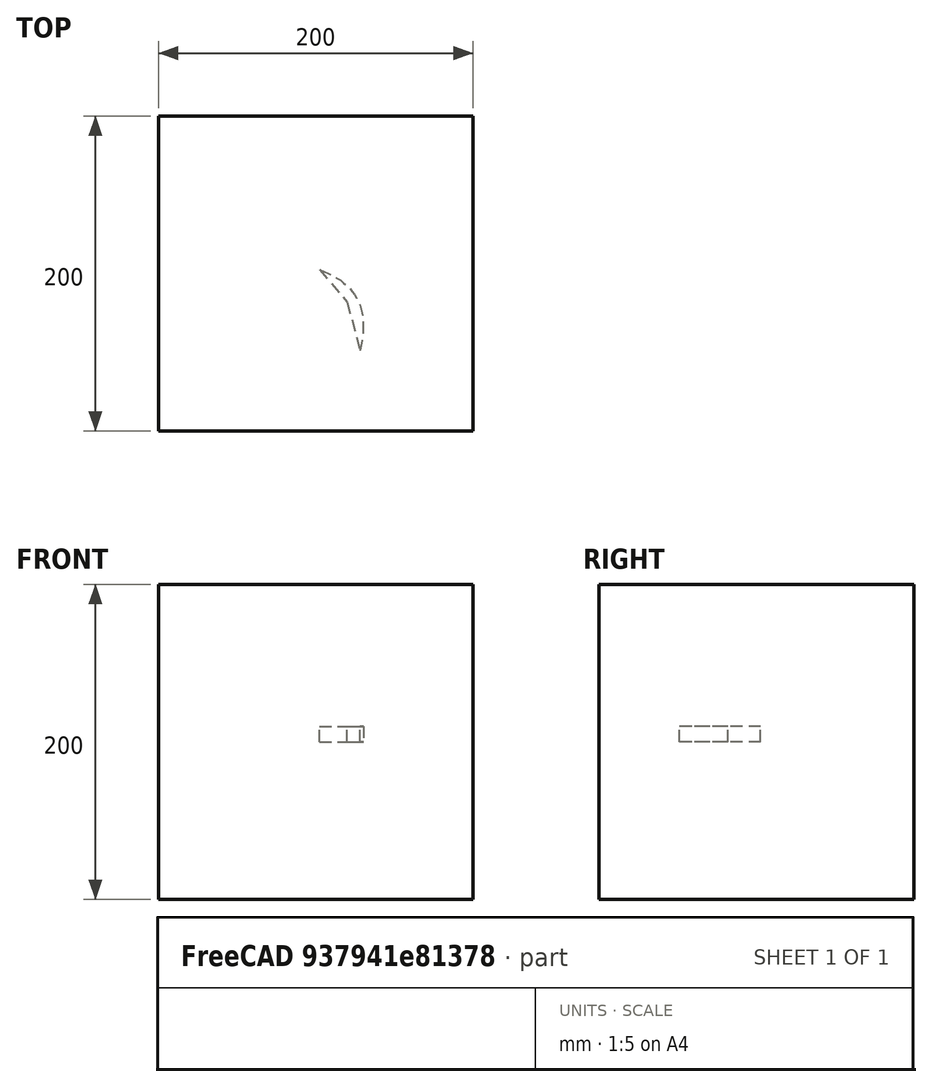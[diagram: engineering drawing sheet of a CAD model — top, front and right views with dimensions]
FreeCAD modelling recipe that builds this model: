
FCSTD DOCUMENT  (FreeCAD 0.21R33694 (Git))
Label: extrudedParabola-2
License: All rights reserved
LicenseURL: http://en.wikipedia.org/wiki/All_rights_reserved
objects: App::DocumentObjectGroupPython×1248, App::Part×2, Part::FeaturePython×1, Sketcher::SketchObject×1, Part::Extrusion×1
note: 3 computed .brp shape members not serialized (recipe doc carries the construction recipe); baked Part::Feature solids carry a one-line shape summary decoded from their .brp

FEATURE [App::DocumentObjectGroupPython] HALFPI  # scripted group (container) (typed FeaturePython)
  name = HALFPI
  value = pi/2.
FEATURE [App::DocumentObjectGroupPython] PI  # scripted group (container) (typed FeaturePython)
  name = PI
  value = 1.*pi
FEATURE [App::DocumentObjectGroupPython] TWOPI  # scripted group (container) (typed FeaturePython)
  name = TWOPI
  value = 2.*pi
FEATURE [App::DocumentObjectGroupPython] Constants  # scripted group (container) (typed FeaturePython)
  Group = -> [HALFPI,PI,TWOPI]
FEATURE [App::DocumentObjectGroupPython] Variables  # scripted group (container) (typed FeaturePython)
FEATURE [App::DocumentObjectGroupPython] Quantities  # scripted group (container) (typed FeaturePython)
FEATURE [App::DocumentObjectGroupPython] Isotopes  # scripted group (container) (typed FeaturePython)
FEATURE [App::DocumentObjectGroupPython] Elements  # scripted group (container) (typed FeaturePython)
FEATURE [App::DocumentObjectGroupPython] G4Isotopes  # scripted group (container) (typed FeaturePython)
FEATURE [App::DocumentObjectGroupPython] H_element  # scripted group (container) (typed FeaturePython)
  Z = 1
  atom_value = 1.008
  formula = H
  name = H_element
FEATURE [App::DocumentObjectGroupPython] He_element  # scripted group (container) (typed FeaturePython)
  Z = 2
  atom_value = 4.0026
  formula = He
  name = He_element
FEATURE [App::DocumentObjectGroupPython] Li_element  # scripted group (container) (typed FeaturePython)
  Z = 3
  atom_value = 6.94
  formula = Li
  name = Li_element
FEATURE [App::DocumentObjectGroupPython] Be_element  # scripted group (container) (typed FeaturePython)
  Z = 4
  atom_value = 9.01218
  formula = Be
  name = Be_element
FEATURE [App::DocumentObjectGroupPython] B_element  # scripted group (container) (typed FeaturePython)
  Z = 5
  atom_value = 10.81
  formula = B
  name = B_element
FEATURE [App::DocumentObjectGroupPython] C_element  # scripted group (container) (typed FeaturePython)
  Z = 6
  atom_value = 12.011
  formula = C
  name = C_element
FEATURE [App::DocumentObjectGroupPython] N_element  # scripted group (container) (typed FeaturePython)
  Z = 7
  atom_value = 14.007
  formula = N
  name = N_element
FEATURE [App::DocumentObjectGroupPython] O_element  # scripted group (container) (typed FeaturePython)
  Z = 8
  atom_value = 15.999
  formula = O
  name = O_element
FEATURE [App::DocumentObjectGroupPython] F_element  # scripted group (container) (typed FeaturePython)
  Z = 9
  atom_value = 18.9984
  formula = F
  name = F_element
FEATURE [App::DocumentObjectGroupPython] Ne_element  # scripted group (container) (typed FeaturePython)
  Z = 10
  atom_value = 20.1797
  formula = Ne
  name = Ne_element
FEATURE [App::DocumentObjectGroupPython] Na_element  # scripted group (container) (typed FeaturePython)
  Z = 11
  atom_value = 22.9898
  formula = Na
  name = Na_element
FEATURE [App::DocumentObjectGroupPython] Mg_element  # scripted group (container) (typed FeaturePython)
  Z = 12
  atom_value = 24.305
  formula = Mg
  name = Mg_element
FEATURE [App::DocumentObjectGroupPython] Al_element  # scripted group (container) (typed FeaturePython)
  Z = 13
  atom_value = 26.9815
  formula = Al
  name = Al_element
FEATURE [App::DocumentObjectGroupPython] Si_element  # scripted group (container) (typed FeaturePython)
  Z = 14
  atom_value = 28.085
  formula = Si
  name = Si_element
FEATURE [App::DocumentObjectGroupPython] P_element  # scripted group (container) (typed FeaturePython)
  Z = 15
  atom_value = 30.9738
  formula = P
  name = P_element
FEATURE [App::DocumentObjectGroupPython] S_element  # scripted group (container) (typed FeaturePython)
  Z = 16
  atom_value = 32.06
  formula = S
  name = S_element
FEATURE [App::DocumentObjectGroupPython] Cl_element  # scripted group (container) (typed FeaturePython)
  Z = 17
  atom_value = 35.45
  formula = Cl
  name = Cl_element
FEATURE [App::DocumentObjectGroupPython] Ar_element  # scripted group (container) (typed FeaturePython)
  Z = 18
  atom_value = 39.95
  formula = Ar
  name = Ar_element
FEATURE [App::DocumentObjectGroupPython] K_element  # scripted group (container) (typed FeaturePython)
  Z = 19
  atom_value = 39.0983
  formula = K
  name = K_element
FEATURE [App::DocumentObjectGroupPython] Ca_element  # scripted group (container) (typed FeaturePython)
  Z = 20
  atom_value = 40.078
  formula = Ca
  name = Ca_element
FEATURE [App::DocumentObjectGroupPython] Sc_element  # scripted group (container) (typed FeaturePython)
  Z = 21
  atom_value = 44.9559
  formula = Sc
  name = Sc_element
FEATURE [App::DocumentObjectGroupPython] Ti_element  # scripted group (container) (typed FeaturePython)
  Z = 22
  atom_value = 47.867
  formula = Ti
  name = Ti_element
FEATURE [App::DocumentObjectGroupPython] V_element  # scripted group (container) (typed FeaturePython)
  Z = 23
  atom_value = 50.9415
  formula = V
  name = V_element
FEATURE [App::DocumentObjectGroupPython] Cr_element  # scripted group (container) (typed FeaturePython)
  Z = 24
  atom_value = 51.9961
  formula = Cr
  name = Cr_element
FEATURE [App::DocumentObjectGroupPython] Mn_element  # scripted group (container) (typed FeaturePython)
  Z = 25
  atom_value = 54.938
  formula = Mn
  name = Mn_element
FEATURE [App::DocumentObjectGroupPython] Fe_element  # scripted group (container) (typed FeaturePython)
  Z = 26
  atom_value = 55.845
  formula = Fe
  name = Fe_element
FEATURE [App::DocumentObjectGroupPython] Co_element  # scripted group (container) (typed FeaturePython)
  Z = 27
  atom_value = 58.9332
  formula = Co
  name = Co_element
FEATURE [App::DocumentObjectGroupPython] Ni_element  # scripted group (container) (typed FeaturePython)
  Z = 28
  atom_value = 58.6934
  formula = Ni
  name = Ni_element
FEATURE [App::DocumentObjectGroupPython] Cu_element  # scripted group (container) (typed FeaturePython)
  Z = 29
  atom_value = 63.546
  formula = Cu
  name = Cu_element
FEATURE [App::DocumentObjectGroupPython] Zn_element  # scripted group (container) (typed FeaturePython)
  Z = 30
  atom_value = 65.38
  formula = Zn
  name = Zn_element
FEATURE [App::DocumentObjectGroupPython] Ga_element  # scripted group (container) (typed FeaturePython)
  Z = 31
  atom_value = 69.723
  formula = Ga
  name = Ga_element
FEATURE [App::DocumentObjectGroupPython] Ge_element  # scripted group (container) (typed FeaturePython)
  Z = 32
  atom_value = 72.63
  formula = Ge
  name = Ge_element
FEATURE [App::DocumentObjectGroupPython] As_element  # scripted group (container) (typed FeaturePython)
  Z = 33
  atom_value = 74.9216
  formula = As
  name = As_element
FEATURE [App::DocumentObjectGroupPython] Se_element  # scripted group (container) (typed FeaturePython)
  Z = 34
  atom_value = 78.971
  formula = Se
  name = Se_element
FEATURE [App::DocumentObjectGroupPython] Br_element  # scripted group (container) (typed FeaturePython)
  Z = 35
  atom_value = 79.904
  formula = Br
  name = Br_element
FEATURE [App::DocumentObjectGroupPython] Kr_element  # scripted group (container) (typed FeaturePython)
  Z = 36
  atom_value = 83.798
  formula = Kr
  name = Kr_element
FEATURE [App::DocumentObjectGroupPython] Rb_element  # scripted group (container) (typed FeaturePython)
  Z = 37
  atom_value = 85.4678
  formula = Rb
  name = Rb_element
FEATURE [App::DocumentObjectGroupPython] Sr_element  # scripted group (container) (typed FeaturePython)
  Z = 38
  atom_value = 87.62
  formula = Sr
  name = Sr_element
FEATURE [App::DocumentObjectGroupPython] Y_element  # scripted group (container) (typed FeaturePython)
  Z = 39
  atom_value = 88.9058
  formula = Y
  name = Y_element
FEATURE [App::DocumentObjectGroupPython] Zr_element  # scripted group (container) (typed FeaturePython)
  Z = 40
  atom_value = 91.224
  formula = Zr
  name = Zr_element
FEATURE [App::DocumentObjectGroupPython] Nb_element  # scripted group (container) (typed FeaturePython)
  Z = 41
  atom_value = 92.9064
  formula = Nb
  name = Nb_element
FEATURE [App::DocumentObjectGroupPython] Mo_element  # scripted group (container) (typed FeaturePython)
  Z = 42
  atom_value = 95.95
  formula = Mo
  name = Mo_element
FEATURE [App::DocumentObjectGroupPython] Tc_element  # scripted group (container) (typed FeaturePython)
  Z = 43
  atom_value = 97
  formula = Tc
  name = Tc_element
FEATURE [App::DocumentObjectGroupPython] Ru_element  # scripted group (container) (typed FeaturePython)
  Z = 44
  atom_value = 101.07
  formula = Ru
  name = Ru_element
FEATURE [App::DocumentObjectGroupPython] Rh_element  # scripted group (container) (typed FeaturePython)
  Z = 45
  atom_value = 102.905
  formula = Rh
  name = Rh_element
FEATURE [App::DocumentObjectGroupPython] Pd_element  # scripted group (container) (typed FeaturePython)
  Z = 46
  atom_value = 106.42
  formula = Pd
  name = Pd_element
FEATURE [App::DocumentObjectGroupPython] Ag_element  # scripted group (container) (typed FeaturePython)
  Z = 47
  atom_value = 107.868
  formula = Ag
  name = Ag_element
FEATURE [App::DocumentObjectGroupPython] Cd_element  # scripted group (container) (typed FeaturePython)
  Z = 48
  atom_value = 112.414
  formula = Cd
  name = Cd_element
FEATURE [App::DocumentObjectGroupPython] In_element  # scripted group (container) (typed FeaturePython)
  Z = 49
  atom_value = 114.818
  formula = In
  name = In_element
FEATURE [App::DocumentObjectGroupPython] Sn_element  # scripted group (container) (typed FeaturePython)
  Z = 50
  atom_value = 118.71
  formula = Sn
  name = Sn_element
FEATURE [App::DocumentObjectGroupPython] Sb_element  # scripted group (container) (typed FeaturePython)
  Z = 51
  atom_value = 121.76
  formula = Sb
  name = Sb_element
FEATURE [App::DocumentObjectGroupPython] Te_element  # scripted group (container) (typed FeaturePython)
  Z = 52
  atom_value = 127.6
  formula = Te
  name = Te_element
FEATURE [App::DocumentObjectGroupPython] I_element  # scripted group (container) (typed FeaturePython)
  Z = 53
  atom_value = 126.904
  formula = I
  name = I_element
FEATURE [App::DocumentObjectGroupPython] Xe_element  # scripted group (container) (typed FeaturePython)
  Z = 54
  atom_value = 131.293
  formula = Xe
  name = Xe_element
FEATURE [App::DocumentObjectGroupPython] Cs_element  # scripted group (container) (typed FeaturePython)
  Z = 55
  atom_value = 132.905
  formula = Cs
  name = Cs_element
FEATURE [App::DocumentObjectGroupPython] Ba_element  # scripted group (container) (typed FeaturePython)
  Z = 56
  atom_value = 137.327
  formula = Ba
  name = Ba_element
FEATURE [App::DocumentObjectGroupPython] La_element  # scripted group (container) (typed FeaturePython)
  Z = 57
  atom_value = 138.905
  formula = La
  name = La_element
FEATURE [App::DocumentObjectGroupPython] Ce_element  # scripted group (container) (typed FeaturePython)
  Z = 58
  atom_value = 140.116
  formula = Ce
  name = Ce_element
FEATURE [App::DocumentObjectGroupPython] Pr_element  # scripted group (container) (typed FeaturePython)
  Z = 59
  atom_value = 140.908
  formula = Pr
  name = Pr_element
FEATURE [App::DocumentObjectGroupPython] Nd_element  # scripted group (container) (typed FeaturePython)
  Z = 60
  atom_value = 144.242
  formula = Nd
  name = Nd_element
FEATURE [App::DocumentObjectGroupPython] Pm_element  # scripted group (container) (typed FeaturePython)
  Z = 61
  atom_value = 145
  formula = Pm
  name = Pm_element
FEATURE [App::DocumentObjectGroupPython] Sm_element  # scripted group (container) (typed FeaturePython)
  Z = 62
  atom_value = 150.36
  formula = Sm
  name = Sm_element
FEATURE [App::DocumentObjectGroupPython] Eu_element  # scripted group (container) (typed FeaturePython)
  Z = 63
  atom_value = 151.964
  formula = Eu
  name = Eu_element
FEATURE [App::DocumentObjectGroupPython] Gd_element  # scripted group (container) (typed FeaturePython)
  Z = 64
  atom_value = 157.25
  formula = Gd
  name = Gd_element
FEATURE [App::DocumentObjectGroupPython] Tb_element  # scripted group (container) (typed FeaturePython)
  Z = 65
  atom_value = 158.925
  formula = Tb
  name = Tb_element
FEATURE [App::DocumentObjectGroupPython] Dy_element  # scripted group (container) (typed FeaturePython)
  Z = 66
  atom_value = 162.5
  formula = Dy
  name = Dy_element
FEATURE [App::DocumentObjectGroupPython] Ho_element  # scripted group (container) (typed FeaturePython)
  Z = 67
  atom_value = 164.93
  formula = Ho
  name = Ho_element
FEATURE [App::DocumentObjectGroupPython] Er_element  # scripted group (container) (typed FeaturePython)
  Z = 68
  atom_value = 167.259
  formula = Er
  name = Er_element
FEATURE [App::DocumentObjectGroupPython] Tm_element  # scripted group (container) (typed FeaturePython)
  Z = 69
  atom_value = 168.934
  formula = Tm
  name = Tm_element
FEATURE [App::DocumentObjectGroupPython] Yb_element  # scripted group (container) (typed FeaturePython)
  Z = 70
  atom_value = 173.045
  formula = Yb
  name = Yb_element
FEATURE [App::DocumentObjectGroupPython] Lu_element  # scripted group (container) (typed FeaturePython)
  Z = 71
  atom_value = 174.967
  formula = Lu
  name = Lu_element
FEATURE [App::DocumentObjectGroupPython] Hf_element  # scripted group (container) (typed FeaturePython)
  Z = 72
  atom_value = 178.49
  formula = Hf
  name = Hf_element
FEATURE [App::DocumentObjectGroupPython] Ta_element  # scripted group (container) (typed FeaturePython)
  Z = 73
  atom_value = 180.948
  formula = Ta
  name = Ta_element
FEATURE [App::DocumentObjectGroupPython] W_element  # scripted group (container) (typed FeaturePython)
  Z = 74
  atom_value = 183.84
  formula = W
  name = W_element
FEATURE [App::DocumentObjectGroupPython] Re_element  # scripted group (container) (typed FeaturePython)
  Z = 75
  atom_value = 186.207
  formula = Re
  name = Re_element
FEATURE [App::DocumentObjectGroupPython] Os_element  # scripted group (container) (typed FeaturePython)
  Z = 76
  atom_value = 190.23
  formula = Os
  name = Os_element
FEATURE [App::DocumentObjectGroupPython] Ir_element  # scripted group (container) (typed FeaturePython)
  Z = 77
  atom_value = 192.217
  formula = Ir
  name = Ir_element
FEATURE [App::DocumentObjectGroupPython] Pt_element  # scripted group (container) (typed FeaturePython)
  Z = 78
  atom_value = 195.084
  formula = Pt
  name = Pt_element
FEATURE [App::DocumentObjectGroupPython] Au_element  # scripted group (container) (typed FeaturePython)
  Z = 79
  atom_value = 196.967
  formula = Au
  name = Au_element
FEATURE [App::DocumentObjectGroupPython] Hg_element  # scripted group (container) (typed FeaturePython)
  Z = 80
  atom_value = 200.592
  formula = Hg
  name = Hg_element
FEATURE [App::DocumentObjectGroupPython] Tl_element  # scripted group (container) (typed FeaturePython)
  Z = 81
  atom_value = 204.38
  formula = Tl
  name = Tl_element
FEATURE [App::DocumentObjectGroupPython] Pb_element  # scripted group (container) (typed FeaturePython)
  Z = 82
  atom_value = 207.2
  formula = Pb
  name = Pb_element
FEATURE [App::DocumentObjectGroupPython] Bi_element  # scripted group (container) (typed FeaturePython)
  Z = 83
  atom_value = 208.98
  formula = Bi
  name = Bi_element
FEATURE [App::DocumentObjectGroupPython] Po_element  # scripted group (container) (typed FeaturePython)
  Z = 84
  atom_value = 209
  formula = Po
  name = Po_element
FEATURE [App::DocumentObjectGroupPython] At_element  # scripted group (container) (typed FeaturePython)
  Z = 85
  atom_value = 210
  formula = At
  name = At_element
FEATURE [App::DocumentObjectGroupPython] Rn_element  # scripted group (container) (typed FeaturePython)
  Z = 86
  atom_value = 222
  formula = Rn
  name = Rn_element
FEATURE [App::DocumentObjectGroupPython] Fr_element  # scripted group (container) (typed FeaturePython)
  Z = 87
  atom_value = 223
  formula = Fr
  name = Fr_element
FEATURE [App::DocumentObjectGroupPython] Ra_element  # scripted group (container) (typed FeaturePython)
  Z = 88
  atom_value = 226
  formula = Ra
  name = Ra_element
FEATURE [App::DocumentObjectGroupPython] Ac_element  # scripted group (container) (typed FeaturePython)
  Z = 89
  atom_value = 227
  formula = Ac
  name = Ac_element
FEATURE [App::DocumentObjectGroupPython] Th_element  # scripted group (container) (typed FeaturePython)
  Z = 90
  atom_value = 232.038
  formula = Th
  name = Th_element
FEATURE [App::DocumentObjectGroupPython] Pa_element  # scripted group (container) (typed FeaturePython)
  Z = 91
  atom_value = 231.036
  formula = Pa
  name = Pa_element
FEATURE [App::DocumentObjectGroupPython] U_element  # scripted group (container) (typed FeaturePython)
  Z = 92
  atom_value = 238.029
  formula = U
  name = U_element
FEATURE [App::DocumentObjectGroupPython] Np_element  # scripted group (container) (typed FeaturePython)
  Z = 93
  atom_value = 237
  formula = Np
  name = Np_element
FEATURE [App::DocumentObjectGroupPython] Pu_element  # scripted group (container) (typed FeaturePython)
  Z = 94
  atom_value = 244
  formula = Pu
  name = Pu_element
FEATURE [App::DocumentObjectGroupPython] Am_element  # scripted group (container) (typed FeaturePython)
  Z = 95
  atom_value = 243
  formula = Am
  name = Am_element
FEATURE [App::DocumentObjectGroupPython] Cm_element  # scripted group (container) (typed FeaturePython)
  Z = 96
  atom_value = 247
  formula = Cm
  name = Cm_element
FEATURE [App::DocumentObjectGroupPython] Bk_element  # scripted group (container) (typed FeaturePython)
  Z = 97
  atom_value = 247
  formula = Bk
  name = Bk_element
FEATURE [App::DocumentObjectGroupPython] Cf_element  # scripted group (container) (typed FeaturePython)
  Z = 98
  atom_value = 251
  formula = Cf
  name = Cf_element
FEATURE [App::DocumentObjectGroupPython] G4Elements  # scripted group (container) (typed FeaturePython)
  Group = -> [H_element,He_element,Li_element,Be_element,B_element,C_element,N_element,O_element,F_element,Ne_element,Na_element,Mg_element,Al_element,Si_element,P_element,S_element,Cl_element,Ar_element,K_element,Ca_element,Sc_element,Ti_element,V_element,Cr_element,Mn_element,Fe_element,Co_element,Ni_element,Cu_element,Zn_element,Ga_element,Ge_element,As_element,Se_element,Br_element,Kr_element,Rb_element,+61 more]
FEATURE [App::DocumentObjectGroupPython] H_element001  label="H_element : 0.101"  # scripted group (container) (typed FeaturePython)
  n = 0.101327
FEATURE [App::DocumentObjectGroupPython] C_element001  label="C_element : 0.775"  # scripted group (container) (typed FeaturePython)
  n = 0.7755
FEATURE [App::DocumentObjectGroupPython] N_element001  label="N_element : 0.035"  # scripted group (container) (typed FeaturePython)
  n = 0.035057
FEATURE [App::DocumentObjectGroupPython] O_element001  label="O_element : 0.052"  # scripted group (container) (typed FeaturePython)
  n = 0.0523159
FEATURE [App::DocumentObjectGroupPython] F_element001  label="F_element : 0.017"  # scripted group (container) (typed FeaturePython)
  n = 0.017422
FEATURE [App::DocumentObjectGroupPython] Ca_element001  label="Ca_element : 0.018"  # scripted group (container) (typed FeaturePython)
  n = 0.018378
FEATURE [App::DocumentObjectGroupPython] G4_A_150_TISSUE  label="G4_A-150_TISSUE"  # scripted group (container) (typed FeaturePython)
  Dunit = g/cm3
  Dvalue = 1.127
  Group = -> [H_element001,C_element001,N_element001,O_element001,F_element001,Ca_element001]
  conduct = 2
  density = 1
  expand = 3
  formula = G4_A-150_TISSUE
  name = G4_A-150_TISSUE
  specific = 4
FEATURE [App::DocumentObjectGroupPython] C_element002  label="C_element : 3"  # scripted group (container) (typed FeaturePython)
  n = 3
  ref = C_element
FEATURE [App::DocumentObjectGroupPython] H_element002  label="H_element : 6"  # scripted group (container) (typed FeaturePython)
  n = 6
  ref = H_element
FEATURE [App::DocumentObjectGroupPython] O_element002  label="O_element : 1"  # scripted group (container) (typed FeaturePython)
  n = 1
  ref = O_element
FEATURE [App::DocumentObjectGroupPython] G4_ACETONE  # scripted group (container) (typed FeaturePython)
  Dunit = g/cm3
  Dvalue = 0.7899
  Group = -> [C_element002,H_element002,O_element002]
  conduct = 2
  density = 1
  expand = 3
  formula = G4_ACETONE
  name = G4_ACETONE
  specific = 4
FEATURE [App::DocumentObjectGroupPython] C_element003  label="C_element : 2"  # scripted group (container) (typed FeaturePython)
  n = 2
  ref = C_element
FEATURE [App::DocumentObjectGroupPython] H_element003  label="H_element : 2"  # scripted group (container) (typed FeaturePython)
  n = 2
  ref = H_element
FEATURE [App::DocumentObjectGroupPython] G4_ACETYLENE  # scripted group (container) (typed FeaturePython)
  Dunit = g/cm3
  Dvalue = 0.0010967
  Group = -> [C_element003,H_element003]
  conduct = 2
  density = 1
  expand = 3
  formula = G4_ACETYLENE
  name = G4_ACETYLENE
  specific = 4
FEATURE [App::DocumentObjectGroupPython] C_element004  label="C_element : 5"  # scripted group (container) (typed FeaturePython)
  n = 5
  ref = C_element
FEATURE [App::DocumentObjectGroupPython] H_element004  label="H_element : 5"  # scripted group (container) (typed FeaturePython)
  n = 5
  ref = H_element
FEATURE [App::DocumentObjectGroupPython] N_element002  label="N_element : 5"  # scripted group (container) (typed FeaturePython)
  n = 5
  ref = N_element
FEATURE [App::DocumentObjectGroupPython] G4_ADENINE  # scripted group (container) (typed FeaturePython)
  Dunit = g/cm3
  Dvalue = 1.6
  Group = -> [C_element004,H_element004,N_element002]
  conduct = 2
  density = 1
  expand = 3
  formula = G4_ADENINE
  name = G4_ADENINE
  specific = 4
FEATURE [App::DocumentObjectGroupPython] H_element005  label="H_element : 0.114"  # scripted group (container) (typed FeaturePython)
  n = 0.114
FEATURE [App::DocumentObjectGroupPython] C_element005  label="C_element : 0.598"  # scripted group (container) (typed FeaturePython)
  n = 0.598
FEATURE [App::DocumentObjectGroupPython] N_element003  label="N_element : 0.007"  # scripted group (container) (typed FeaturePython)
  n = 0.007
FEATURE [App::DocumentObjectGroupPython] O_element003  label="O_element : 0.278"  # scripted group (container) (typed FeaturePython)
  n = 0.278
FEATURE [App::DocumentObjectGroupPython] Na_element001  label="Na_element : 0.001"  # scripted group (container) (typed FeaturePython)
  n = 0.001
FEATURE [App::DocumentObjectGroupPython] S_element001  label="S_element : 0.001"  # scripted group (container) (typed FeaturePython)
  n = 0.001
FEATURE [App::DocumentObjectGroupPython] Cl_element001  label="Cl_element : 0.001"  # scripted group (container) (typed FeaturePython)
  n = 0.001
FEATURE [App::DocumentObjectGroupPython] G4_ADIPOSE_TISSUE_ICRP  # scripted group (container) (typed FeaturePython)
  Dunit = g/cm3
  Dvalue = 0.95
  Group = -> [H_element005,C_element005,N_element003,O_element003,Na_element001,S_element001,Cl_element001]
  conduct = 2
  density = 1
  expand = 3
  formula = G4_ADIPOSE_TISSUE_ICRP
  name = G4_ADIPOSE_TISSUE_ICRP
  specific = 4
FEATURE [App::DocumentObjectGroupPython] C_element006  label="C_element : 0.000"  # scripted group (container) (typed FeaturePython)
  n = 0.000124
FEATURE [App::DocumentObjectGroupPython] N_element004  label="N_element : 0.755"  # scripted group (container) (typed FeaturePython)
  n = 0.755268
FEATURE [App::DocumentObjectGroupPython] O_element004  label="O_element : 0.232"  # scripted group (container) (typed FeaturePython)
  n = 0.231781
FEATURE [App::DocumentObjectGroupPython] Ar_element001  label="Ar_element : 0.013"  # scripted group (container) (typed FeaturePython)
  n = 0.012827
FEATURE [App::DocumentObjectGroupPython] G4_AIR  # scripted group (container) (typed FeaturePython)
  Dunit = g/cm3
  Dvalue = 0.00120479
  Group = -> [C_element006,N_element004,O_element004,Ar_element001]
  conduct = 2
  density = 1
  expand = 3
  formula = G4_AIR
  name = G4_AIR
  specific = 4
FEATURE [App::DocumentObjectGroupPython] C_element007  label="C_element : 006"  # scripted group (container) (typed FeaturePython)
  n = 3
  ref = C_element
FEATURE [App::DocumentObjectGroupPython] H_element006  label="H_element : 7"  # scripted group (container) (typed FeaturePython)
  n = 7
  ref = H_element
FEATURE [App::DocumentObjectGroupPython] N_element005  label="N_element : 1"  # scripted group (container) (typed FeaturePython)
  n = 1
  ref = N_element
FEATURE [App::DocumentObjectGroupPython] O_element005  label="O_element : 2"  # scripted group (container) (typed FeaturePython)
  n = 2
  ref = O_element
FEATURE [App::DocumentObjectGroupPython] G4_ALANINE  # scripted group (container) (typed FeaturePython)
  Dunit = g/cm3
  Dvalue = 1.42
  Group = -> [C_element007,H_element006,N_element005,O_element005]
  conduct = 2
  density = 1
  expand = 3
  formula = G4_ALANINE
  name = G4_ALANINE
  specific = 4
FEATURE [App::DocumentObjectGroupPython] Al_element001  label="Al_element : 2"  # scripted group (container) (typed FeaturePython)
  n = 2
  ref = Al_element
FEATURE [App::DocumentObjectGroupPython] O_element006  label="O_element : 3"  # scripted group (container) (typed FeaturePython)
  n = 3
  ref = O_element
FEATURE [App::DocumentObjectGroupPython] G4_ALUMINUM_OXIDE  # scripted group (container) (typed FeaturePython)
  Dunit = g/cm3
  Dvalue = 3.97
  Group = -> [Al_element001,O_element006]
  conduct = 2
  density = 1
  expand = 3
  formula = G4_ALUMINUM_OXIDE
  name = G4_ALUMINUM_OXIDE
  specific = 4
FEATURE [App::DocumentObjectGroupPython] H_element007  label="H_element : 0.106"  # scripted group (container) (typed FeaturePython)
  n = 0.10593
FEATURE [App::DocumentObjectGroupPython] C_element008  label="C_element : 0.789"  # scripted group (container) (typed FeaturePython)
  n = 0.788974
FEATURE [App::DocumentObjectGroupPython] O_element007  label="O_element : 0.105"  # scripted group (container) (typed FeaturePython)
  n = 0.105096
FEATURE [App::DocumentObjectGroupPython] G4_AMBER  # scripted group (container) (typed FeaturePython)
  Dunit = g/cm3
  Dvalue = 1.1
  Group = -> [H_element007,C_element008,O_element007]
  conduct = 2
  density = 1
  expand = 3
  formula = G4_AMBER
  name = G4_AMBER
  specific = 4
FEATURE [App::DocumentObjectGroupPython] N_element006  label="N_element : 006"  # scripted group (container) (typed FeaturePython)
  n = 1
  ref = N_element
FEATURE [App::DocumentObjectGroupPython] H_element008  label="H_element : 3"  # scripted group (container) (typed FeaturePython)
  n = 3
  ref = H_element
FEATURE [App::DocumentObjectGroupPython] G4_AMMONIA  # scripted group (container) (typed FeaturePython)
  Dunit = g/cm3
  Dvalue = 0.000826019
  Group = -> [N_element006,H_element008]
  conduct = 2
  density = 1
  expand = 3
  formula = G4_AMMONIA
  name = G4_AMMONIA
  specific = 4
FEATURE [App::DocumentObjectGroupPython] C_element009  label="C_element : 6"  # scripted group (container) (typed FeaturePython)
  n = 6
  ref = C_element
FEATURE [App::DocumentObjectGroupPython] H_element009  label="H_element : 008"  # scripted group (container) (typed FeaturePython)
  n = 7
  ref = H_element
FEATURE [App::DocumentObjectGroupPython] N_element007  label="N_element : 007"  # scripted group (container) (typed FeaturePython)
  n = 1
  ref = N_element
FEATURE [App::DocumentObjectGroupPython] G4_ANILINE  # scripted group (container) (typed FeaturePython)
  Dunit = g/cm3
  Dvalue = 1.0235
  Group = -> [C_element009,H_element009,N_element007]
  conduct = 2
  density = 1
  expand = 3
  formula = G4_ANILINE
  name = G4_ANILINE
  specific = 4
FEATURE [App::DocumentObjectGroupPython] C_element010  label="C_element : 14"  # scripted group (container) (typed FeaturePython)
  n = 14
  ref = C_element
FEATURE [App::DocumentObjectGroupPython] H_element010  label="H_element : 10"  # scripted group (container) (typed FeaturePython)
  n = 10
  ref = H_element
FEATURE [App::DocumentObjectGroupPython] G4_ANTHRACENE  # scripted group (container) (typed FeaturePython)
  Dunit = g/cm3
  Dvalue = 1.283
  Group = -> [C_element010,H_element010]
  conduct = 2
  density = 1
  expand = 3
  formula = G4_ANTHRACENE
  name = G4_ANTHRACENE
  specific = 4
FEATURE [App::DocumentObjectGroupPython] H_element011  label="H_element : 0.065"  # scripted group (container) (typed FeaturePython)
  n = 0.0654709
FEATURE [App::DocumentObjectGroupPython] C_element011  label="C_element : 0.537"  # scripted group (container) (typed FeaturePython)
  n = 0.536944
FEATURE [App::DocumentObjectGroupPython] N_element008  label="N_element : 0.021"  # scripted group (container) (typed FeaturePython)
  n = 0.0215
FEATURE [App::DocumentObjectGroupPython] O_element008  label="O_element : 0.032"  # scripted group (container) (typed FeaturePython)
  n = 0.032085
FEATURE [App::DocumentObjectGroupPython] F_element002  label="F_element : 0.167"  # scripted group (container) (typed FeaturePython)
  n = 0.167411
FEATURE [App::DocumentObjectGroupPython] Ca_element002  label="Ca_element : 0.177"  # scripted group (container) (typed FeaturePython)
  n = 0.176589
FEATURE [App::DocumentObjectGroupPython] G4_B_100_BONE  label="G4_B-100_BONE"  # scripted group (container) (typed FeaturePython)
  Dunit = g/cm3
  Dvalue = 1.45
  Group = -> [H_element011,C_element011,N_element008,O_element008,F_element002,Ca_element002]
  conduct = 2
  density = 1
  expand = 3
  formula = G4_B-100_BONE
  name = G4_B-100_BONE
  specific = 4
FEATURE [App::DocumentObjectGroupPython] H_element012  label="H_element : 0.057"  # scripted group (container) (typed FeaturePython)
  n = 0.057441
FEATURE [App::DocumentObjectGroupPython] C_element012  label="C_element : 0.790"  # scripted group (container) (typed FeaturePython)
  n = 0.774591
FEATURE [App::DocumentObjectGroupPython] O_element009  label="O_element : 0.168"  # scripted group (container) (typed FeaturePython)
  n = 0.167968
FEATURE [App::DocumentObjectGroupPython] G4_BAKELITE  # scripted group (container) (typed FeaturePython)
  Dunit = g/cm3
  Dvalue = 1.25
  Group = -> [H_element012,C_element012,O_element009]
  conduct = 2
  density = 1
  expand = 3
  formula = G4_BAKELITE
  name = G4_BAKELITE
  specific = 4
FEATURE [App::DocumentObjectGroupPython] Ba_element001  label="Ba_element : 1"  # scripted group (container) (typed FeaturePython)
  n = 1
  ref = Ba_element
FEATURE [App::DocumentObjectGroupPython] F_element003  label="F_element : 2"  # scripted group (container) (typed FeaturePython)
  n = 2
  ref = F_element
FEATURE [App::DocumentObjectGroupPython] G4_BARIUM_FLUORIDE  # scripted group (container) (typed FeaturePython)
  Dunit = g/cm3
  Dvalue = 4.89
  Group = -> [Ba_element001,F_element003]
  conduct = 2
  density = 1
  expand = 3
  formula = G4_BARIUM_FLUORIDE
  name = G4_BARIUM_FLUORIDE
  specific = 4
FEATURE [App::DocumentObjectGroupPython] Ba_element002  label="Ba_element : 002"  # scripted group (container) (typed FeaturePython)
  n = 1
  ref = Ba_element
FEATURE [App::DocumentObjectGroupPython] S_element002  label="S_element : 1"  # scripted group (container) (typed FeaturePython)
  n = 1
  ref = S_element
FEATURE [App::DocumentObjectGroupPython] O_element010  label="O_element : 4"  # scripted group (container) (typed FeaturePython)
  n = 4
  ref = O_element
FEATURE [App::DocumentObjectGroupPython] G4_BARIUM_SULFATE  # scripted group (container) (typed FeaturePython)
  Dunit = g/cm3
  Dvalue = 4.5
  Group = -> [Ba_element002,S_element002,O_element010]
  conduct = 2
  density = 1
  expand = 3
  formula = G4_BARIUM_SULFATE
  name = G4_BARIUM_SULFATE
  specific = 4
FEATURE [App::DocumentObjectGroupPython] C_element013  label="C_element : 007"  # scripted group (container) (typed FeaturePython)
  n = 6
  ref = C_element
FEATURE [App::DocumentObjectGroupPython] H_element013  label="H_element : 009"  # scripted group (container) (typed FeaturePython)
  n = 6
  ref = H_element
FEATURE [App::DocumentObjectGroupPython] G4_BENZENE  # scripted group (container) (typed FeaturePython)
  Dunit = g/cm3
  Dvalue = 0.87865
  Group = -> [C_element013,H_element013]
  conduct = 2
  density = 1
  expand = 3
  formula = G4_BENZENE
  name = G4_BENZENE
  specific = 4
FEATURE [App::DocumentObjectGroupPython] Be_element001  label="Be_element : 1"  # scripted group (container) (typed FeaturePython)
  n = 1
  ref = Be_element
FEATURE [App::DocumentObjectGroupPython] O_element011  label="O_element : 005"  # scripted group (container) (typed FeaturePython)
  n = 1
  ref = O_element
FEATURE [App::DocumentObjectGroupPython] G4_BERYLLIUM_OXIDE  # scripted group (container) (typed FeaturePython)
  Dunit = g/cm3
  Dvalue = 3.01
  Group = -> [Be_element001,O_element011]
  conduct = 2
  density = 1
  expand = 3
  formula = G4_BERYLLIUM_OXIDE
  name = G4_BERYLLIUM_OXIDE
  specific = 4
FEATURE [App::DocumentObjectGroupPython] Bi_element001  label="Bi_element : 4"  # scripted group (container) (typed FeaturePython)
  n = 4
  ref = Bi_element
FEATURE [App::DocumentObjectGroupPython] Ge_element001  label="Ge_element : 3"  # scripted group (container) (typed FeaturePython)
  n = 3
  ref = Ge_element
FEATURE [App::DocumentObjectGroupPython] O_element012  label="O_element : 12"  # scripted group (container) (typed FeaturePython)
  n = 12
  ref = O_element
FEATURE [App::DocumentObjectGroupPython] G4_BGO  # scripted group (container) (typed FeaturePython)
  Dunit = g/cm3
  Dvalue = 7.13
  Group = -> [Bi_element001,Ge_element001,O_element012]
  conduct = 2
  density = 1
  expand = 3
  formula = G4_BGO
  name = G4_BGO
  specific = 4
FEATURE [App::DocumentObjectGroupPython] H_element014  label="H_element : 0.102"  # scripted group (container) (typed FeaturePython)
  n = 0.102
FEATURE [App::DocumentObjectGroupPython] C_element014  label="C_element : 0.110"  # scripted group (container) (typed FeaturePython)
  n = 0.11
FEATURE [App::DocumentObjectGroupPython] N_element009  label="N_element : 0.033"  # scripted group (container) (typed FeaturePython)
  n = 0.033
FEATURE [App::DocumentObjectGroupPython] O_element013  label="O_element : 0.745"  # scripted group (container) (typed FeaturePython)
  n = 0.745
FEATURE [App::DocumentObjectGroupPython] Na_element002  label="Na_element : 0.002"  # scripted group (container) (typed FeaturePython)
  n = 0.001
FEATURE [App::DocumentObjectGroupPython] P_element001  label="P_element : 0.001"  # scripted group (container) (typed FeaturePython)
  n = 0.001
FEATURE [App::DocumentObjectGroupPython] S_element003  label="S_element : 0.002"  # scripted group (container) (typed FeaturePython)
  n = 0.002
FEATURE [App::DocumentObjectGroupPython] Cl_element002  label="Cl_element : 0.003"  # scripted group (container) (typed FeaturePython)
  n = 0.003
FEATURE [App::DocumentObjectGroupPython] K_element001  label="K_element : 0.002"  # scripted group (container) (typed FeaturePython)
  n = 0.002
FEATURE [App::DocumentObjectGroupPython] Fe_element001  label="Fe_element : 0.001"  # scripted group (container) (typed FeaturePython)
  n = 0.001
FEATURE [App::DocumentObjectGroupPython] G4_BLOOD_ICRP  # scripted group (container) (typed FeaturePython)
  Dunit = g/cm3
  Dvalue = 1.06
  Group = -> [H_element014,C_element014,N_element009,O_element013,Na_element002,P_element001,S_element003,Cl_element002,K_element001,Fe_element001]
  conduct = 2
  density = 1
  expand = 3
  formula = G4_BLOOD_ICRP
  name = G4_BLOOD_ICRP
  specific = 4
FEATURE [App::DocumentObjectGroupPython] H_element015  label="H_element : 0.064"  # scripted group (container) (typed FeaturePython)
  n = 0.064
FEATURE [App::DocumentObjectGroupPython] C_element015  label="C_element : 0.278"  # scripted group (container) (typed FeaturePython)
  n = 0.278
FEATURE [App::DocumentObjectGroupPython] N_element010  label="N_element : 0.027"  # scripted group (container) (typed FeaturePython)
  n = 0.027
FEATURE [App::DocumentObjectGroupPython] O_element014  label="O_element : 0.410"  # scripted group (container) (typed FeaturePython)
  n = 0.41
FEATURE [App::DocumentObjectGroupPython] Mg_element001  label="Mg_element : 0.002"  # scripted group (container) (typed FeaturePython)
  n = 0.002
FEATURE [App::DocumentObjectGroupPython] P_element002  label="P_element : 0.070"  # scripted group (container) (typed FeaturePython)
  n = 0.07
FEATURE [App::DocumentObjectGroupPython] S_element004  label="S_element : 0.003"  # scripted group (container) (typed FeaturePython)
  n = 0.002
FEATURE [App::DocumentObjectGroupPython] Ca_element003  label="Ca_element : 0.147"  # scripted group (container) (typed FeaturePython)
  n = 0.147
FEATURE [App::DocumentObjectGroupPython] G4_BONE_COMPACT_ICRU  # scripted group (container) (typed FeaturePython)
  Dunit = g/cm3
  Dvalue = 1.85
  Group = -> [H_element015,C_element015,N_element010,O_element014,Mg_element001,P_element002,S_element004,Ca_element003]
  conduct = 2
  density = 1
  expand = 3
  formula = G4_BONE_COMPACT_ICRU
  name = G4_BONE_COMPACT_ICRU
  specific = 4
FEATURE [App::DocumentObjectGroupPython] H_element016  label="H_element : 0.034"  # scripted group (container) (typed FeaturePython)
  n = 0.034
FEATURE [App::DocumentObjectGroupPython] C_element016  label="C_element : 0.155"  # scripted group (container) (typed FeaturePython)
  n = 0.155
FEATURE [App::DocumentObjectGroupPython] N_element011  label="N_element : 0.042"  # scripted group (container) (typed FeaturePython)
  n = 0.042
FEATURE [App::DocumentObjectGroupPython] O_element015  label="O_element : 0.435"  # scripted group (container) (typed FeaturePython)
  n = 0.435
FEATURE [App::DocumentObjectGroupPython] Na_element003  label="Na_element : 0.003"  # scripted group (container) (typed FeaturePython)
  n = 0.001
FEATURE [App::DocumentObjectGroupPython] Mg_element002  label="Mg_element : 0.003"  # scripted group (container) (typed FeaturePython)
  n = 0.002
FEATURE [App::DocumentObjectGroupPython] P_element003  label="P_element : 0.103"  # scripted group (container) (typed FeaturePython)
  n = 0.103
FEATURE [App::DocumentObjectGroupPython] S_element005  label="S_element : 0.004"  # scripted group (container) (typed FeaturePython)
  n = 0.003
FEATURE [App::DocumentObjectGroupPython] Ca_element004  label="Ca_element : 0.225"  # scripted group (container) (typed FeaturePython)
  n = 0.225
FEATURE [App::DocumentObjectGroupPython] G4_BONE_CORTICAL_ICRP  # scripted group (container) (typed FeaturePython)
  Dunit = g/cm3
  Dvalue = 1.92
  Group = -> [H_element016,C_element016,N_element011,O_element015,Na_element003,Mg_element002,P_element003,S_element005,Ca_element004]
  conduct = 2
  density = 1
  expand = 3
  formula = G4_BONE_CORTICAL_ICRP
  name = G4_BONE_CORTICAL_ICRP
  specific = 4
FEATURE [App::DocumentObjectGroupPython] B_element001  label="B_element : 4"  # scripted group (container) (typed FeaturePython)
  n = 4
  ref = B_element
FEATURE [App::DocumentObjectGroupPython] C_element017  label="C_element : 1"  # scripted group (container) (typed FeaturePython)
  n = 1
  ref = C_element
FEATURE [App::DocumentObjectGroupPython] G4_BORON_CARBIDE  # scripted group (container) (typed FeaturePython)
  Dunit = g/cm3
  Dvalue = 2.52
  Group = -> [B_element001,C_element017]
  conduct = 2
  density = 1
  expand = 3
  formula = G4_BORON_CARBIDE
  name = G4_BORON_CARBIDE
  specific = 4
FEATURE [App::DocumentObjectGroupPython] B_element002  label="B_element : 2"  # scripted group (container) (typed FeaturePython)
  n = 2
  ref = B_element
FEATURE [App::DocumentObjectGroupPython] O_element016  label="O_element : 006"  # scripted group (container) (typed FeaturePython)
  n = 3
  ref = O_element
FEATURE [App::DocumentObjectGroupPython] G4_BORON_OXIDE  # scripted group (container) (typed FeaturePython)
  Dunit = g/cm3
  Dvalue = 1.812
  Group = -> [B_element002,O_element016]
  conduct = 2
  density = 1
  expand = 3
  formula = G4_BORON_OXIDE
  name = G4_BORON_OXIDE
  specific = 4
FEATURE [App::DocumentObjectGroupPython] H_element017  label="H_element : 0.107"  # scripted group (container) (typed FeaturePython)
  n = 0.107
FEATURE [App::DocumentObjectGroupPython] C_element018  label="C_element : 0.145"  # scripted group (container) (typed FeaturePython)
  n = 0.145
FEATURE [App::DocumentObjectGroupPython] N_element012  label="N_element : 0.022"  # scripted group (container) (typed FeaturePython)
  n = 0.022
FEATURE [App::DocumentObjectGroupPython] O_element017  label="O_element : 0.712"  # scripted group (container) (typed FeaturePython)
  n = 0.712
FEATURE [App::DocumentObjectGroupPython] Na_element004  label="Na_element : 0.004"  # scripted group (container) (typed FeaturePython)
  n = 0.002
FEATURE [App::DocumentObjectGroupPython] P_element004  label="P_element : 0.004"  # scripted group (container) (typed FeaturePython)
  n = 0.004
FEATURE [App::DocumentObjectGroupPython] S_element006  label="S_element : 0.005"  # scripted group (container) (typed FeaturePython)
  n = 0.002
FEATURE [App::DocumentObjectGroupPython] Cl_element003  label="Cl_element : 0.004"  # scripted group (container) (typed FeaturePython)
  n = 0.003
FEATURE [App::DocumentObjectGroupPython] K_element002  label="K_element : 0.003"  # scripted group (container) (typed FeaturePython)
  n = 0.003
FEATURE [App::DocumentObjectGroupPython] G4_BRAIN_ICRP  # scripted group (container) (typed FeaturePython)
  Dunit = g/cm3
  Dvalue = 1.04
  Group = -> [H_element017,C_element018,N_element012,O_element017,Na_element004,P_element004,S_element006,Cl_element003,K_element002]
  conduct = 2
  density = 1
  expand = 3
  formula = G4_BRAIN_ICRP
  name = G4_BRAIN_ICRP
  specific = 4
FEATURE [App::DocumentObjectGroupPython] C_element019  label="C_element : 4"  # scripted group (container) (typed FeaturePython)
  n = 4
  ref = C_element
FEATURE [App::DocumentObjectGroupPython] H_element018  label="H_element : 010"  # scripted group (container) (typed FeaturePython)
  n = 10
  ref = H_element
FEATURE [App::DocumentObjectGroupPython] G4_BUTANE  # scripted group (container) (typed FeaturePython)
  Dunit = g/cm3
  Dvalue = 0.00249343
  Group = -> [C_element019,H_element018]
  conduct = 2
  density = 1
  expand = 3
  formula = G4_BUTANE
  name = G4_BUTANE
  specific = 4
FEATURE [App::DocumentObjectGroupPython] C_element020  label="C_element : 008"  # scripted group (container) (typed FeaturePython)
  n = 4
  ref = C_element
FEATURE [App::DocumentObjectGroupPython] H_element019  label="H_element : 011"  # scripted group (container) (typed FeaturePython)
  n = 10
  ref = H_element
FEATURE [App::DocumentObjectGroupPython] O_element018  label="O_element : 007"  # scripted group (container) (typed FeaturePython)
  n = 1
  ref = O_element
FEATURE [App::DocumentObjectGroupPython] G4_N_BUTYL_ALCOHOL  label="G4_N-BUTYL_ALCOHOL"  # scripted group (container) (typed FeaturePython)
  Dunit = g/cm3
  Dvalue = 0.8098
  Group = -> [C_element020,H_element019,O_element018]
  conduct = 2
  density = 1
  expand = 3
  formula = G4_N-BUTYL_ALCOHOL
  name = G4_N-BUTYL_ALCOHOL
  specific = 4
FEATURE [App::DocumentObjectGroupPython] H_element020  label="H_element : 0.025"  # scripted group (container) (typed FeaturePython)
  n = 0.02468
FEATURE [App::DocumentObjectGroupPython] C_element021  label="C_element : 0.502"  # scripted group (container) (typed FeaturePython)
  n = 0.501611
FEATURE [App::DocumentObjectGroupPython] O_element019  label="O_element : 0.005"  # scripted group (container) (typed FeaturePython)
  n = 0.004527
FEATURE [App::DocumentObjectGroupPython] F_element004  label="F_element : 0.465"  # scripted group (container) (typed FeaturePython)
  n = 0.465209
FEATURE [App::DocumentObjectGroupPython] Si_element001  label="Si_element : 0.004"  # scripted group (container) (typed FeaturePython)
  n = 0.003973
FEATURE [App::DocumentObjectGroupPython] G4_C_552  label="G4_C-552"  # scripted group (container) (typed FeaturePython)
  Dunit = g/cm3
  Dvalue = 1.76
  Group = -> [H_element020,C_element021,O_element019,F_element004,Si_element001]
  conduct = 2
  density = 1
  expand = 3
  formula = G4_C-552
  name = G4_C-552
  specific = 4
FEATURE [App::DocumentObjectGroupPython] Cd_element001  label="Cd_element : 1"  # scripted group (container) (typed FeaturePython)
  n = 1
  ref = Cd_element
FEATURE [App::DocumentObjectGroupPython] Te_element001  label="Te_element : 1"  # scripted group (container) (typed FeaturePython)
  n = 1
  ref = Te_element
FEATURE [App::DocumentObjectGroupPython] G4_CADMIUM_TELLURIDE  # scripted group (container) (typed FeaturePython)
  Dunit = g/cm3
  Dvalue = 6.2
  Group = -> [Cd_element001,Te_element001]
  conduct = 2
  density = 1
  expand = 3
  formula = G4_CADMIUM_TELLURIDE
  name = G4_CADMIUM_TELLURIDE
  specific = 4
FEATURE [App::DocumentObjectGroupPython] Cd_element002  label="Cd_element : 002"  # scripted group (container) (typed FeaturePython)
  n = 1
  ref = Cd_element
FEATURE [App::DocumentObjectGroupPython] W_element001  label="W_element : 1"  # scripted group (container) (typed FeaturePython)
  n = 1
  ref = W_element
FEATURE [App::DocumentObjectGroupPython] O_element020  label="O_element : 008"  # scripted group (container) (typed FeaturePython)
  n = 4
  ref = O_element
FEATURE [App::DocumentObjectGroupPython] G4_CADMIUM_TUNGSTATE  # scripted group (container) (typed FeaturePython)
  Dunit = g/cm3
  Dvalue = 7.9
  Group = -> [Cd_element002,W_element001,O_element020]
  conduct = 2
  density = 1
  expand = 3
  formula = G4_CADMIUM_TUNGSTATE
  name = G4_CADMIUM_TUNGSTATE
  specific = 4
FEATURE [App::DocumentObjectGroupPython] Ca_element005  label="Ca_element : 1"  # scripted group (container) (typed FeaturePython)
  n = 1
  ref = Ca_element
FEATURE [App::DocumentObjectGroupPython] C_element022  label="C_element : 009"  # scripted group (container) (typed FeaturePython)
  n = 1
  ref = C_element
FEATURE [App::DocumentObjectGroupPython] O_element021  label="O_element : 009"  # scripted group (container) (typed FeaturePython)
  n = 3
  ref = O_element
FEATURE [App::DocumentObjectGroupPython] G4_CALCIUM_CARBONATE  # scripted group (container) (typed FeaturePython)
  Dunit = g/cm3
  Dvalue = 2.8
  Group = -> [Ca_element005,C_element022,O_element021]
  conduct = 2
  density = 1
  expand = 3
  formula = G4_CALCIUM_CARBONATE
  name = G4_CALCIUM_CARBONATE
  specific = 4
FEATURE [App::DocumentObjectGroupPython] Ca_element006  label="Ca_element : 002"  # scripted group (container) (typed FeaturePython)
  n = 1
  ref = Ca_element
FEATURE [App::DocumentObjectGroupPython] F_element005  label="F_element : 003"  # scripted group (container) (typed FeaturePython)
  n = 2
  ref = F_element
FEATURE [App::DocumentObjectGroupPython] G4_CALCIUM_FLUORIDE  # scripted group (container) (typed FeaturePython)
  Dunit = g/cm3
  Dvalue = 3.18
  Group = -> [Ca_element006,F_element005]
  conduct = 2
  density = 1
  expand = 3
  formula = G4_CALCIUM_FLUORIDE
  name = G4_CALCIUM_FLUORIDE
  specific = 4
FEATURE [App::DocumentObjectGroupPython] Ca_element007  label="Ca_element : 003"  # scripted group (container) (typed FeaturePython)
  n = 1
  ref = Ca_element
FEATURE [App::DocumentObjectGroupPython] O_element022  label="O_element : 010"  # scripted group (container) (typed FeaturePython)
  n = 1
  ref = O_element
FEATURE [App::DocumentObjectGroupPython] G4_CALCIUM_OXIDE  # scripted group (container) (typed FeaturePython)
  Dunit = g/cm3
  Dvalue = 3.3
  Group = -> [Ca_element007,O_element022]
  conduct = 2
  density = 1
  expand = 3
  formula = G4_CALCIUM_OXIDE
  name = G4_CALCIUM_OXIDE
  specific = 4
FEATURE [App::DocumentObjectGroupPython] Ca_element008  label="Ca_element : 004"  # scripted group (container) (typed FeaturePython)
  n = 1
  ref = Ca_element
FEATURE [App::DocumentObjectGroupPython] S_element007  label="S_element : 002"  # scripted group (container) (typed FeaturePython)
  n = 1
  ref = S_element
FEATURE [App::DocumentObjectGroupPython] O_element023  label="O_element : 011"  # scripted group (container) (typed FeaturePython)
  n = 4
  ref = O_element
FEATURE [App::DocumentObjectGroupPython] G4_CALCIUM_SULFATE  # scripted group (container) (typed FeaturePython)
  Dunit = g/cm3
  Dvalue = 2.96
  Group = -> [Ca_element008,S_element007,O_element023]
  conduct = 2
  density = 1
  expand = 3
  formula = G4_CALCIUM_SULFATE
  name = G4_CALCIUM_SULFATE
  specific = 4
FEATURE [App::DocumentObjectGroupPython] Ca_element009  label="Ca_element : 005"  # scripted group (container) (typed FeaturePython)
  n = 1
  ref = Ca_element
FEATURE [App::DocumentObjectGroupPython] W_element002  label="W_element : 002"  # scripted group (container) (typed FeaturePython)
  n = 1
  ref = W_element
FEATURE [App::DocumentObjectGroupPython] O_element024  label="O_element : 012"  # scripted group (container) (typed FeaturePython)
  n = 4
  ref = O_element
FEATURE [App::DocumentObjectGroupPython] G4_CALCIUM_TUNGSTATE  # scripted group (container) (typed FeaturePython)
  Dunit = g/cm3
  Dvalue = 6.062
  Group = -> [Ca_element009,W_element002,O_element024]
  conduct = 2
  density = 1
  expand = 3
  formula = G4_CALCIUM_TUNGSTATE
  name = G4_CALCIUM_TUNGSTATE
  specific = 4
FEATURE [App::DocumentObjectGroupPython] C_element023  label="C_element : 010"  # scripted group (container) (typed FeaturePython)
  n = 1
  ref = C_element
FEATURE [App::DocumentObjectGroupPython] O_element025  label="O_element : 013"  # scripted group (container) (typed FeaturePython)
  n = 2
  ref = O_element
FEATURE [App::DocumentObjectGroupPython] G4_CARBON_DIOXIDE  # scripted group (container) (typed FeaturePython)
  Dunit = g/cm3
  Dvalue = 0.00184212
  Group = -> [C_element023,O_element025]
  conduct = 2
  density = 1
  expand = 3
  formula = G4_CARBON_DIOXIDE
  name = G4_CARBON_DIOXIDE
  specific = 4
FEATURE [App::DocumentObjectGroupPython] C_element024  label="C_element : 011"  # scripted group (container) (typed FeaturePython)
  n = 1
  ref = C_element
FEATURE [App::DocumentObjectGroupPython] Cl_element004  label="Cl_element : 4"  # scripted group (container) (typed FeaturePython)
  n = 4
  ref = Cl_element
FEATURE [App::DocumentObjectGroupPython] G4_CARBON_TETRACHLORIDE  # scripted group (container) (typed FeaturePython)
  Dunit = g/cm3
  Dvalue = 1.594
  Group = -> [C_element024,Cl_element004]
  conduct = 2
  density = 1
  expand = 3
  formula = G4_CARBON_TETRACHLORIDE
  name = G4_CARBON_TETRACHLORIDE
  specific = 4
FEATURE [App::DocumentObjectGroupPython] C_element025  label="C_element : 012"  # scripted group (container) (typed FeaturePython)
  n = 6
  ref = C_element
FEATURE [App::DocumentObjectGroupPython] H_element021  label="H_element : 012"  # scripted group (container) (typed FeaturePython)
  n = 10
  ref = H_element
FEATURE [App::DocumentObjectGroupPython] O_element026  label="O_element : 5"  # scripted group (container) (typed FeaturePython)
  n = 5
  ref = O_element
FEATURE [App::DocumentObjectGroupPython] G4_CELLULOSE_CELLOPHANE  # scripted group (container) (typed FeaturePython)
  Dunit = g/cm3
  Dvalue = 1.42
  Group = -> [C_element025,H_element021,O_element026]
  conduct = 2
  density = 1
  expand = 3
  formula = G4_CELLULOSE_CELLOPHANE
  name = G4_CELLULOSE_CELLOPHANE
  specific = 4
FEATURE [App::DocumentObjectGroupPython] H_element022  label="H_element : 0.067"  # scripted group (container) (typed FeaturePython)
  n = 0.067125
FEATURE [App::DocumentObjectGroupPython] C_element026  label="C_element : 0.545"  # scripted group (container) (typed FeaturePython)
  n = 0.545403
FEATURE [App::DocumentObjectGroupPython] O_element027  label="O_element : 0.387"  # scripted group (container) (typed FeaturePython)
  n = 0.387472
FEATURE [App::DocumentObjectGroupPython] G4_CELLULOSE_BUTYRATE  # scripted group (container) (typed FeaturePython)
  Dunit = g/cm3
  Dvalue = 1.2
  Group = -> [H_element022,C_element026,O_element027]
  conduct = 2
  density = 1
  expand = 3
  formula = G4_CELLULOSE_BUTYRATE
  name = G4_CELLULOSE_BUTYRATE
  specific = 4
FEATURE [App::DocumentObjectGroupPython] H_element023  label="H_element : 0.029"  # scripted group (container) (typed FeaturePython)
  n = 0.029216
FEATURE [App::DocumentObjectGroupPython] C_element027  label="C_element : 0.271"  # scripted group (container) (typed FeaturePython)
  n = 0.271296
FEATURE [App::DocumentObjectGroupPython] N_element013  label="N_element : 0.121"  # scripted group (container) (typed FeaturePython)
  n = 0.121276
FEATURE [App::DocumentObjectGroupPython] O_element028  label="O_element : 0.578"  # scripted group (container) (typed FeaturePython)
  n = 0.578212
FEATURE [App::DocumentObjectGroupPython] G4_CELLULOSE_NITRATE  # scripted group (container) (typed FeaturePython)
  Dunit = g/cm3
  Dvalue = 1.49
  Group = -> [H_element023,C_element027,N_element013,O_element028]
  conduct = 2
  density = 1
  expand = 3
  formula = G4_CELLULOSE_NITRATE
  name = G4_CELLULOSE_NITRATE
  specific = 4
FEATURE [App::DocumentObjectGroupPython] H_element024  label="H_element : 0.108"  # scripted group (container) (typed FeaturePython)
  n = 0.107596
FEATURE [App::DocumentObjectGroupPython] N_element014  label="N_element : 0.001"  # scripted group (container) (typed FeaturePython)
  n = 0.0008
FEATURE [App::DocumentObjectGroupPython] O_element029  label="O_element : 0.875"  # scripted group (container) (typed FeaturePython)
  n = 0.874976
FEATURE [App::DocumentObjectGroupPython] S_element008  label="S_element : 0.015"  # scripted group (container) (typed FeaturePython)
  n = 0.014627
FEATURE [App::DocumentObjectGroupPython] Ce_element001  label="Ce_element : 0.002"  # scripted group (container) (typed FeaturePython)
  n = 0.002001
FEATURE [App::DocumentObjectGroupPython] G4_CERIC_SULFATE  # scripted group (container) (typed FeaturePython)
  Dunit = g/cm3
  Dvalue = 1.03
  Group = -> [H_element024,N_element014,O_element029,S_element008,Ce_element001]
  conduct = 2
  density = 1
  expand = 3
  formula = G4_CERIC_SULFATE
  name = G4_CERIC_SULFATE
  specific = 4
FEATURE [App::DocumentObjectGroupPython] Cs_element001  label="Cs_element : 1"  # scripted group (container) (typed FeaturePython)
  n = 1
  ref = Cs_element
FEATURE [App::DocumentObjectGroupPython] F_element006  label="F_element : 1"  # scripted group (container) (typed FeaturePython)
  n = 1
  ref = F_element
FEATURE [App::DocumentObjectGroupPython] G4_CESIUM_FLUORIDE  # scripted group (container) (typed FeaturePython)
  Dunit = g/cm3
  Dvalue = 4.115
  Group = -> [Cs_element001,F_element006]
  conduct = 2
  density = 1
  expand = 3
  formula = G4_CESIUM_FLUORIDE
  name = G4_CESIUM_FLUORIDE
  specific = 4
FEATURE [App::DocumentObjectGroupPython] Cs_element002  label="Cs_element : 002"  # scripted group (container) (typed FeaturePython)
  n = 1
  ref = Cs_element
FEATURE [App::DocumentObjectGroupPython] I_element001  label="I_element : 1"  # scripted group (container) (typed FeaturePython)
  n = 1
  ref = I_element
FEATURE [App::DocumentObjectGroupPython] G4_CESIUM_IODIDE  # scripted group (container) (typed FeaturePython)
  Dunit = g/cm3
  Dvalue = 4.51
  Group = -> [Cs_element002,I_element001]
  conduct = 2
  density = 1
  expand = 3
  formula = G4_CESIUM_IODIDE
  name = G4_CESIUM_IODIDE
  specific = 4
FEATURE [App::DocumentObjectGroupPython] C_element028  label="C_element : 013"  # scripted group (container) (typed FeaturePython)
  n = 6
  ref = C_element
FEATURE [App::DocumentObjectGroupPython] H_element025  label="H_element : 013"  # scripted group (container) (typed FeaturePython)
  n = 5
  ref = H_element
FEATURE [App::DocumentObjectGroupPython] Cl_element005  label="Cl_element : 1"  # scripted group (container) (typed FeaturePython)
  n = 1
  ref = Cl_element
FEATURE [App::DocumentObjectGroupPython] G4_CHLOROBENZENE  # scripted group (container) (typed FeaturePython)
  Dunit = g/cm3
  Dvalue = 1.1058
  Group = -> [C_element028,H_element025,Cl_element005]
  conduct = 2
  density = 1
  expand = 3
  formula = G4_CHLOROBENZENE
  name = G4_CHLOROBENZENE
  specific = 4
FEATURE [App::DocumentObjectGroupPython] C_element029  label="C_element : 014"  # scripted group (container) (typed FeaturePython)
  n = 1
  ref = C_element
FEATURE [App::DocumentObjectGroupPython] H_element026  label="H_element : 1"  # scripted group (container) (typed FeaturePython)
  n = 1
  ref = H_element
FEATURE [App::DocumentObjectGroupPython] Cl_element006  label="Cl_element : 3"  # scripted group (container) (typed FeaturePython)
  n = 3
  ref = Cl_element
FEATURE [App::DocumentObjectGroupPython] G4_CHLOROFORM  # scripted group (container) (typed FeaturePython)
  Dunit = g/cm3
  Dvalue = 1.4832
  Group = -> [C_element029,H_element026,Cl_element006]
  conduct = 2
  density = 1
  expand = 3
  formula = G4_CHLOROFORM
  name = G4_CHLOROFORM
  specific = 4
FEATURE [App::DocumentObjectGroupPython] H_element027  label="H_element : 0.010"  # scripted group (container) (typed FeaturePython)
  n = 0.01
FEATURE [App::DocumentObjectGroupPython] C_element030  label="C_element : 0.001"  # scripted group (container) (typed FeaturePython)
  n = 0.001
FEATURE [App::DocumentObjectGroupPython] O_element030  label="O_element : 0.529"  # scripted group (container) (typed FeaturePython)
  n = 0.529107
FEATURE [App::DocumentObjectGroupPython] Na_element005  label="Na_element : 0.016"  # scripted group (container) (typed FeaturePython)
  n = 0.016
FEATURE [App::DocumentObjectGroupPython] Mg_element003  label="Mg_element : 0.004"  # scripted group (container) (typed FeaturePython)
  n = 0.002
FEATURE [App::DocumentObjectGroupPython] Al_element002  label="Al_element : 0.034"  # scripted group (container) (typed FeaturePython)
  n = 0.033872
FEATURE [App::DocumentObjectGroupPython] Si_element002  label="Si_element : 0.337"  # scripted group (container) (typed FeaturePython)
  n = 0.337021
FEATURE [App::DocumentObjectGroupPython] K_element003  label="K_element : 0.013"  # scripted group (container) (typed FeaturePython)
  n = 0.013
FEATURE [App::DocumentObjectGroupPython] Ca_element010  label="Ca_element : 0.044"  # scripted group (container) (typed FeaturePython)
  n = 0.044
FEATURE [App::DocumentObjectGroupPython] Fe_element002  label="Fe_element : 0.014"  # scripted group (container) (typed FeaturePython)
  n = 0.014
FEATURE [App::DocumentObjectGroupPython] G4_CONCRETE  # scripted group (container) (typed FeaturePython)
  Dunit = g/cm3
  Dvalue = 2.3
  Group = -> [H_element027,C_element030,O_element030,Na_element005,Mg_element003,Al_element002,Si_element002,K_element003,Ca_element010,Fe_element002]
  conduct = 2
  density = 1
  expand = 3
  formula = G4_CONCRETE
  name = G4_CONCRETE
  specific = 4
FEATURE [App::DocumentObjectGroupPython] C_element031  label="C_element : 015"  # scripted group (container) (typed FeaturePython)
  n = 6
  ref = C_element
FEATURE [App::DocumentObjectGroupPython] H_element028  label="H_element : 12"  # scripted group (container) (typed FeaturePython)
  n = 12
  ref = H_element
FEATURE [App::DocumentObjectGroupPython] G4_CYCLOHEXANE  # scripted group (container) (typed FeaturePython)
  Dunit = g/cm3
  Dvalue = 0.779
  Group = -> [C_element031,H_element028]
  conduct = 2
  density = 1
  expand = 3
  formula = G4_CYCLOHEXANE
  name = G4_CYCLOHEXANE
  specific = 4
FEATURE [App::DocumentObjectGroupPython] C_element032  label="C_element : 016"  # scripted group (container) (typed FeaturePython)
  n = 6
  ref = C_element
FEATURE [App::DocumentObjectGroupPython] H_element029  label="H_element : 4"  # scripted group (container) (typed FeaturePython)
  n = 4
  ref = H_element
FEATURE [App::DocumentObjectGroupPython] Cl_element007  label="Cl_element : 2"  # scripted group (container) (typed FeaturePython)
  n = 2
  ref = Cl_element
FEATURE [App::DocumentObjectGroupPython] G4_1_2_DICHLOROBENZENE  label="G4_1.2-DICHLOROBENZENE"  # scripted group (container) (typed FeaturePython)
  Dunit = g/cm3
  Dvalue = 1.3048
  Group = -> [C_element032,H_element029,Cl_element007]
  conduct = 2
  density = 1
  expand = 3
  formula = G4_1.2-DICHLOROBENZENE
  name = G4_1.2-DICHLOROBENZENE
  specific = 4
FEATURE [App::DocumentObjectGroupPython] C_element033  label="C_element : 017"  # scripted group (container) (typed FeaturePython)
  n = 4
  ref = C_element
FEATURE [App::DocumentObjectGroupPython] H_element030  label="H_element : 8"  # scripted group (container) (typed FeaturePython)
  n = 8
  ref = H_element
FEATURE [App::DocumentObjectGroupPython] O_element031  label="O_element : 014"  # scripted group (container) (typed FeaturePython)
  n = 1
  ref = O_element
FEATURE [App::DocumentObjectGroupPython] Cl_element008  label="Cl_element : 005"  # scripted group (container) (typed FeaturePython)
  n = 2
  ref = Cl_element
FEATURE [App::DocumentObjectGroupPython] G4_DICHLORODIETHYL_ETHER  # scripted group (container) (typed FeaturePython)
  Dunit = g/cm3
  Dvalue = 1.2199
  Group = -> [C_element033,H_element030,O_element031,Cl_element008]
  conduct = 2
  density = 1
  expand = 3
  formula = G4_DICHLORODIETHYL_ETHER
  name = G4_DICHLORODIETHYL_ETHER
  specific = 4
FEATURE [App::DocumentObjectGroupPython] C_element034  label="C_element : 018"  # scripted group (container) (typed FeaturePython)
  n = 2
  ref = C_element
FEATURE [App::DocumentObjectGroupPython] H_element031  label="H_element : 014"  # scripted group (container) (typed FeaturePython)
  n = 4
  ref = H_element
FEATURE [App::DocumentObjectGroupPython] Cl_element009  label="Cl_element : 006"  # scripted group (container) (typed FeaturePython)
  n = 2
  ref = Cl_element
FEATURE [App::DocumentObjectGroupPython] G4_1_2_DICHLOROETHANE  label="G4_1.2-DICHLOROETHANE"  # scripted group (container) (typed FeaturePython)
  Dunit = g/cm3
  Dvalue = 1.2351
  Group = -> [C_element034,H_element031,Cl_element009]
  conduct = 2
  density = 1
  expand = 3
  formula = G4_1.2-DICHLOROETHANE
  name = G4_1.2-DICHLOROETHANE
  specific = 4
FEATURE [App::DocumentObjectGroupPython] C_element035  label="C_element : 019"  # scripted group (container) (typed FeaturePython)
  n = 4
  ref = C_element
FEATURE [App::DocumentObjectGroupPython] H_element032  label="H_element : 015"  # scripted group (container) (typed FeaturePython)
  n = 10
  ref = H_element
FEATURE [App::DocumentObjectGroupPython] O_element032  label="O_element : 015"  # scripted group (container) (typed FeaturePython)
  n = 1
  ref = O_element
FEATURE [App::DocumentObjectGroupPython] G4_DIETHYL_ETHER  # scripted group (container) (typed FeaturePython)
  Dunit = g/cm3
  Dvalue = 0.71378
  Group = -> [C_element035,H_element032,O_element032]
  conduct = 2
  density = 1
  expand = 3
  formula = G4_DIETHYL_ETHER
  name = G4_DIETHYL_ETHER
  specific = 4
FEATURE [App::DocumentObjectGroupPython] C_element036  label="C_element : 020"  # scripted group (container) (typed FeaturePython)
  n = 3
  ref = C_element
FEATURE [App::DocumentObjectGroupPython] H_element033  label="H_element : 016"  # scripted group (container) (typed FeaturePython)
  n = 7
  ref = H_element
FEATURE [App::DocumentObjectGroupPython] N_element015  label="N_element : 008"  # scripted group (container) (typed FeaturePython)
  n = 1
  ref = N_element
FEATURE [App::DocumentObjectGroupPython] O_element033  label="O_element : 016"  # scripted group (container) (typed FeaturePython)
  n = 1
  ref = O_element
FEATURE [App::DocumentObjectGroupPython] G4_N_N_DIMETHYL_FORMAMIDE  label="G4_N.N-DIMETHYL_FORMAMIDE"  # scripted group (container) (typed FeaturePython)
  Dunit = g/cm3
  Dvalue = 0.9487
  Group = -> [C_element036,H_element033,N_element015,O_element033]
  conduct = 2
  density = 1
  expand = 3
  formula = G4_N.N-DIMETHYL_FORMAMIDE
  name = G4_N.N-DIMETHYL_FORMAMIDE
  specific = 4
FEATURE [App::DocumentObjectGroupPython] C_element037  label="C_element : 021"  # scripted group (container) (typed FeaturePython)
  n = 2
  ref = C_element
FEATURE [App::DocumentObjectGroupPython] H_element034  label="H_element : 017"  # scripted group (container) (typed FeaturePython)
  n = 6
  ref = H_element
FEATURE [App::DocumentObjectGroupPython] O_element034  label="O_element : 017"  # scripted group (container) (typed FeaturePython)
  n = 1
  ref = O_element
FEATURE [App::DocumentObjectGroupPython] S_element009  label="S_element : 003"  # scripted group (container) (typed FeaturePython)
  n = 1
  ref = S_element
FEATURE [App::DocumentObjectGroupPython] G4_DIMETHYL_SULFOXIDE  # scripted group (container) (typed FeaturePython)
  Dunit = g/cm3
  Dvalue = 1.1014
  Group = -> [C_element037,H_element034,O_element034,S_element009]
  conduct = 2
  density = 1
  expand = 3
  formula = G4_DIMETHYL_SULFOXIDE
  name = G4_DIMETHYL_SULFOXIDE
  specific = 4
FEATURE [App::DocumentObjectGroupPython] C_element038  label="C_element : 022"  # scripted group (container) (typed FeaturePython)
  n = 2
  ref = C_element
FEATURE [App::DocumentObjectGroupPython] H_element035  label="H_element : 018"  # scripted group (container) (typed FeaturePython)
  n = 6
  ref = H_element
FEATURE [App::DocumentObjectGroupPython] G4_ETHANE  # scripted group (container) (typed FeaturePython)
  Dunit = g/cm3
  Dvalue = 0.00125324
  Group = -> [C_element038,H_element035]
  conduct = 2
  density = 1
  expand = 3
  formula = G4_ETHANE
  name = G4_ETHANE
  specific = 4
FEATURE [App::DocumentObjectGroupPython] C_element039  label="C_element : 023"  # scripted group (container) (typed FeaturePython)
  n = 2
  ref = C_element
FEATURE [App::DocumentObjectGroupPython] H_element036  label="H_element : 019"  # scripted group (container) (typed FeaturePython)
  n = 6
  ref = H_element
FEATURE [App::DocumentObjectGroupPython] O_element035  label="O_element : 018"  # scripted group (container) (typed FeaturePython)
  n = 1
  ref = O_element
FEATURE [App::DocumentObjectGroupPython] G4_ETHYL_ALCOHOL  # scripted group (container) (typed FeaturePython)
  Dunit = g/cm3
  Dvalue = 0.7893
  Group = -> [C_element039,H_element036,O_element035]
  conduct = 2
  density = 1
  expand = 3
  formula = G4_ETHYL_ALCOHOL
  name = G4_ETHYL_ALCOHOL
  specific = 4
FEATURE [App::DocumentObjectGroupPython] H_element037  label="H_element : 0.090"  # scripted group (container) (typed FeaturePython)
  n = 0.090027
FEATURE [App::DocumentObjectGroupPython] C_element040  label="C_element : 0.585"  # scripted group (container) (typed FeaturePython)
  n = 0.585182
FEATURE [App::DocumentObjectGroupPython] O_element036  label="O_element : 0.325"  # scripted group (container) (typed FeaturePython)
  n = 0.324791
FEATURE [App::DocumentObjectGroupPython] G4_ETHYL_CELLULOSE  # scripted group (container) (typed FeaturePython)
  Dunit = g/cm3
  Dvalue = 1.13
  Group = -> [H_element037,C_element040,O_element036]
  conduct = 2
  density = 1
  expand = 3
  formula = G4_ETHYL_CELLULOSE
  name = G4_ETHYL_CELLULOSE
  specific = 4
FEATURE [App::DocumentObjectGroupPython] C_element041  label="C_element : 024"  # scripted group (container) (typed FeaturePython)
  n = 2
  ref = C_element
FEATURE [App::DocumentObjectGroupPython] H_element038  label="H_element : 020"  # scripted group (container) (typed FeaturePython)
  n = 4
  ref = H_element
FEATURE [App::DocumentObjectGroupPython] G4_ETHYLENE  # scripted group (container) (typed FeaturePython)
  Dunit = g/cm3
  Dvalue = 0.00117497
  Group = -> [C_element041,H_element038]
  conduct = 2
  density = 1
  expand = 3
  formula = G4_ETHYLENE
  name = G4_ETHYLENE
  specific = 4
FEATURE [App::DocumentObjectGroupPython] H_element039  label="H_element : 0.096"  # scripted group (container) (typed FeaturePython)
  n = 0.096
FEATURE [App::DocumentObjectGroupPython] C_element042  label="C_element : 0.195"  # scripted group (container) (typed FeaturePython)
  n = 0.195
FEATURE [App::DocumentObjectGroupPython] N_element016  label="N_element : 0.057"  # scripted group (container) (typed FeaturePython)
  n = 0.057
FEATURE [App::DocumentObjectGroupPython] O_element037  label="O_element : 0.646"  # scripted group (container) (typed FeaturePython)
  n = 0.646
FEATURE [App::DocumentObjectGroupPython] Na_element006  label="Na_element : 0.017"  # scripted group (container) (typed FeaturePython)
  n = 0.001
FEATURE [App::DocumentObjectGroupPython] P_element005  label="P_element : 0.104"  # scripted group (container) (typed FeaturePython)
  n = 0.001
FEATURE [App::DocumentObjectGroupPython] S_element010  label="S_element : 0.016"  # scripted group (container) (typed FeaturePython)
  n = 0.003
FEATURE [App::DocumentObjectGroupPython] Cl_element010  label="Cl_element : 0.005"  # scripted group (container) (typed FeaturePython)
  n = 0.001
FEATURE [App::DocumentObjectGroupPython] G4_EYE_LENS_ICRP  # scripted group (container) (typed FeaturePython)
  Dunit = g/cm3
  Dvalue = 1.07
  Group = -> [H_element039,C_element042,N_element016,O_element037,Na_element006,P_element005,S_element010,Cl_element010]
  conduct = 2
  density = 1
  expand = 3
  formula = G4_EYE_LENS_ICRP
  name = G4_EYE_LENS_ICRP
  specific = 4
FEATURE [App::DocumentObjectGroupPython] Fe_element003  label="Fe_element : 2"  # scripted group (container) (typed FeaturePython)
  n = 2
  ref = Fe_element
FEATURE [App::DocumentObjectGroupPython] O_element038  label="O_element : 019"  # scripted group (container) (typed FeaturePython)
  n = 3
  ref = O_element
FEATURE [App::DocumentObjectGroupPython] G4_FERRIC_OXIDE  # scripted group (container) (typed FeaturePython)
  Dunit = g/cm3
  Dvalue = 5.2
  Group = -> [Fe_element003,O_element038]
  conduct = 2
  density = 1
  expand = 3
  formula = G4_FERRIC_OXIDE
  name = G4_FERRIC_OXIDE
  specific = 4
FEATURE [App::DocumentObjectGroupPython] Fe_element004  label="Fe_element : 1"  # scripted group (container) (typed FeaturePython)
  n = 1
  ref = Fe_element
FEATURE [App::DocumentObjectGroupPython] B_element003  label="B_element : 1"  # scripted group (container) (typed FeaturePython)
  n = 1
  ref = B_element
FEATURE [App::DocumentObjectGroupPython] G4_FERROBORIDE  # scripted group (container) (typed FeaturePython)
  Dunit = g/cm3
  Dvalue = 7.15
  Group = -> [Fe_element004,B_element003]
  conduct = 2
  density = 1
  expand = 3
  formula = G4_FERROBORIDE
  name = G4_FERROBORIDE
  specific = 4
FEATURE [App::DocumentObjectGroupPython] Fe_element005  label="Fe_element : 003"  # scripted group (container) (typed FeaturePython)
  n = 1
  ref = Fe_element
FEATURE [App::DocumentObjectGroupPython] O_element039  label="O_element : 020"  # scripted group (container) (typed FeaturePython)
  n = 1
  ref = O_element
FEATURE [App::DocumentObjectGroupPython] G4_FERROUS_OXIDE  # scripted group (container) (typed FeaturePython)
  Dunit = g/cm3
  Dvalue = 5.7
  Group = -> [Fe_element005,O_element039]
  conduct = 2
  density = 1
  expand = 3
  formula = G4_FERROUS_OXIDE
  name = G4_FERROUS_OXIDE
  specific = 4
FEATURE [App::DocumentObjectGroupPython] H_element040  label="H_element : 0.115"  # scripted group (container) (typed FeaturePython)
  n = 0.108259
FEATURE [App::DocumentObjectGroupPython] N_element017  label="N_element : 0.000"  # scripted group (container) (typed FeaturePython)
  n = 2.7e-05
FEATURE [App::DocumentObjectGroupPython] O_element040  label="O_element : 0.879"  # scripted group (container) (typed FeaturePython)
  n = 0.878636
FEATURE [App::DocumentObjectGroupPython] Na_element007  label="Na_element : 0.000"  # scripted group (container) (typed FeaturePython)
  n = 2.2e-05
FEATURE [App::DocumentObjectGroupPython] S_element011  label="S_element : 0.013"  # scripted group (container) (typed FeaturePython)
  n = 0.012968
FEATURE [App::DocumentObjectGroupPython] Cl_element011  label="Cl_element : 0.000"  # scripted group (container) (typed FeaturePython)
  n = 3.4e-05
FEATURE [App::DocumentObjectGroupPython] Fe_element006  label="Fe_element : 0.000"  # scripted group (container) (typed FeaturePython)
  n = 5.4e-05
FEATURE [App::DocumentObjectGroupPython] G4_FERROUS_SULFATE  # scripted group (container) (typed FeaturePython)
  Dunit = g/cm3
  Dvalue = 1.024
  Group = -> [H_element040,N_element017,O_element040,Na_element007,S_element011,Cl_element011,Fe_element006]
  conduct = 2
  density = 1
  expand = 3
  formula = G4_FERROUS_SULFATE
  name = G4_FERROUS_SULFATE
  specific = 4
FEATURE [App::DocumentObjectGroupPython] C_element043  label="C_element : 0.099"  # scripted group (container) (typed FeaturePython)
  n = 0.099335
FEATURE [App::DocumentObjectGroupPython] F_element007  label="F_element : 0.314"  # scripted group (container) (typed FeaturePython)
  n = 0.314247
FEATURE [App::DocumentObjectGroupPython] Cl_element012  label="Cl_element : 0.586"  # scripted group (container) (typed FeaturePython)
  n = 0.586418
FEATURE [App::DocumentObjectGroupPython] G4_FREON_12  label="G4_FREON-12"  # scripted group (container) (typed FeaturePython)
  Dunit = g/cm3
  Dvalue = 1.12
  Group = -> [C_element043,F_element007,Cl_element012]
  conduct = 2
  density = 1
  expand = 3
  formula = G4_FREON-12
  name = G4_FREON-12
  specific = 4
FEATURE [App::DocumentObjectGroupPython] C_element044  label="C_element : 0.057"  # scripted group (container) (typed FeaturePython)
  n = 0.057245
FEATURE [App::DocumentObjectGroupPython] F_element008  label="F_element : 0.181"  # scripted group (container) (typed FeaturePython)
  n = 0.181096
FEATURE [App::DocumentObjectGroupPython] Br_element001  label="Br_element : 0.762"  # scripted group (container) (typed FeaturePython)
  n = 0.761659
FEATURE [App::DocumentObjectGroupPython] G4_FREON_12B2  label="G4_FREON-12B2"  # scripted group (container) (typed FeaturePython)
  Dunit = g/cm3
  Dvalue = 1.8
  Group = -> [C_element044,F_element008,Br_element001]
  conduct = 2
  density = 1
  expand = 3
  formula = G4_FREON-12B2
  name = G4_FREON-12B2
  specific = 4
FEATURE [App::DocumentObjectGroupPython] C_element045  label="C_element : 0.115"  # scripted group (container) (typed FeaturePython)
  n = 0.114983
FEATURE [App::DocumentObjectGroupPython] F_element009  label="F_element : 0.546"  # scripted group (container) (typed FeaturePython)
  n = 0.545621
FEATURE [App::DocumentObjectGroupPython] Cl_element013  label="Cl_element : 0.339"  # scripted group (container) (typed FeaturePython)
  n = 0.339396
FEATURE [App::DocumentObjectGroupPython] G4_FREON_13  label="G4_FREON-13"  # scripted group (container) (typed FeaturePython)
  Dunit = g/cm3
  Dvalue = 0.95
  Group = -> [C_element045,F_element009,Cl_element013]
  conduct = 2
  density = 1
  expand = 3
  formula = G4_FREON-13
  name = G4_FREON-13
  specific = 4
FEATURE [App::DocumentObjectGroupPython] C_element046  label="C_element : 025"  # scripted group (container) (typed FeaturePython)
  n = 1
  ref = C_element
FEATURE [App::DocumentObjectGroupPython] F_element010  label="F_element : 3"  # scripted group (container) (typed FeaturePython)
  n = 3
  ref = F_element
FEATURE [App::DocumentObjectGroupPython] Br_element002  label="Br_element : 1"  # scripted group (container) (typed FeaturePython)
  n = 1
  ref = Br_element
FEATURE [App::DocumentObjectGroupPython] G4_FREON_13B1  label="G4_FREON-13B1"  # scripted group (container) (typed FeaturePython)
  Dunit = g/cm3
  Dvalue = 1.5
  Group = -> [C_element046,F_element010,Br_element002]
  conduct = 2
  density = 1
  expand = 3
  formula = G4_FREON-13B1
  name = G4_FREON-13B1
  specific = 4
FEATURE [App::DocumentObjectGroupPython] C_element047  label="C_element : 0.061"  # scripted group (container) (typed FeaturePython)
  n = 0.061309
FEATURE [App::DocumentObjectGroupPython] F_element011  label="F_element : 0.291"  # scripted group (container) (typed FeaturePython)
  n = 0.290924
FEATURE [App::DocumentObjectGroupPython] I_element002  label="I_element : 0.648"  # scripted group (container) (typed FeaturePython)
  n = 0.647767
FEATURE [App::DocumentObjectGroupPython] G4_FREON_13I1  label="G4_FREON-13I1"  # scripted group (container) (typed FeaturePython)
  Dunit = g/cm3
  Dvalue = 1.8
  Group = -> [C_element047,F_element011,I_element002]
  conduct = 2
  density = 1
  expand = 3
  formula = G4_FREON-13I1
  name = G4_FREON-13I1
  specific = 4
FEATURE [App::DocumentObjectGroupPython] Gd_element001  label="Gd_element : 2"  # scripted group (container) (typed FeaturePython)
  n = 2
  ref = Gd_element
FEATURE [App::DocumentObjectGroupPython] O_element041  label="O_element : 021"  # scripted group (container) (typed FeaturePython)
  n = 2
  ref = O_element
FEATURE [App::DocumentObjectGroupPython] S_element012  label="S_element : 004"  # scripted group (container) (typed FeaturePython)
  n = 1
  ref = S_element
FEATURE [App::DocumentObjectGroupPython] G4_GADOLINIUM_OXYSULFIDE  # scripted group (container) (typed FeaturePython)
  Dunit = g/cm3
  Dvalue = 7.44
  Group = -> [Gd_element001,O_element041,S_element012]
  conduct = 2
  density = 1
  expand = 3
  formula = G4_GADOLINIUM_OXYSULFIDE
  name = G4_GADOLINIUM_OXYSULFIDE
  specific = 4
FEATURE [App::DocumentObjectGroupPython] Ga_element001  label="Ga_element : 1"  # scripted group (container) (typed FeaturePython)
  n = 1
  ref = Ga_element
FEATURE [App::DocumentObjectGroupPython] As_element001  label="As_element : 1"  # scripted group (container) (typed FeaturePython)
  n = 1
  ref = As_element
FEATURE [App::DocumentObjectGroupPython] G4_GALLIUM_ARSENIDE  # scripted group (container) (typed FeaturePython)
  Dunit = g/cm3
  Dvalue = 5.31
  Group = -> [Ga_element001,As_element001]
  conduct = 2
  density = 1
  expand = 3
  formula = G4_GALLIUM_ARSENIDE
  name = G4_GALLIUM_ARSENIDE
  specific = 4
FEATURE [App::DocumentObjectGroupPython] H_element041  label="H_element : 0.081"  # scripted group (container) (typed FeaturePython)
  n = 0.08118
FEATURE [App::DocumentObjectGroupPython] C_element048  label="C_element : 0.416"  # scripted group (container) (typed FeaturePython)
  n = 0.41606
FEATURE [App::DocumentObjectGroupPython] N_element018  label="N_element : 0.111"  # scripted group (container) (typed FeaturePython)
  n = 0.11124
FEATURE [App::DocumentObjectGroupPython] O_element042  label="O_element : 0.381"  # scripted group (container) (typed FeaturePython)
  n = 0.38064
FEATURE [App::DocumentObjectGroupPython] S_element013  label="S_element : 0.011"  # scripted group (container) (typed FeaturePython)
  n = 0.01088
FEATURE [App::DocumentObjectGroupPython] G4_GEL_PHOTO_EMULSION  # scripted group (container) (typed FeaturePython)
  Dunit = g/cm3
  Dvalue = 1.2914
  Group = -> [H_element041,C_element048,N_element018,O_element042,S_element013]
  conduct = 2
  density = 1
  expand = 3
  formula = G4_GEL_PHOTO_EMULSION
  name = G4_GEL_PHOTO_EMULSION
  specific = 4
FEATURE [App::DocumentObjectGroupPython] B_element004  label="B_element : 0.040"  # scripted group (container) (typed FeaturePython)
  n = 0.0400639
FEATURE [App::DocumentObjectGroupPython] O_element043  label="O_element : 0.540"  # scripted group (container) (typed FeaturePython)
  n = 0.539561
FEATURE [App::DocumentObjectGroupPython] Na_element008  label="Na_element : 0.028"  # scripted group (container) (typed FeaturePython)
  n = 0.0281909
FEATURE [App::DocumentObjectGroupPython] Al_element003  label="Al_element : 0.012"  # scripted group (container) (typed FeaturePython)
  n = 0.011644
FEATURE [App::DocumentObjectGroupPython] Si_element003  label="Si_element : 0.377"  # scripted group (container) (typed FeaturePython)
  n = 0.377219
FEATURE [App::DocumentObjectGroupPython] K_element004  label="K_element : 0.014"  # scripted group (container) (typed FeaturePython)
  n = 0.00332099
FEATURE [App::DocumentObjectGroupPython] G4_Pyrex_Glass  # scripted group (container) (typed FeaturePython)
  Dunit = g/cm3
  Dvalue = 2.23
  Group = -> [B_element004,O_element043,Na_element008,Al_element003,Si_element003,K_element004]
  conduct = 2
  density = 1
  expand = 3
  formula = G4_Pyrex_Glass
  name = G4_Pyrex_Glass
  specific = 4
FEATURE [App::DocumentObjectGroupPython] O_element044  label="O_element : 0.156"  # scripted group (container) (typed FeaturePython)
  n = 0.156453
FEATURE [App::DocumentObjectGroupPython] Si_element004  label="Si_element : 0.081"  # scripted group (container) (typed FeaturePython)
  n = 0.080866
FEATURE [App::DocumentObjectGroupPython] Ti_element001  label="Ti_element : 0.008"  # scripted group (container) (typed FeaturePython)
  n = 0.008092
FEATURE [App::DocumentObjectGroupPython] As_element002  label="As_element : 0.003"  # scripted group (container) (typed FeaturePython)
  n = 0.002651
FEATURE [App::DocumentObjectGroupPython] Pb_element001  label="Pb_element : 0.752"  # scripted group (container) (typed FeaturePython)
  n = 0.751938
FEATURE [App::DocumentObjectGroupPython] G4_GLASS_LEAD  # scripted group (container) (typed FeaturePython)
  Dunit = g/cm3
  Dvalue = 6.22
  Group = -> [O_element044,Si_element004,Ti_element001,As_element002,Pb_element001]
  conduct = 2
  density = 1
  expand = 3
  formula = G4_GLASS_LEAD
  name = G4_GLASS_LEAD
  specific = 4
FEATURE [App::DocumentObjectGroupPython] O_element045  label="O_element : 0.460"  # scripted group (container) (typed FeaturePython)
  n = 0.4598
FEATURE [App::DocumentObjectGroupPython] Na_element009  label="Na_element : 0.096"  # scripted group (container) (typed FeaturePython)
  n = 0.0964411
FEATURE [App::DocumentObjectGroupPython] Si_element005  label="Si_element : 0.378"  # scripted group (container) (typed FeaturePython)
  n = 0.336553
FEATURE [App::DocumentObjectGroupPython] Ca_element011  label="Ca_element : 0.107"  # scripted group (container) (typed FeaturePython)
  n = 0.107205
FEATURE [App::DocumentObjectGroupPython] G4_GLASS_PLATE  # scripted group (container) (typed FeaturePython)
  Dunit = g/cm3
  Dvalue = 2.4
  Group = -> [O_element045,Na_element009,Si_element005,Ca_element011]
  conduct = 2
  density = 1
  expand = 3
  formula = G4_GLASS_PLATE
  name = G4_GLASS_PLATE
  specific = 4
FEATURE [App::DocumentObjectGroupPython] C_element049  label="C_element : 026"  # scripted group (container) (typed FeaturePython)
  n = 5
  ref = C_element
FEATURE [App::DocumentObjectGroupPython] H_element042  label="H_element : 021"  # scripted group (container) (typed FeaturePython)
  n = 10
  ref = H_element
FEATURE [App::DocumentObjectGroupPython] N_element019  label="N_element : 2"  # scripted group (container) (typed FeaturePython)
  n = 2
  ref = N_element
FEATURE [App::DocumentObjectGroupPython] O_element046  label="O_element : 022"  # scripted group (container) (typed FeaturePython)
  n = 3
  ref = O_element
FEATURE [App::DocumentObjectGroupPython] G4_GLUTAMINE  # scripted group (container) (typed FeaturePython)
  Dunit = g/cm3
  Dvalue = 1.46
  Group = -> [C_element049,H_element042,N_element019,O_element046]
  conduct = 2
  density = 1
  expand = 3
  formula = G4_GLUTAMINE
  name = G4_GLUTAMINE
  specific = 4
FEATURE [App::DocumentObjectGroupPython] C_element050  label="C_element : 027"  # scripted group (container) (typed FeaturePython)
  n = 3
  ref = C_element
FEATURE [App::DocumentObjectGroupPython] H_element043  label="H_element : 022"  # scripted group (container) (typed FeaturePython)
  n = 8
  ref = H_element
FEATURE [App::DocumentObjectGroupPython] O_element047  label="O_element : 023"  # scripted group (container) (typed FeaturePython)
  n = 3
  ref = O_element
FEATURE [App::DocumentObjectGroupPython] G4_GLYCEROL  # scripted group (container) (typed FeaturePython)
  Dunit = g/cm3
  Dvalue = 1.2613
  Group = -> [C_element050,H_element043,O_element047]
  conduct = 2
  density = 1
  expand = 3
  formula = G4_GLYCEROL
  name = G4_GLYCEROL
  specific = 4
FEATURE [App::DocumentObjectGroupPython] C_element051  label="C_element : 028"  # scripted group (container) (typed FeaturePython)
  n = 5
  ref = C_element
FEATURE [App::DocumentObjectGroupPython] H_element044  label="H_element : 023"  # scripted group (container) (typed FeaturePython)
  n = 5
  ref = H_element
FEATURE [App::DocumentObjectGroupPython] N_element020  label="N_element : 009"  # scripted group (container) (typed FeaturePython)
  n = 5
  ref = N_element
FEATURE [App::DocumentObjectGroupPython] O_element048  label="O_element : 024"  # scripted group (container) (typed FeaturePython)
  n = 1
  ref = O_element
FEATURE [App::DocumentObjectGroupPython] G4_GUANINE  # scripted group (container) (typed FeaturePython)
  Dunit = g/cm3
  Dvalue = 2.2
  Group = -> [C_element051,H_element044,N_element020,O_element048]
  conduct = 2
  density = 1
  expand = 3
  formula = G4_GUANINE
  name = G4_GUANINE
  specific = 4
FEATURE [App::DocumentObjectGroupPython] Ca_element012  label="Ca_element : 006"  # scripted group (container) (typed FeaturePython)
  n = 1
  ref = Ca_element
FEATURE [App::DocumentObjectGroupPython] S_element014  label="S_element : 005"  # scripted group (container) (typed FeaturePython)
  n = 1
  ref = S_element
FEATURE [App::DocumentObjectGroupPython] O_element049  label="O_element : 6"  # scripted group (container) (typed FeaturePython)
  n = 6
  ref = O_element
FEATURE [App::DocumentObjectGroupPython] H_element045  label="H_element : 024"  # scripted group (container) (typed FeaturePython)
  n = 4
  ref = H_element
FEATURE [App::DocumentObjectGroupPython] G4_GYPSUM  # scripted group (container) (typed FeaturePython)
  Dunit = g/cm3
  Dvalue = 2.32
  Group = -> [Ca_element012,S_element014,O_element049,H_element045]
  conduct = 2
  density = 1
  expand = 3
  formula = G4_GYPSUM
  name = G4_GYPSUM
  specific = 4
FEATURE [App::DocumentObjectGroupPython] C_element052  label="C_element : 7"  # scripted group (container) (typed FeaturePython)
  n = 7
  ref = C_element
FEATURE [App::DocumentObjectGroupPython] H_element046  label="H_element : 16"  # scripted group (container) (typed FeaturePython)
  n = 16
  ref = H_element
FEATURE [App::DocumentObjectGroupPython] G4_N_HEPTANE  label="G4_N-HEPTANE"  # scripted group (container) (typed FeaturePython)
  Dunit = g/cm3
  Dvalue = 0.68376
  Group = -> [C_element052,H_element046]
  conduct = 2
  density = 1
  expand = 3
  formula = G4_N-HEPTANE
  name = G4_N-HEPTANE
  specific = 4
FEATURE [App::DocumentObjectGroupPython] C_element053  label="C_element : 029"  # scripted group (container) (typed FeaturePython)
  n = 6
  ref = C_element
FEATURE [App::DocumentObjectGroupPython] H_element047  label="H_element : 14"  # scripted group (container) (typed FeaturePython)
  n = 14
  ref = H_element
FEATURE [App::DocumentObjectGroupPython] G4_N_HEXANE  label="G4_N-HEXANE"  # scripted group (container) (typed FeaturePython)
  Dunit = g/cm3
  Dvalue = 0.6603
  Group = -> [C_element053,H_element047]
  conduct = 2
  density = 1
  expand = 3
  formula = G4_N-HEXANE
  name = G4_N-HEXANE
  specific = 4
FEATURE [App::DocumentObjectGroupPython] C_element054  label="C_element : 22"  # scripted group (container) (typed FeaturePython)
  n = 22
  ref = C_element
FEATURE [App::DocumentObjectGroupPython] H_element048  label="H_element : 025"  # scripted group (container) (typed FeaturePython)
  n = 10
  ref = H_element
FEATURE [App::DocumentObjectGroupPython] N_element021  label="N_element : 010"  # scripted group (container) (typed FeaturePython)
  n = 2
  ref = N_element
FEATURE [App::DocumentObjectGroupPython] O_element050  label="O_element : 025"  # scripted group (container) (typed FeaturePython)
  n = 5
  ref = O_element
FEATURE [App::DocumentObjectGroupPython] G4_KAPTON  # scripted group (container) (typed FeaturePython)
  Dunit = g/cm3
  Dvalue = 1.42
  Group = -> [C_element054,H_element048,N_element021,O_element050]
  conduct = 2
  density = 1
  expand = 3
  formula = G4_KAPTON
  name = G4_KAPTON
  specific = 4
FEATURE [App::DocumentObjectGroupPython] La_element001  label="La_element : 1"  # scripted group (container) (typed FeaturePython)
  n = 1
  ref = La_element
FEATURE [App::DocumentObjectGroupPython] Br_element003  label="Br_element : 002"  # scripted group (container) (typed FeaturePython)
  n = 1
  ref = Br_element
FEATURE [App::DocumentObjectGroupPython] O_element051  label="O_element : 026"  # scripted group (container) (typed FeaturePython)
  n = 1
  ref = O_element
FEATURE [App::DocumentObjectGroupPython] G4_LANTHANUM_OXYBROMIDE  # scripted group (container) (typed FeaturePython)
  Dunit = g/cm3
  Dvalue = 6.28
  Group = -> [La_element001,Br_element003,O_element051]
  conduct = 2
  density = 1
  expand = 3
  formula = G4_LANTHANUM_OXYBROMIDE
  name = G4_LANTHANUM_OXYBROMIDE
  specific = 4
FEATURE [App::DocumentObjectGroupPython] La_element002  label="La_element : 2"  # scripted group (container) (typed FeaturePython)
  n = 2
  ref = La_element
FEATURE [App::DocumentObjectGroupPython] O_element052  label="O_element : 027"  # scripted group (container) (typed FeaturePython)
  n = 2
  ref = O_element
FEATURE [App::DocumentObjectGroupPython] S_element015  label="S_element : 006"  # scripted group (container) (typed FeaturePython)
  n = 1
  ref = S_element
FEATURE [App::DocumentObjectGroupPython] G4_LANTHANUM_OXYSULFIDE  # scripted group (container) (typed FeaturePython)
  Dunit = g/cm3
  Dvalue = 5.86
  Group = -> [La_element002,O_element052,S_element015]
  conduct = 2
  density = 1
  expand = 3
  formula = G4_LANTHANUM_OXYSULFIDE
  name = G4_LANTHANUM_OXYSULFIDE
  specific = 4
FEATURE [App::DocumentObjectGroupPython] O_element053  label="O_element : 0.072"  # scripted group (container) (typed FeaturePython)
  n = 0.071682
FEATURE [App::DocumentObjectGroupPython] Pb_element002  label="Pb_element : 0.928"  # scripted group (container) (typed FeaturePython)
  n = 0.928318
FEATURE [App::DocumentObjectGroupPython] G4_LEAD_OXIDE  # scripted group (container) (typed FeaturePython)
  Dunit = g/cm3
  Dvalue = 9.53
  Group = -> [O_element053,Pb_element002]
  conduct = 2
  density = 1
  expand = 3
  formula = G4_LEAD_OXIDE
  name = G4_LEAD_OXIDE
  specific = 4
FEATURE [App::DocumentObjectGroupPython] Li_element001  label="Li_element : 1"  # scripted group (container) (typed FeaturePython)
  n = 1
  ref = Li_element
FEATURE [App::DocumentObjectGroupPython] N_element022  label="N_element : 011"  # scripted group (container) (typed FeaturePython)
  n = 1
  ref = N_element
FEATURE [App::DocumentObjectGroupPython] H_element049  label="H_element : 026"  # scripted group (container) (typed FeaturePython)
  n = 2
  ref = H_element
FEATURE [App::DocumentObjectGroupPython] G4_LITHIUM_AMIDE  # scripted group (container) (typed FeaturePython)
  Dunit = g/cm3
  Dvalue = 1.178
  Group = -> [Li_element001,N_element022,H_element049]
  conduct = 2
  density = 1
  expand = 3
  formula = G4_LITHIUM_AMIDE
  name = G4_LITHIUM_AMIDE
  specific = 4
FEATURE [App::DocumentObjectGroupPython] Li_element002  label="Li_element : 2"  # scripted group (container) (typed FeaturePython)
  n = 2
  ref = Li_element
FEATURE [App::DocumentObjectGroupPython] C_element055  label="C_element : 030"  # scripted group (container) (typed FeaturePython)
  n = 1
  ref = C_element
FEATURE [App::DocumentObjectGroupPython] O_element054  label="O_element : 028"  # scripted group (container) (typed FeaturePython)
  n = 3
  ref = O_element
FEATURE [App::DocumentObjectGroupPython] G4_LITHIUM_CARBONATE  # scripted group (container) (typed FeaturePython)
  Dunit = g/cm3
  Dvalue = 2.11
  Group = -> [Li_element002,C_element055,O_element054]
  conduct = 2
  density = 1
  expand = 3
  formula = G4_LITHIUM_CARBONATE
  name = G4_LITHIUM_CARBONATE
  specific = 4
FEATURE [App::DocumentObjectGroupPython] Li_element003  label="Li_element : 003"  # scripted group (container) (typed FeaturePython)
  n = 1
  ref = Li_element
FEATURE [App::DocumentObjectGroupPython] F_element012  label="F_element : 004"  # scripted group (container) (typed FeaturePython)
  n = 1
  ref = F_element
FEATURE [App::DocumentObjectGroupPython] G4_LITHIUM_FLUORIDE  # scripted group (container) (typed FeaturePython)
  Dunit = g/cm3
  Dvalue = 2.635
  Group = -> [Li_element003,F_element012]
  conduct = 2
  density = 1
  expand = 3
  formula = G4_LITHIUM_FLUORIDE
  name = G4_LITHIUM_FLUORIDE
  specific = 4
FEATURE [App::DocumentObjectGroupPython] Li_element004  label="Li_element : 004"  # scripted group (container) (typed FeaturePython)
  n = 1
  ref = Li_element
FEATURE [App::DocumentObjectGroupPython] H_element050  label="H_element : 027"  # scripted group (container) (typed FeaturePython)
  n = 1
  ref = H_element
FEATURE [App::DocumentObjectGroupPython] G4_LITHIUM_HYDRIDE  # scripted group (container) (typed FeaturePython)
  Dunit = g/cm3
  Dvalue = 0.82
  Group = -> [Li_element004,H_element050]
  conduct = 2
  density = 1
  expand = 3
  formula = G4_LITHIUM_HYDRIDE
  name = G4_LITHIUM_HYDRIDE
  specific = 4
FEATURE [App::DocumentObjectGroupPython] Li_element005  label="Li_element : 005"  # scripted group (container) (typed FeaturePython)
  n = 1
  ref = Li_element
FEATURE [App::DocumentObjectGroupPython] I_element003  label="I_element : 002"  # scripted group (container) (typed FeaturePython)
  n = 1
  ref = I_element
FEATURE [App::DocumentObjectGroupPython] G4_LITHIUM_IODIDE  # scripted group (container) (typed FeaturePython)
  Dunit = g/cm3
  Dvalue = 3.494
  Group = -> [Li_element005,I_element003]
  conduct = 2
  density = 1
  expand = 3
  formula = G4_LITHIUM_IODIDE
  name = G4_LITHIUM_IODIDE
  specific = 4
FEATURE [App::DocumentObjectGroupPython] Li_element006  label="Li_element : 006"  # scripted group (container) (typed FeaturePython)
  n = 2
  ref = Li_element
FEATURE [App::DocumentObjectGroupPython] O_element055  label="O_element : 029"  # scripted group (container) (typed FeaturePython)
  n = 1
  ref = O_element
FEATURE [App::DocumentObjectGroupPython] G4_LITHIUM_OXIDE  # scripted group (container) (typed FeaturePython)
  Dunit = g/cm3
  Dvalue = 2.013
  Group = -> [Li_element006,O_element055]
  conduct = 2
  density = 1
  expand = 3
  formula = G4_LITHIUM_OXIDE
  name = G4_LITHIUM_OXIDE
  specific = 4
FEATURE [App::DocumentObjectGroupPython] Li_element007  label="Li_element : 007"  # scripted group (container) (typed FeaturePython)
  n = 2
  ref = Li_element
FEATURE [App::DocumentObjectGroupPython] B_element005  label="B_element : 005"  # scripted group (container) (typed FeaturePython)
  n = 4
  ref = B_element
FEATURE [App::DocumentObjectGroupPython] O_element056  label="O_element : 7"  # scripted group (container) (typed FeaturePython)
  n = 7
  ref = O_element
FEATURE [App::DocumentObjectGroupPython] G4_LITHIUM_TETRABORATE  # scripted group (container) (typed FeaturePython)
  Dunit = g/cm3
  Dvalue = 2.44
  Group = -> [Li_element007,B_element005,O_element056]
  conduct = 2
  density = 1
  expand = 3
  formula = G4_LITHIUM_TETRABORATE
  name = G4_LITHIUM_TETRABORATE
  specific = 4
FEATURE [App::DocumentObjectGroupPython] H_element051  label="H_element : 0.105"  # scripted group (container) (typed FeaturePython)
  n = 0.105
FEATURE [App::DocumentObjectGroupPython] C_element056  label="C_element : 0.083"  # scripted group (container) (typed FeaturePython)
  n = 0.083
FEATURE [App::DocumentObjectGroupPython] N_element023  label="N_element : 0.023"  # scripted group (container) (typed FeaturePython)
  n = 0.023
FEATURE [App::DocumentObjectGroupPython] O_element057  label="O_element : 0.779"  # scripted group (container) (typed FeaturePython)
  n = 0.779
FEATURE [App::DocumentObjectGroupPython] Na_element010  label="Na_element : 0.097"  # scripted group (container) (typed FeaturePython)
  n = 0.002
FEATURE [App::DocumentObjectGroupPython] P_element006  label="P_element : 0.105"  # scripted group (container) (typed FeaturePython)
  n = 0.001
FEATURE [App::DocumentObjectGroupPython] S_element016  label="S_element : 0.017"  # scripted group (container) (typed FeaturePython)
  n = 0.002
FEATURE [App::DocumentObjectGroupPython] Cl_element014  label="Cl_element : 0.587"  # scripted group (container) (typed FeaturePython)
  n = 0.003
FEATURE [App::DocumentObjectGroupPython] K_element005  label="K_element : 0.015"  # scripted group (container) (typed FeaturePython)
  n = 0.002
FEATURE [App::DocumentObjectGroupPython] G4_LUNG_ICRP  # scripted group (container) (typed FeaturePython)
  Dunit = g/cm3
  Dvalue = 1.04
  Group = -> [H_element051,C_element056,N_element023,O_element057,Na_element010,P_element006,S_element016,Cl_element014,K_element005]
  conduct = 2
  density = 1
  expand = 3
  formula = G4_LUNG_ICRP
  name = G4_LUNG_ICRP
  specific = 4
FEATURE [App::DocumentObjectGroupPython] H_element052  label="H_element : 0.116"  # scripted group (container) (typed FeaturePython)
  n = 0.114318
FEATURE [App::DocumentObjectGroupPython] C_element057  label="C_element : 0.656"  # scripted group (container) (typed FeaturePython)
  n = 0.655824
FEATURE [App::DocumentObjectGroupPython] O_element058  label="O_element : 0.092"  # scripted group (container) (typed FeaturePython)
  n = 0.0921831
FEATURE [App::DocumentObjectGroupPython] Mg_element004  label="Mg_element : 0.135"  # scripted group (container) (typed FeaturePython)
  n = 0.134792
FEATURE [App::DocumentObjectGroupPython] Ca_element013  label="Ca_element : 0.003"  # scripted group (container) (typed FeaturePython)
  n = 0.002883
FEATURE [App::DocumentObjectGroupPython] G4_M3_WAX  # scripted group (container) (typed FeaturePython)
  Dunit = g/cm3
  Dvalue = 1.05
  Group = -> [H_element052,C_element057,O_element058,Mg_element004,Ca_element013]
  conduct = 2
  density = 1
  expand = 3
  formula = G4_M3_WAX
  name = G4_M3_WAX
  specific = 4
FEATURE [App::DocumentObjectGroupPython] Mg_element005  label="Mg_element : 1"  # scripted group (container) (typed FeaturePython)
  n = 1
  ref = Mg_element
FEATURE [App::DocumentObjectGroupPython] C_element058  label="C_element : 031"  # scripted group (container) (typed FeaturePython)
  n = 1
  ref = C_element
FEATURE [App::DocumentObjectGroupPython] O_element059  label="O_element : 030"  # scripted group (container) (typed FeaturePython)
  n = 3
  ref = O_element
FEATURE [App::DocumentObjectGroupPython] G4_MAGNESIUM_CARBONATE  # scripted group (container) (typed FeaturePython)
  Dunit = g/cm3
  Dvalue = 2.958
  Group = -> [Mg_element005,C_element058,O_element059]
  conduct = 2
  density = 1
  expand = 3
  formula = G4_MAGNESIUM_CARBONATE
  name = G4_MAGNESIUM_CARBONATE
  specific = 4
FEATURE [App::DocumentObjectGroupPython] Mg_element006  label="Mg_element : 002"  # scripted group (container) (typed FeaturePython)
  n = 1
  ref = Mg_element
FEATURE [App::DocumentObjectGroupPython] F_element013  label="F_element : 005"  # scripted group (container) (typed FeaturePython)
  n = 2
  ref = F_element
FEATURE [App::DocumentObjectGroupPython] G4_MAGNESIUM_FLUORIDE  # scripted group (container) (typed FeaturePython)
  Dunit = g/cm3
  Dvalue = 3
  Group = -> [Mg_element006,F_element013]
  conduct = 2
  density = 1
  expand = 3
  formula = G4_MAGNESIUM_FLUORIDE
  name = G4_MAGNESIUM_FLUORIDE
  specific = 4
FEATURE [App::DocumentObjectGroupPython] Mg_element007  label="Mg_element : 003"  # scripted group (container) (typed FeaturePython)
  n = 1
  ref = Mg_element
FEATURE [App::DocumentObjectGroupPython] O_element060  label="O_element : 031"  # scripted group (container) (typed FeaturePython)
  n = 1
  ref = O_element
FEATURE [App::DocumentObjectGroupPython] G4_MAGNESIUM_OXIDE  # scripted group (container) (typed FeaturePython)
  Dunit = g/cm3
  Dvalue = 3.58
  Group = -> [Mg_element007,O_element060]
  conduct = 2
  density = 1
  expand = 3
  formula = G4_MAGNESIUM_OXIDE
  name = G4_MAGNESIUM_OXIDE
  specific = 4
FEATURE [App::DocumentObjectGroupPython] Mg_element008  label="Mg_element : 004"  # scripted group (container) (typed FeaturePython)
  n = 1
  ref = Mg_element
FEATURE [App::DocumentObjectGroupPython] B_element006  label="B_element : 006"  # scripted group (container) (typed FeaturePython)
  n = 4
  ref = B_element
FEATURE [App::DocumentObjectGroupPython] O_element061  label="O_element : 032"  # scripted group (container) (typed FeaturePython)
  n = 7
  ref = O_element
FEATURE [App::DocumentObjectGroupPython] G4_MAGNESIUM_TETRABORATE  # scripted group (container) (typed FeaturePython)
  Dunit = g/cm3
  Dvalue = 2.53
  Group = -> [Mg_element008,B_element006,O_element061]
  conduct = 2
  density = 1
  expand = 3
  formula = G4_MAGNESIUM_TETRABORATE
  name = G4_MAGNESIUM_TETRABORATE
  specific = 4
FEATURE [App::DocumentObjectGroupPython] Hg_element001  label="Hg_element : 1"  # scripted group (container) (typed FeaturePython)
  n = 1
  ref = Hg_element
FEATURE [App::DocumentObjectGroupPython] I_element004  label="I_element : 2"  # scripted group (container) (typed FeaturePython)
  n = 2
  ref = I_element
FEATURE [App::DocumentObjectGroupPython] G4_MERCURIC_IODIDE  # scripted group (container) (typed FeaturePython)
  Dunit = g/cm3
  Dvalue = 6.36
  Group = -> [Hg_element001,I_element004]
  conduct = 2
  density = 1
  expand = 3
  formula = G4_MERCURIC_IODIDE
  name = G4_MERCURIC_IODIDE
  specific = 4
FEATURE [App::DocumentObjectGroupPython] C_element059  label="C_element : 032"  # scripted group (container) (typed FeaturePython)
  n = 1
  ref = C_element
FEATURE [App::DocumentObjectGroupPython] H_element053  label="H_element : 028"  # scripted group (container) (typed FeaturePython)
  n = 4
  ref = H_element
FEATURE [App::DocumentObjectGroupPython] G4_METHANE  # scripted group (container) (typed FeaturePython)
  Dunit = g/cm3
  Dvalue = 0.000667151
  Group = -> [C_element059,H_element053]
  conduct = 2
  density = 1
  expand = 3
  formula = G4_METHANE
  name = G4_METHANE
  specific = 4
FEATURE [App::DocumentObjectGroupPython] C_element060  label="C_element : 033"  # scripted group (container) (typed FeaturePython)
  n = 1
  ref = C_element
FEATURE [App::DocumentObjectGroupPython] H_element054  label="H_element : 029"  # scripted group (container) (typed FeaturePython)
  n = 4
  ref = H_element
FEATURE [App::DocumentObjectGroupPython] O_element062  label="O_element : 033"  # scripted group (container) (typed FeaturePython)
  n = 1
  ref = O_element
FEATURE [App::DocumentObjectGroupPython] G4_METHANOL  # scripted group (container) (typed FeaturePython)
  Dunit = g/cm3
  Dvalue = 0.7914
  Group = -> [C_element060,H_element054,O_element062]
  conduct = 2
  density = 1
  expand = 3
  formula = G4_METHANOL
  name = G4_METHANOL
  specific = 4
FEATURE [App::DocumentObjectGroupPython] H_element055  label="H_element : 0.134"  # scripted group (container) (typed FeaturePython)
  n = 0.13404
FEATURE [App::DocumentObjectGroupPython] C_element061  label="C_element : 0.778"  # scripted group (container) (typed FeaturePython)
  n = 0.77796
FEATURE [App::DocumentObjectGroupPython] O_element063  label="O_element : 0.035"  # scripted group (container) (typed FeaturePython)
  n = 0.03502
FEATURE [App::DocumentObjectGroupPython] Mg_element009  label="Mg_element : 0.039"  # scripted group (container) (typed FeaturePython)
  n = 0.038594
FEATURE [App::DocumentObjectGroupPython] Ti_element002  label="Ti_element : 0.014"  # scripted group (container) (typed FeaturePython)
  n = 0.014386
FEATURE [App::DocumentObjectGroupPython] G4_MIX_D_WAX  # scripted group (container) (typed FeaturePython)
  Dunit = g/cm3
  Dvalue = 0.99
  Group = -> [H_element055,C_element061,O_element063,Mg_element009,Ti_element002]
  conduct = 2
  density = 1
  expand = 3
  formula = G4_MIX_D_WAX
  name = G4_MIX_D_WAX
  specific = 4
FEATURE [App::DocumentObjectGroupPython] H_element056  label="H_element : 0.135"  # scripted group (container) (typed FeaturePython)
  n = 0.081192
FEATURE [App::DocumentObjectGroupPython] C_element062  label="C_element : 0.583"  # scripted group (container) (typed FeaturePython)
  n = 0.583442
FEATURE [App::DocumentObjectGroupPython] N_element024  label="N_element : 0.018"  # scripted group (container) (typed FeaturePython)
  n = 0.017798
FEATURE [App::DocumentObjectGroupPython] O_element064  label="O_element : 0.186"  # scripted group (container) (typed FeaturePython)
  n = 0.186381
FEATURE [App::DocumentObjectGroupPython] Mg_element010  label="Mg_element : 0.130"  # scripted group (container) (typed FeaturePython)
  n = 0.130287
FEATURE [App::DocumentObjectGroupPython] Cl_element015  label="Cl_element : 0.588"  # scripted group (container) (typed FeaturePython)
  n = 0.0009
FEATURE [App::DocumentObjectGroupPython] G4_MS20_TISSUE  # scripted group (container) (typed FeaturePython)
  Dunit = g/cm3
  Dvalue = 1
  Group = -> [H_element056,C_element062,N_element024,O_element064,Mg_element010,Cl_element015]
  conduct = 2
  density = 1
  expand = 3
  formula = G4_MS20_TISSUE
  name = G4_MS20_TISSUE
  specific = 4
FEATURE [App::DocumentObjectGroupPython] H_element057  label="H_element : 0.136"  # scripted group (container) (typed FeaturePython)
  n = 0.102
FEATURE [App::DocumentObjectGroupPython] C_element063  label="C_element : 0.143"  # scripted group (container) (typed FeaturePython)
  n = 0.143
FEATURE [App::DocumentObjectGroupPython] N_element025  label="N_element : 0.034"  # scripted group (container) (typed FeaturePython)
  n = 0.034
FEATURE [App::DocumentObjectGroupPython] O_element065  label="O_element : 0.710"  # scripted group (container) (typed FeaturePython)
  n = 0.71
FEATURE [App::DocumentObjectGroupPython] Na_element011  label="Na_element : 0.098"  # scripted group (container) (typed FeaturePython)
  n = 0.001
FEATURE [App::DocumentObjectGroupPython] P_element007  label="P_element : 0.002"  # scripted group (container) (typed FeaturePython)
  n = 0.002
FEATURE [App::DocumentObjectGroupPython] S_element017  label="S_element : 0.018"  # scripted group (container) (typed FeaturePython)
  n = 0.003
FEATURE [App::DocumentObjectGroupPython] Cl_element016  label="Cl_element : 0.589"  # scripted group (container) (typed FeaturePython)
  n = 0.001
FEATURE [App::DocumentObjectGroupPython] K_element006  label="K_element : 0.004"  # scripted group (container) (typed FeaturePython)
  n = 0.004
FEATURE [App::DocumentObjectGroupPython] G4_MUSCLE_SKELETAL_ICRP  # scripted group (container) (typed FeaturePython)
  Dunit = g/cm3
  Dvalue = 1.05
  Group = -> [H_element057,C_element063,N_element025,O_element065,Na_element011,P_element007,S_element017,Cl_element016,K_element006]
  conduct = 2
  density = 1
  expand = 3
  formula = G4_MUSCLE_SKELETAL_ICRP
  name = G4_MUSCLE_SKELETAL_ICRP
  specific = 4
FEATURE [App::DocumentObjectGroupPython] H_element058  label="H_element : 0.137"  # scripted group (container) (typed FeaturePython)
  n = 0.102102
FEATURE [App::DocumentObjectGroupPython] C_element064  label="C_element : 0.123"  # scripted group (container) (typed FeaturePython)
  n = 0.123123
FEATURE [App::DocumentObjectGroupPython] N_element026  label="N_element : 0.756"  # scripted group (container) (typed FeaturePython)
  n = 0.035035
FEATURE [App::DocumentObjectGroupPython] O_element066  label="O_element : 0.730"  # scripted group (container) (typed FeaturePython)
  n = 0.72973
FEATURE [App::DocumentObjectGroupPython] Na_element012  label="Na_element : 0.099"  # scripted group (container) (typed FeaturePython)
  n = 0.001001
FEATURE [App::DocumentObjectGroupPython] P_element008  label="P_element : 0.106"  # scripted group (container) (typed FeaturePython)
  n = 0.002002
FEATURE [App::DocumentObjectGroupPython] S_element018  label="S_element : 0.019"  # scripted group (container) (typed FeaturePython)
  n = 0.004004
FEATURE [App::DocumentObjectGroupPython] K_element007  label="K_element : 0.016"  # scripted group (container) (typed FeaturePython)
  n = 0.003003
FEATURE [App::DocumentObjectGroupPython] G4_MUSCLE_STRIATED_ICRU  # scripted group (container) (typed FeaturePython)
  Dunit = g/cm3
  Dvalue = 1.04
  Group = -> [H_element058,C_element064,N_element026,O_element066,Na_element012,P_element008,S_element018,K_element007]
  conduct = 2
  density = 1
  expand = 3
  formula = G4_MUSCLE_STRIATED_ICRU
  name = G4_MUSCLE_STRIATED_ICRU
  specific = 4
FEATURE [App::DocumentObjectGroupPython] H_element059  label="H_element : 0.098"  # scripted group (container) (typed FeaturePython)
  n = 0.0982341
FEATURE [App::DocumentObjectGroupPython] C_element065  label="C_element : 0.156"  # scripted group (container) (typed FeaturePython)
  n = 0.156214
FEATURE [App::DocumentObjectGroupPython] N_element027  label="N_element : 0.757"  # scripted group (container) (typed FeaturePython)
  n = 0.035451
FEATURE [App::DocumentObjectGroupPython] O_element067  label="O_element : 0.880"  # scripted group (container) (typed FeaturePython)
  n = 0.710101
FEATURE [App::DocumentObjectGroupPython] G4_MUSCLE_WITH_SUCROSE  # scripted group (container) (typed FeaturePython)
  Dunit = g/cm3
  Dvalue = 1.11
  Group = -> [H_element059,C_element065,N_element027,O_element067]
  conduct = 2
  density = 1
  expand = 3
  formula = G4_MUSCLE_WITH_SUCROSE
  name = G4_MUSCLE_WITH_SUCROSE
  specific = 4
FEATURE [App::DocumentObjectGroupPython] H_element060  label="H_element : 0.138"  # scripted group (container) (typed FeaturePython)
  n = 0.101969
FEATURE [App::DocumentObjectGroupPython] C_element066  label="C_element : 0.120"  # scripted group (container) (typed FeaturePython)
  n = 0.120058
FEATURE [App::DocumentObjectGroupPython] N_element028  label="N_element : 0.758"  # scripted group (container) (typed FeaturePython)
  n = 0.035451
FEATURE [App::DocumentObjectGroupPython] O_element068  label="O_element : 0.743"  # scripted group (container) (typed FeaturePython)
  n = 0.742522
FEATURE [App::DocumentObjectGroupPython] G4_MUSCLE_WITHOUT_SUCROSE  # scripted group (container) (typed FeaturePython)
  Dunit = g/cm3
  Dvalue = 1.07
  Group = -> [H_element060,C_element066,N_element028,O_element068]
  conduct = 2
  density = 1
  expand = 3
  formula = G4_MUSCLE_WITHOUT_SUCROSE
  name = G4_MUSCLE_WITHOUT_SUCROSE
  specific = 4
FEATURE [App::DocumentObjectGroupPython] C_element067  label="C_element : 10"  # scripted group (container) (typed FeaturePython)
  n = 10
  ref = C_element
FEATURE [App::DocumentObjectGroupPython] H_element061  label="H_element : 030"  # scripted group (container) (typed FeaturePython)
  n = 8
  ref = H_element
FEATURE [App::DocumentObjectGroupPython] G4_NAPHTHALENE  # scripted group (container) (typed FeaturePython)
  Dunit = g/cm3
  Dvalue = 1.145
  Group = -> [C_element067,H_element061]
  conduct = 2
  density = 1
  expand = 3
  formula = G4_NAPHTHALENE
  name = G4_NAPHTHALENE
  specific = 4
FEATURE [App::DocumentObjectGroupPython] C_element068  label="C_element : 034"  # scripted group (container) (typed FeaturePython)
  n = 6
  ref = C_element
FEATURE [App::DocumentObjectGroupPython] H_element062  label="H_element : 031"  # scripted group (container) (typed FeaturePython)
  n = 5
  ref = H_element
FEATURE [App::DocumentObjectGroupPython] N_element029  label="N_element : 012"  # scripted group (container) (typed FeaturePython)
  n = 1
  ref = N_element
FEATURE [App::DocumentObjectGroupPython] O_element069  label="O_element : 034"  # scripted group (container) (typed FeaturePython)
  n = 2
  ref = O_element
FEATURE [App::DocumentObjectGroupPython] G4_NITROBENZENE  # scripted group (container) (typed FeaturePython)
  Dunit = g/cm3
  Dvalue = 1.19867
  Group = -> [C_element068,H_element062,N_element029,O_element069]
  conduct = 2
  density = 1
  expand = 3
  formula = G4_NITROBENZENE
  name = G4_NITROBENZENE
  specific = 4
FEATURE [App::DocumentObjectGroupPython] N_element030  label="N_element : 013"  # scripted group (container) (typed FeaturePython)
  n = 2
  ref = N_element
FEATURE [App::DocumentObjectGroupPython] O_element070  label="O_element : 035"  # scripted group (container) (typed FeaturePython)
  n = 1
  ref = O_element
FEATURE [App::DocumentObjectGroupPython] G4_NITROUS_OXIDE  # scripted group (container) (typed FeaturePython)
  Dunit = g/cm3
  Dvalue = 0.00183094
  Group = -> [N_element030,O_element070]
  conduct = 2
  density = 1
  expand = 3
  formula = G4_NITROUS_OXIDE
  name = G4_NITROUS_OXIDE
  specific = 4
FEATURE [App::DocumentObjectGroupPython] H_element063  label="H_element : 0.104"  # scripted group (container) (typed FeaturePython)
  n = 0.103509
FEATURE [App::DocumentObjectGroupPython] C_element069  label="C_element : 0.648"  # scripted group (container) (typed FeaturePython)
  n = 0.648416
FEATURE [App::DocumentObjectGroupPython] N_element031  label="N_element : 0.100"  # scripted group (container) (typed FeaturePython)
  n = 0.0995361
FEATURE [App::DocumentObjectGroupPython] O_element071  label="O_element : 0.149"  # scripted group (container) (typed FeaturePython)
  n = 0.148539
FEATURE [App::DocumentObjectGroupPython] G4_NYLON_8062  label="G4_NYLON-8062"  # scripted group (container) (typed FeaturePython)
  Dunit = g/cm3
  Dvalue = 1.08
  Group = -> [H_element063,C_element069,N_element031,O_element071]
  conduct = 2
  density = 1
  expand = 3
  formula = G4_NYLON-8062
  name = G4_NYLON-8062
  specific = 4
FEATURE [App::DocumentObjectGroupPython] C_element070  label="C_element : 035"  # scripted group (container) (typed FeaturePython)
  n = 6
  ref = C_element
FEATURE [App::DocumentObjectGroupPython] H_element064  label="H_element : 11"  # scripted group (container) (typed FeaturePython)
  n = 11
  ref = H_element
FEATURE [App::DocumentObjectGroupPython] N_element032  label="N_element : 014"  # scripted group (container) (typed FeaturePython)
  n = 1
  ref = N_element
FEATURE [App::DocumentObjectGroupPython] O_element072  label="O_element : 036"  # scripted group (container) (typed FeaturePython)
  n = 1
  ref = O_element
FEATURE [App::DocumentObjectGroupPython] G4_NYLON_6_6  label="G4_NYLON-6-6"  # scripted group (container) (typed FeaturePython)
  Dunit = g/cm3
  Dvalue = 1.14
  Group = -> [C_element070,H_element064,N_element032,O_element072]
  conduct = 2
  density = 1
  expand = 3
  formula = G4_NYLON-6-6
  name = G4_NYLON-6-6
  specific = 4
FEATURE [App::DocumentObjectGroupPython] H_element065  label="H_element : 0.139"  # scripted group (container) (typed FeaturePython)
  n = 0.107062
FEATURE [App::DocumentObjectGroupPython] C_element071  label="C_element : 0.680"  # scripted group (container) (typed FeaturePython)
  n = 0.680449
FEATURE [App::DocumentObjectGroupPython] N_element033  label="N_element : 0.099"  # scripted group (container) (typed FeaturePython)
  n = 0.099189
FEATURE [App::DocumentObjectGroupPython] O_element073  label="O_element : 0.113"  # scripted group (container) (typed FeaturePython)
  n = 0.1133
FEATURE [App::DocumentObjectGroupPython] G4_NYLON_6_10  label="G4_NYLON-6-10"  # scripted group (container) (typed FeaturePython)
  Dunit = g/cm3
  Dvalue = 1.14
  Group = -> [H_element065,C_element071,N_element033,O_element073]
  conduct = 2
  density = 1
  expand = 3
  formula = G4_NYLON-6-10
  name = G4_NYLON-6-10
  specific = 4
FEATURE [App::DocumentObjectGroupPython] H_element066  label="H_element : 0.140"  # scripted group (container) (typed FeaturePython)
  n = 0.115476
FEATURE [App::DocumentObjectGroupPython] C_element072  label="C_element : 0.721"  # scripted group (container) (typed FeaturePython)
  n = 0.720818
FEATURE [App::DocumentObjectGroupPython] N_element034  label="N_element : 0.076"  # scripted group (container) (typed FeaturePython)
  n = 0.0764169
FEATURE [App::DocumentObjectGroupPython] O_element074  label="O_element : 0.087"  # scripted group (container) (typed FeaturePython)
  n = 0.0872889
FEATURE [App::DocumentObjectGroupPython] G4_NYLON_11_RILSAN  label="G4_NYLON-11_RILSAN"  # scripted group (container) (typed FeaturePython)
  Dunit = g/cm3
  Dvalue = 1.425
  Group = -> [H_element066,C_element072,N_element034,O_element074]
  conduct = 2
  density = 1
  expand = 3
  formula = G4_NYLON-11_RILSAN
  name = G4_NYLON-11_RILSAN
  specific = 4
FEATURE [App::DocumentObjectGroupPython] C_element073  label="C_element : 8"  # scripted group (container) (typed FeaturePython)
  n = 8
  ref = C_element
FEATURE [App::DocumentObjectGroupPython] H_element067  label="H_element : 18"  # scripted group (container) (typed FeaturePython)
  n = 18
  ref = H_element
FEATURE [App::DocumentObjectGroupPython] G4_OCTANE  # scripted group (container) (typed FeaturePython)
  Dunit = g/cm3
  Dvalue = 0.7026
  Group = -> [C_element073,H_element067]
  conduct = 2
  density = 1
  expand = 3
  formula = G4_OCTANE
  name = G4_OCTANE
  specific = 4
FEATURE [App::DocumentObjectGroupPython] C_element074  label="C_element : 25"  # scripted group (container) (typed FeaturePython)
  n = 25
  ref = C_element
FEATURE [App::DocumentObjectGroupPython] H_element068  label="H_element : 52"  # scripted group (container) (typed FeaturePython)
  n = 52
  ref = H_element
FEATURE [App::DocumentObjectGroupPython] G4_PARAFFIN  # scripted group (container) (typed FeaturePython)
  Dunit = g/cm3
  Dvalue = 0.93
  Group = -> [C_element074,H_element068]
  conduct = 2
  density = 1
  expand = 3
  formula = G4_PARAFFIN
  name = G4_PARAFFIN
  specific = 4
FEATURE [App::DocumentObjectGroupPython] C_element075  label="C_element : 036"  # scripted group (container) (typed FeaturePython)
  n = 5
  ref = C_element
FEATURE [App::DocumentObjectGroupPython] H_element069  label="H_element : 032"  # scripted group (container) (typed FeaturePython)
  n = 12
  ref = H_element
FEATURE [App::DocumentObjectGroupPython] G4_N_PENTANE  label="G4_N-PENTANE"  # scripted group (container) (typed FeaturePython)
  Dunit = g/cm3
  Dvalue = 0.6262
  Group = -> [C_element075,H_element069]
  conduct = 2
  density = 1
  expand = 3
  formula = G4_N-PENTANE
  name = G4_N-PENTANE
  specific = 4
FEATURE [App::DocumentObjectGroupPython] H_element070  label="H_element : 0.014"  # scripted group (container) (typed FeaturePython)
  n = 0.0141
FEATURE [App::DocumentObjectGroupPython] C_element076  label="C_element : 0.072"  # scripted group (container) (typed FeaturePython)
  n = 0.072261
FEATURE [App::DocumentObjectGroupPython] N_element035  label="N_element : 0.019"  # scripted group (container) (typed FeaturePython)
  n = 0.01932
FEATURE [App::DocumentObjectGroupPython] O_element075  label="O_element : 0.066"  # scripted group (container) (typed FeaturePython)
  n = 0.066101
FEATURE [App::DocumentObjectGroupPython] S_element019  label="S_element : 0.020"  # scripted group (container) (typed FeaturePython)
  n = 0.00189
FEATURE [App::DocumentObjectGroupPython] Br_element004  label="Br_element : 0.349"  # scripted group (container) (typed FeaturePython)
  n = 0.349103
FEATURE [App::DocumentObjectGroupPython] Ag_element001  label="Ag_element : 0.474"  # scripted group (container) (typed FeaturePython)
  n = 0.474105
FEATURE [App::DocumentObjectGroupPython] I_element005  label="I_element : 0.003"  # scripted group (container) (typed FeaturePython)
  n = 0.00312
FEATURE [App::DocumentObjectGroupPython] G4_PHOTO_EMULSION  # scripted group (container) (typed FeaturePython)
  Dunit = g/cm3
  Dvalue = 3.815
  Group = -> [H_element070,C_element076,N_element035,O_element075,S_element019,Br_element004,Ag_element001,I_element005]
  conduct = 2
  density = 1
  expand = 3
  formula = G4_PHOTO_EMULSION
  name = G4_PHOTO_EMULSION
  specific = 4
FEATURE [App::DocumentObjectGroupPython] C_element077  label="C_element : 9"  # scripted group (container) (typed FeaturePython)
  n = 9
  ref = C_element
FEATURE [App::DocumentObjectGroupPython] H_element071  label="H_element : 033"  # scripted group (container) (typed FeaturePython)
  n = 10
  ref = H_element
FEATURE [App::DocumentObjectGroupPython] G4_PLASTIC_SC_VINYLTOLUENE  # scripted group (container) (typed FeaturePython)
  Dunit = g/cm3
  Dvalue = 1.032
  Group = -> [C_element077,H_element071]
  conduct = 2
  density = 1
  expand = 3
  formula = G4_PLASTIC_SC_VINYLTOLUENE
  name = G4_PLASTIC_SC_VINYLTOLUENE
  specific = 4
FEATURE [App::DocumentObjectGroupPython] Pu_element001  label="Pu_element : 1"  # scripted group (container) (typed FeaturePython)
  n = 1
  ref = Pu_element
FEATURE [App::DocumentObjectGroupPython] O_element076  label="O_element : 037"  # scripted group (container) (typed FeaturePython)
  n = 2
  ref = O_element
FEATURE [App::DocumentObjectGroupPython] G4_PLUTONIUM_DIOXIDE  # scripted group (container) (typed FeaturePython)
  Dunit = g/cm3
  Dvalue = 11.46
  Group = -> [Pu_element001,O_element076]
  conduct = 2
  density = 1
  expand = 3
  formula = G4_PLUTONIUM_DIOXIDE
  name = G4_PLUTONIUM_DIOXIDE
  specific = 4
FEATURE [App::DocumentObjectGroupPython] C_element078  label="C_element : 037"  # scripted group (container) (typed FeaturePython)
  n = 3
  ref = C_element
FEATURE [App::DocumentObjectGroupPython] H_element072  label="H_element : 034"  # scripted group (container) (typed FeaturePython)
  n = 3
  ref = H_element
FEATURE [App::DocumentObjectGroupPython] N_element036  label="N_element : 015"  # scripted group (container) (typed FeaturePython)
  n = 1
  ref = N_element
FEATURE [App::DocumentObjectGroupPython] G4_POLYACRYLONITRILE  # scripted group (container) (typed FeaturePython)
  Dunit = g/cm3
  Dvalue = 1.17
  Group = -> [C_element078,H_element072,N_element036]
  conduct = 2
  density = 1
  expand = 3
  formula = G4_POLYACRYLONITRILE
  name = G4_POLYACRYLONITRILE
  specific = 4
FEATURE [App::DocumentObjectGroupPython] C_element079  label="C_element : 16"  # scripted group (container) (typed FeaturePython)
  n = 16
  ref = C_element
FEATURE [App::DocumentObjectGroupPython] H_element073  label="H_element : 035"  # scripted group (container) (typed FeaturePython)
  n = 14
  ref = H_element
FEATURE [App::DocumentObjectGroupPython] O_element077  label="O_element : 038"  # scripted group (container) (typed FeaturePython)
  n = 3
  ref = O_element
FEATURE [App::DocumentObjectGroupPython] G4_POLYCARBONATE  # scripted group (container) (typed FeaturePython)
  Dunit = g/cm3
  Dvalue = 1.2
  Group = -> [C_element079,H_element073,O_element077]
  conduct = 2
  density = 1
  expand = 3
  formula = G4_POLYCARBONATE
  name = G4_POLYCARBONATE
  specific = 4
FEATURE [App::DocumentObjectGroupPython] C_element080  label="C_element : 038"  # scripted group (container) (typed FeaturePython)
  n = 8
  ref = C_element
FEATURE [App::DocumentObjectGroupPython] H_element074  label="H_element : 036"  # scripted group (container) (typed FeaturePython)
  n = 7
  ref = H_element
FEATURE [App::DocumentObjectGroupPython] Cl_element017  label="Cl_element : 007"  # scripted group (container) (typed FeaturePython)
  n = 1
  ref = Cl_element
FEATURE [App::DocumentObjectGroupPython] G4_POLYCHLOROSTYRENE  # scripted group (container) (typed FeaturePython)
  Dunit = g/cm3
  Dvalue = 1.3
  Group = -> [C_element080,H_element074,Cl_element017]
  conduct = 2
  density = 1
  expand = 3
  formula = G4_POLYCHLOROSTYRENE
  name = G4_POLYCHLOROSTYRENE
  specific = 4
FEATURE [App::DocumentObjectGroupPython] C_element081  label="C_element : 039"  # scripted group (container) (typed FeaturePython)
  n = 1
  ref = C_element
FEATURE [App::DocumentObjectGroupPython] H_element075  label="H_element : 037"  # scripted group (container) (typed FeaturePython)
  n = 2
  ref = H_element
FEATURE [App::DocumentObjectGroupPython] G4_POLYETHYLENE  # scripted group (container) (typed FeaturePython)
  Dunit = g/cm3
  Dvalue = 0.94
  Group = -> [C_element081,H_element075]
  conduct = 2
  density = 1
  expand = 3
  formula = G4_POLYETHYLENE
  name = G4_POLYETHYLENE
  specific = 4
FEATURE [App::DocumentObjectGroupPython] C_element082  label="C_element : 040"  # scripted group (container) (typed FeaturePython)
  n = 10
  ref = C_element
FEATURE [App::DocumentObjectGroupPython] H_element076  label="H_element : 038"  # scripted group (container) (typed FeaturePython)
  n = 8
  ref = H_element
FEATURE [App::DocumentObjectGroupPython] O_element078  label="O_element : 039"  # scripted group (container) (typed FeaturePython)
  n = 4
  ref = O_element
FEATURE [App::DocumentObjectGroupPython] G4_MYLAR  # scripted group (container) (typed FeaturePython)
  Dunit = g/cm3
  Dvalue = 1.4
  Group = -> [C_element082,H_element076,O_element078]
  conduct = 2
  density = 1
  expand = 3
  formula = G4_MYLAR
  name = G4_MYLAR
  specific = 4
FEATURE [App::DocumentObjectGroupPython] C_element083  label="C_element : 041"  # scripted group (container) (typed FeaturePython)
  n = 5
  ref = C_element
FEATURE [App::DocumentObjectGroupPython] H_element077  label="H_element : 039"  # scripted group (container) (typed FeaturePython)
  n = 8
  ref = H_element
FEATURE [App::DocumentObjectGroupPython] O_element079  label="O_element : 040"  # scripted group (container) (typed FeaturePython)
  n = 2
  ref = O_element
FEATURE [App::DocumentObjectGroupPython] G4_PLEXIGLASS  # scripted group (container) (typed FeaturePython)
  Dunit = g/cm3
  Dvalue = 1.19
  Group = -> [C_element083,H_element077,O_element079]
  conduct = 2
  density = 1
  expand = 3
  formula = G4_PLEXIGLASS
  name = G4_PLEXIGLASS
  specific = 4
FEATURE [App::DocumentObjectGroupPython] C_element084  label="C_element : 042"  # scripted group (container) (typed FeaturePython)
  n = 1
  ref = C_element
FEATURE [App::DocumentObjectGroupPython] H_element078  label="H_element : 040"  # scripted group (container) (typed FeaturePython)
  n = 2
  ref = H_element
FEATURE [App::DocumentObjectGroupPython] O_element080  label="O_element : 041"  # scripted group (container) (typed FeaturePython)
  n = 1
  ref = O_element
FEATURE [App::DocumentObjectGroupPython] G4_POLYOXYMETHYLENE  # scripted group (container) (typed FeaturePython)
  Dunit = g/cm3
  Dvalue = 1.425
  Group = -> [C_element084,H_element078,O_element080]
  conduct = 2
  density = 1
  expand = 3
  formula = G4_POLYOXYMETHYLENE
  name = G4_POLYOXYMETHYLENE
  specific = 4
FEATURE [App::DocumentObjectGroupPython] C_element085  label="C_element : 043"  # scripted group (container) (typed FeaturePython)
  n = 2
  ref = C_element
FEATURE [App::DocumentObjectGroupPython] H_element079  label="H_element : 041"  # scripted group (container) (typed FeaturePython)
  n = 4
  ref = H_element
FEATURE [App::DocumentObjectGroupPython] G4_POLYPROPYLENE  # scripted group (container) (typed FeaturePython)
  Dunit = g/cm3
  Dvalue = 0.9
  Group = -> [C_element085,H_element079]
  conduct = 2
  density = 1
  expand = 3
  formula = G4_POLYPROPYLENE
  name = G4_POLYPROPYLENE
  specific = 4
FEATURE [App::DocumentObjectGroupPython] C_element086  label="C_element : 044"  # scripted group (container) (typed FeaturePython)
  n = 8
  ref = C_element
FEATURE [App::DocumentObjectGroupPython] H_element080  label="H_element : 042"  # scripted group (container) (typed FeaturePython)
  n = 8
  ref = H_element
FEATURE [App::DocumentObjectGroupPython] G4_POLYSTYRENE  # scripted group (container) (typed FeaturePython)
  Dunit = g/cm3
  Dvalue = 1.06
  Group = -> [C_element086,H_element080]
  conduct = 2
  density = 1
  expand = 3
  formula = G4_POLYSTYRENE
  name = G4_POLYSTYRENE
  specific = 4
FEATURE [App::DocumentObjectGroupPython] C_element087  label="C_element : 045"  # scripted group (container) (typed FeaturePython)
  n = 2
  ref = C_element
FEATURE [App::DocumentObjectGroupPython] F_element014  label="F_element : 4"  # scripted group (container) (typed FeaturePython)
  n = 4
  ref = F_element
FEATURE [App::DocumentObjectGroupPython] G4_TEFLON  # scripted group (container) (typed FeaturePython)
  Dunit = g/cm3
  Dvalue = 2.2
  Group = -> [C_element087,F_element014]
  conduct = 2
  density = 1
  expand = 3
  formula = G4_TEFLON
  name = G4_TEFLON
  specific = 4
FEATURE [App::DocumentObjectGroupPython] C_element088  label="C_element : 046"  # scripted group (container) (typed FeaturePython)
  n = 2
  ref = C_element
FEATURE [App::DocumentObjectGroupPython] F_element015  label="F_element : 006"  # scripted group (container) (typed FeaturePython)
  n = 3
  ref = F_element
FEATURE [App::DocumentObjectGroupPython] Cl_element018  label="Cl_element : 008"  # scripted group (container) (typed FeaturePython)
  n = 1
  ref = Cl_element
FEATURE [App::DocumentObjectGroupPython] G4_POLYTRIFLUOROCHLOROETHYLENE  # scripted group (container) (typed FeaturePython)
  Dunit = g/cm3
  Dvalue = 2.1
  Group = -> [C_element088,F_element015,Cl_element018]
  conduct = 2
  density = 1
  expand = 3
  formula = G4_POLYTRIFLUOROCHLOROETHYLENE
  name = G4_POLYTRIFLUOROCHLOROETHYLENE
  specific = 4
FEATURE [App::DocumentObjectGroupPython] C_element089  label="C_element : 047"  # scripted group (container) (typed FeaturePython)
  n = 4
  ref = C_element
FEATURE [App::DocumentObjectGroupPython] H_element081  label="H_element : 043"  # scripted group (container) (typed FeaturePython)
  n = 6
  ref = H_element
FEATURE [App::DocumentObjectGroupPython] O_element081  label="O_element : 042"  # scripted group (container) (typed FeaturePython)
  n = 2
  ref = O_element
FEATURE [App::DocumentObjectGroupPython] G4_POLYVINYL_ACETATE  # scripted group (container) (typed FeaturePython)
  Dunit = g/cm3
  Dvalue = 1.19
  Group = -> [C_element089,H_element081,O_element081]
  conduct = 2
  density = 1
  expand = 3
  formula = G4_POLYVINYL_ACETATE
  name = G4_POLYVINYL_ACETATE
  specific = 4
FEATURE [App::DocumentObjectGroupPython] C_element090  label="C_element : 048"  # scripted group (container) (typed FeaturePython)
  n = 2
  ref = C_element
FEATURE [App::DocumentObjectGroupPython] H_element082  label="H_element : 044"  # scripted group (container) (typed FeaturePython)
  n = 4
  ref = H_element
FEATURE [App::DocumentObjectGroupPython] O_element082  label="O_element : 043"  # scripted group (container) (typed FeaturePython)
  n = 1
  ref = O_element
FEATURE [App::DocumentObjectGroupPython] G4_POLYVINYL_ALCOHOL  # scripted group (container) (typed FeaturePython)
  Dunit = g/cm3
  Dvalue = 1.3
  Group = -> [C_element090,H_element082,O_element082]
  conduct = 2
  density = 1
  expand = 3
  formula = G4_POLYVINYL_ALCOHOL
  name = G4_POLYVINYL_ALCOHOL
  specific = 4
FEATURE [App::DocumentObjectGroupPython] C_element091  label="C_element : 049"  # scripted group (container) (typed FeaturePython)
  n = 8
  ref = C_element
FEATURE [App::DocumentObjectGroupPython] H_element083  label="H_element : 045"  # scripted group (container) (typed FeaturePython)
  n = 14
  ref = H_element
FEATURE [App::DocumentObjectGroupPython] O_element083  label="O_element : 044"  # scripted group (container) (typed FeaturePython)
  n = 2
  ref = O_element
FEATURE [App::DocumentObjectGroupPython] G4_POLYVINYL_BUTYRAL  # scripted group (container) (typed FeaturePython)
  Dunit = g/cm3
  Dvalue = 1.12
  Group = -> [C_element091,H_element083,O_element083]
  conduct = 2
  density = 1
  expand = 3
  formula = G4_POLYVINYL_BUTYRAL
  name = G4_POLYVINYL_BUTYRAL
  specific = 4
FEATURE [App::DocumentObjectGroupPython] C_element092  label="C_element : 050"  # scripted group (container) (typed FeaturePython)
  n = 2
  ref = C_element
FEATURE [App::DocumentObjectGroupPython] H_element084  label="H_element : 046"  # scripted group (container) (typed FeaturePython)
  n = 3
  ref = H_element
FEATURE [App::DocumentObjectGroupPython] Cl_element019  label="Cl_element : 009"  # scripted group (container) (typed FeaturePython)
  n = 1
  ref = Cl_element
FEATURE [App::DocumentObjectGroupPython] G4_POLYVINYL_CHLORIDE  # scripted group (container) (typed FeaturePython)
  Dunit = g/cm3
  Dvalue = 1.3
  Group = -> [C_element092,H_element084,Cl_element019]
  conduct = 2
  density = 1
  expand = 3
  formula = G4_POLYVINYL_CHLORIDE
  name = G4_POLYVINYL_CHLORIDE
  specific = 4
FEATURE [App::DocumentObjectGroupPython] C_element093  label="C_element : 051"  # scripted group (container) (typed FeaturePython)
  n = 2
  ref = C_element
FEATURE [App::DocumentObjectGroupPython] H_element085  label="H_element : 047"  # scripted group (container) (typed FeaturePython)
  n = 2
  ref = H_element
FEATURE [App::DocumentObjectGroupPython] Cl_element020  label="Cl_element : 010"  # scripted group (container) (typed FeaturePython)
  n = 2
  ref = Cl_element
FEATURE [App::DocumentObjectGroupPython] G4_POLYVINYLIDENE_CHLORIDE  # scripted group (container) (typed FeaturePython)
  Dunit = g/cm3
  Dvalue = 1.7
  Group = -> [C_element093,H_element085,Cl_element020]
  conduct = 2
  density = 1
  expand = 3
  formula = G4_POLYVINYLIDENE_CHLORIDE
  name = G4_POLYVINYLIDENE_CHLORIDE
  specific = 4
FEATURE [App::DocumentObjectGroupPython] C_element094  label="C_element : 052"  # scripted group (container) (typed FeaturePython)
  n = 2
  ref = C_element
FEATURE [App::DocumentObjectGroupPython] H_element086  label="H_element : 048"  # scripted group (container) (typed FeaturePython)
  n = 2
  ref = H_element
FEATURE [App::DocumentObjectGroupPython] F_element016  label="F_element : 007"  # scripted group (container) (typed FeaturePython)
  n = 2
  ref = F_element
FEATURE [App::DocumentObjectGroupPython] G4_POLYVINYLIDENE_FLUORIDE  # scripted group (container) (typed FeaturePython)
  Dunit = g/cm3
  Dvalue = 1.76
  Group = -> [C_element094,H_element086,F_element016]
  conduct = 2
  density = 1
  expand = 3
  formula = G4_POLYVINYLIDENE_FLUORIDE
  name = G4_POLYVINYLIDENE_FLUORIDE
  specific = 4
FEATURE [App::DocumentObjectGroupPython] C_element095  label="C_element : 053"  # scripted group (container) (typed FeaturePython)
  n = 6
  ref = C_element
FEATURE [App::DocumentObjectGroupPython] H_element087  label="H_element : 9"  # scripted group (container) (typed FeaturePython)
  n = 9
  ref = H_element
FEATURE [App::DocumentObjectGroupPython] N_element037  label="N_element : 016"  # scripted group (container) (typed FeaturePython)
  n = 1
  ref = N_element
FEATURE [App::DocumentObjectGroupPython] O_element084  label="O_element : 045"  # scripted group (container) (typed FeaturePython)
  n = 1
  ref = O_element
FEATURE [App::DocumentObjectGroupPython] G4_POLYVINYL_PYRROLIDONE  # scripted group (container) (typed FeaturePython)
  Dunit = g/cm3
  Dvalue = 1.25
  Group = -> [C_element095,H_element087,N_element037,O_element084]
  conduct = 2
  density = 1
  expand = 3
  formula = G4_POLYVINYL_PYRROLIDONE
  name = G4_POLYVINYL_PYRROLIDONE
  specific = 4
FEATURE [App::DocumentObjectGroupPython] K_element008  label="K_element : 1"  # scripted group (container) (typed FeaturePython)
  n = 1
  ref = K_element
FEATURE [App::DocumentObjectGroupPython] I_element006  label="I_element : 003"  # scripted group (container) (typed FeaturePython)
  n = 1
  ref = I_element
FEATURE [App::DocumentObjectGroupPython] G4_POTASSIUM_IODIDE  # scripted group (container) (typed FeaturePython)
  Dunit = g/cm3
  Dvalue = 3.13
  Group = -> [K_element008,I_element006]
  conduct = 2
  density = 1
  expand = 3
  formula = G4_POTASSIUM_IODIDE
  name = G4_POTASSIUM_IODIDE
  specific = 4
FEATURE [App::DocumentObjectGroupPython] K_element009  label="K_element : 2"  # scripted group (container) (typed FeaturePython)
  n = 2
  ref = K_element
FEATURE [App::DocumentObjectGroupPython] O_element085  label="O_element : 046"  # scripted group (container) (typed FeaturePython)
  n = 1
  ref = O_element
FEATURE [App::DocumentObjectGroupPython] G4_POTASSIUM_OXIDE  # scripted group (container) (typed FeaturePython)
  Dunit = g/cm3
  Dvalue = 2.32
  Group = -> [K_element009,O_element085]
  conduct = 2
  density = 1
  expand = 3
  formula = G4_POTASSIUM_OXIDE
  name = G4_POTASSIUM_OXIDE
  specific = 4
FEATURE [App::DocumentObjectGroupPython] C_element096  label="C_element : 054"  # scripted group (container) (typed FeaturePython)
  n = 3
  ref = C_element
FEATURE [App::DocumentObjectGroupPython] H_element088  label="H_element : 049"  # scripted group (container) (typed FeaturePython)
  n = 8
  ref = H_element
FEATURE [App::DocumentObjectGroupPython] G4_PROPANE  # scripted group (container) (typed FeaturePython)
  Dunit = g/cm3
  Dvalue = 0.00187939
  Group = -> [C_element096,H_element088]
  conduct = 2
  density = 1
  expand = 3
  formula = G4_PROPANE
  name = G4_PROPANE
  specific = 4
FEATURE [App::DocumentObjectGroupPython] C_element097  label="C_element : 055"  # scripted group (container) (typed FeaturePython)
  n = 3
  ref = C_element
FEATURE [App::DocumentObjectGroupPython] H_element089  label="H_element : 050"  # scripted group (container) (typed FeaturePython)
  n = 8
  ref = H_element
FEATURE [App::DocumentObjectGroupPython] G4_lPROPANE  # scripted group (container) (typed FeaturePython)
  Dunit = g/cm3
  Dvalue = 0.43
  Group = -> [C_element097,H_element089]
  conduct = 2
  density = 1
  expand = 3
  formula = G4_lPROPANE
  name = G4_lPROPANE
  specific = 4
FEATURE [App::DocumentObjectGroupPython] C_element098  label="C_element : 056"  # scripted group (container) (typed FeaturePython)
  n = 3
  ref = C_element
FEATURE [App::DocumentObjectGroupPython] H_element090  label="H_element : 051"  # scripted group (container) (typed FeaturePython)
  n = 8
  ref = H_element
FEATURE [App::DocumentObjectGroupPython] O_element086  label="O_element : 047"  # scripted group (container) (typed FeaturePython)
  n = 1
  ref = O_element
FEATURE [App::DocumentObjectGroupPython] G4_N_PROPYL_ALCOHOL  label="G4_N-PROPYL_ALCOHOL"  # scripted group (container) (typed FeaturePython)
  Dunit = g/cm3
  Dvalue = 0.8035
  Group = -> [C_element098,H_element090,O_element086]
  conduct = 2
  density = 1
  expand = 3
  formula = G4_N-PROPYL_ALCOHOL
  name = G4_N-PROPYL_ALCOHOL
  specific = 4
FEATURE [App::DocumentObjectGroupPython] C_element099  label="C_element : 057"  # scripted group (container) (typed FeaturePython)
  n = 5
  ref = C_element
FEATURE [App::DocumentObjectGroupPython] H_element091  label="H_element : 052"  # scripted group (container) (typed FeaturePython)
  n = 5
  ref = H_element
FEATURE [App::DocumentObjectGroupPython] N_element038  label="N_element : 017"  # scripted group (container) (typed FeaturePython)
  n = 1
  ref = N_element
FEATURE [App::DocumentObjectGroupPython] G4_PYRIDINE  # scripted group (container) (typed FeaturePython)
  Dunit = g/cm3
  Dvalue = 0.9819
  Group = -> [C_element099,H_element091,N_element038]
  conduct = 2
  density = 1
  expand = 3
  formula = G4_PYRIDINE
  name = G4_PYRIDINE
  specific = 4
FEATURE [App::DocumentObjectGroupPython] H_element092  label="H_element : 0.144"  # scripted group (container) (typed FeaturePython)
  n = 0.143711
FEATURE [App::DocumentObjectGroupPython] C_element100  label="C_element : 0.856"  # scripted group (container) (typed FeaturePython)
  n = 0.856289
FEATURE [App::DocumentObjectGroupPython] G4_RUBBER_BUTYL  # scripted group (container) (typed FeaturePython)
  Dunit = g/cm3
  Dvalue = 0.92
  Group = -> [H_element092,C_element100]
  conduct = 2
  density = 1
  expand = 3
  formula = G4_RUBBER_BUTYL
  name = G4_RUBBER_BUTYL
  specific = 4
FEATURE [App::DocumentObjectGroupPython] H_element093  label="H_element : 0.118"  # scripted group (container) (typed FeaturePython)
  n = 0.118371
FEATURE [App::DocumentObjectGroupPython] C_element101  label="C_element : 0.882"  # scripted group (container) (typed FeaturePython)
  n = 0.881629
FEATURE [App::DocumentObjectGroupPython] G4_RUBBER_NATURAL  # scripted group (container) (typed FeaturePython)
  Dunit = g/cm3
  Dvalue = 0.92
  Group = -> [H_element093,C_element101]
  conduct = 2
  density = 1
  expand = 3
  formula = G4_RUBBER_NATURAL
  name = G4_RUBBER_NATURAL
  specific = 4
FEATURE [App::DocumentObjectGroupPython] H_element094  label="H_element : 0.145"  # scripted group (container) (typed FeaturePython)
  n = 0.05692
FEATURE [App::DocumentObjectGroupPython] C_element102  label="C_element : 0.543"  # scripted group (container) (typed FeaturePython)
  n = 0.542646
FEATURE [App::DocumentObjectGroupPython] Cl_element021  label="Cl_element : 0.400"  # scripted group (container) (typed FeaturePython)
  n = 0.400434
FEATURE [App::DocumentObjectGroupPython] G4_RUBBER_NEOPRENE  # scripted group (container) (typed FeaturePython)
  Dunit = g/cm3
  Dvalue = 1.23
  Group = -> [H_element094,C_element102,Cl_element021]
  conduct = 2
  density = 1
  expand = 3
  formula = G4_RUBBER_NEOPRENE
  name = G4_RUBBER_NEOPRENE
  specific = 4
FEATURE [App::DocumentObjectGroupPython] Si_element006  label="Si_element : 1"  # scripted group (container) (typed FeaturePython)
  n = 1
  ref = Si_element
FEATURE [App::DocumentObjectGroupPython] O_element087  label="O_element : 048"  # scripted group (container) (typed FeaturePython)
  n = 2
  ref = O_element
FEATURE [App::DocumentObjectGroupPython] G4_SILICON_DIOXIDE  # scripted group (container) (typed FeaturePython)
  Dunit = g/cm3
  Dvalue = 2.32
  Group = -> [Si_element006,O_element087]
  conduct = 2
  density = 1
  expand = 3
  formula = G4_SILICON_DIOXIDE
  name = G4_SILICON_DIOXIDE
  specific = 4
FEATURE [App::DocumentObjectGroupPython] Ag_element002  label="Ag_element : 1"  # scripted group (container) (typed FeaturePython)
  n = 1
  ref = Ag_element
FEATURE [App::DocumentObjectGroupPython] Br_element005  label="Br_element : 003"  # scripted group (container) (typed FeaturePython)
  n = 1
  ref = Br_element
FEATURE [App::DocumentObjectGroupPython] G4_SILVER_BROMIDE  # scripted group (container) (typed FeaturePython)
  Dunit = g/cm3
  Dvalue = 6.473
  Group = -> [Ag_element002,Br_element005]
  conduct = 2
  density = 1
  expand = 3
  formula = G4_SILVER_BROMIDE
  name = G4_SILVER_BROMIDE
  specific = 4
FEATURE [App::DocumentObjectGroupPython] Ag_element003  label="Ag_element : 002"  # scripted group (container) (typed FeaturePython)
  n = 1
  ref = Ag_element
FEATURE [App::DocumentObjectGroupPython] Cl_element022  label="Cl_element : 011"  # scripted group (container) (typed FeaturePython)
  n = 1
  ref = Cl_element
FEATURE [App::DocumentObjectGroupPython] G4_SILVER_CHLORIDE  # scripted group (container) (typed FeaturePython)
  Dunit = g/cm3
  Dvalue = 5.56
  Group = -> [Ag_element003,Cl_element022]
  conduct = 2
  density = 1
  expand = 3
  formula = G4_SILVER_CHLORIDE
  name = G4_SILVER_CHLORIDE
  specific = 4
FEATURE [App::DocumentObjectGroupPython] Br_element006  label="Br_element : 0.423"  # scripted group (container) (typed FeaturePython)
  n = 0.422895
FEATURE [App::DocumentObjectGroupPython] Ag_element004  label="Ag_element : 0.574"  # scripted group (container) (typed FeaturePython)
  n = 0.573748
FEATURE [App::DocumentObjectGroupPython] I_element007  label="I_element : 0.649"  # scripted group (container) (typed FeaturePython)
  n = 0.003357
FEATURE [App::DocumentObjectGroupPython] G4_SILVER_HALIDES  # scripted group (container) (typed FeaturePython)
  Dunit = g/cm3
  Dvalue = 6.47
  Group = -> [Br_element006,Ag_element004,I_element007]
  conduct = 2
  density = 1
  expand = 3
  formula = G4_SILVER_HALIDES
  name = G4_SILVER_HALIDES
  specific = 4
FEATURE [App::DocumentObjectGroupPython] Ag_element005  label="Ag_element : 003"  # scripted group (container) (typed FeaturePython)
  n = 1
  ref = Ag_element
FEATURE [App::DocumentObjectGroupPython] I_element008  label="I_element : 004"  # scripted group (container) (typed FeaturePython)
  n = 1
  ref = I_element
FEATURE [App::DocumentObjectGroupPython] G4_SILVER_IODIDE  # scripted group (container) (typed FeaturePython)
  Dunit = g/cm3
  Dvalue = 6.01
  Group = -> [Ag_element005,I_element008]
  conduct = 2
  density = 1
  expand = 3
  formula = G4_SILVER_IODIDE
  name = G4_SILVER_IODIDE
  specific = 4
FEATURE [App::DocumentObjectGroupPython] H_element095  label="H_element : 0.100"  # scripted group (container) (typed FeaturePython)
  n = 0.1
FEATURE [App::DocumentObjectGroupPython] C_element103  label="C_element : 0.204"  # scripted group (container) (typed FeaturePython)
  n = 0.204
FEATURE [App::DocumentObjectGroupPython] N_element039  label="N_element : 0.759"  # scripted group (container) (typed FeaturePython)
  n = 0.042
FEATURE [App::DocumentObjectGroupPython] O_element088  label="O_element : 0.645"  # scripted group (container) (typed FeaturePython)
  n = 0.645
FEATURE [App::DocumentObjectGroupPython] Na_element013  label="Na_element : 0.100"  # scripted group (container) (typed FeaturePython)
  n = 0.002
FEATURE [App::DocumentObjectGroupPython] P_element009  label="P_element : 0.107"  # scripted group (container) (typed FeaturePython)
  n = 0.001
FEATURE [App::DocumentObjectGroupPython] S_element020  label="S_element : 0.021"  # scripted group (container) (typed FeaturePython)
  n = 0.002
FEATURE [App::DocumentObjectGroupPython] Cl_element023  label="Cl_element : 0.590"  # scripted group (container) (typed FeaturePython)
  n = 0.003
FEATURE [App::DocumentObjectGroupPython] K_element010  label="K_element : 0.001"  # scripted group (container) (typed FeaturePython)
  n = 0.001
FEATURE [App::DocumentObjectGroupPython] G4_SKIN_ICRP  # scripted group (container) (typed FeaturePython)
  Dunit = g/cm3
  Dvalue = 1.09
  Group = -> [H_element095,C_element103,N_element039,O_element088,Na_element013,P_element009,S_element020,Cl_element023,K_element010]
  conduct = 2
  density = 1
  expand = 3
  formula = G4_SKIN_ICRP
  name = G4_SKIN_ICRP
  specific = 4
FEATURE [App::DocumentObjectGroupPython] Na_element014  label="Na_element : 2"  # scripted group (container) (typed FeaturePython)
  n = 2
  ref = Na_element
FEATURE [App::DocumentObjectGroupPython] C_element104  label="C_element : 058"  # scripted group (container) (typed FeaturePython)
  n = 1
  ref = C_element
FEATURE [App::DocumentObjectGroupPython] O_element089  label="O_element : 049"  # scripted group (container) (typed FeaturePython)
  n = 3
  ref = O_element
FEATURE [App::DocumentObjectGroupPython] G4_SODIUM_CARBONATE  # scripted group (container) (typed FeaturePython)
  Dunit = g/cm3
  Dvalue = 2.532
  Group = -> [Na_element014,C_element104,O_element089]
  conduct = 2
  density = 1
  expand = 3
  formula = G4_SODIUM_CARBONATE
  name = G4_SODIUM_CARBONATE
  specific = 4
FEATURE [App::DocumentObjectGroupPython] Na_element015  label="Na_element : 1"  # scripted group (container) (typed FeaturePython)
  n = 1
  ref = Na_element
FEATURE [App::DocumentObjectGroupPython] I_element009  label="I_element : 005"  # scripted group (container) (typed FeaturePython)
  n = 1
  ref = I_element
FEATURE [App::DocumentObjectGroupPython] G4_SODIUM_IODIDE  # scripted group (container) (typed FeaturePython)
  Dunit = g/cm3
  Dvalue = 3.667
  Group = -> [Na_element015,I_element009]
  conduct = 2
  density = 1
  expand = 3
  formula = G4_SODIUM_IODIDE
  name = G4_SODIUM_IODIDE
  specific = 4
FEATURE [App::DocumentObjectGroupPython] Na_element016  label="Na_element : 003"  # scripted group (container) (typed FeaturePython)
  n = 2
  ref = Na_element
FEATURE [App::DocumentObjectGroupPython] O_element090  label="O_element : 050"  # scripted group (container) (typed FeaturePython)
  n = 1
  ref = O_element
FEATURE [App::DocumentObjectGroupPython] G4_SODIUM_MONOXIDE  # scripted group (container) (typed FeaturePython)
  Dunit = g/cm3
  Dvalue = 2.27
  Group = -> [Na_element016,O_element090]
  conduct = 2
  density = 1
  expand = 3
  formula = G4_SODIUM_MONOXIDE
  name = G4_SODIUM_MONOXIDE
  specific = 4
FEATURE [App::DocumentObjectGroupPython] Na_element017  label="Na_element : 004"  # scripted group (container) (typed FeaturePython)
  n = 1
  ref = Na_element
FEATURE [App::DocumentObjectGroupPython] N_element040  label="N_element : 018"  # scripted group (container) (typed FeaturePython)
  n = 1
  ref = N_element
FEATURE [App::DocumentObjectGroupPython] O_element091  label="O_element : 051"  # scripted group (container) (typed FeaturePython)
  n = 3
  ref = O_element
FEATURE [App::DocumentObjectGroupPython] G4_SODIUM_NITRATE  # scripted group (container) (typed FeaturePython)
  Dunit = g/cm3
  Dvalue = 2.261
  Group = -> [Na_element017,N_element040,O_element091]
  conduct = 2
  density = 1
  expand = 3
  formula = G4_SODIUM_NITRATE
  name = G4_SODIUM_NITRATE
  specific = 4
FEATURE [App::DocumentObjectGroupPython] C_element105  label="C_element : 059"  # scripted group (container) (typed FeaturePython)
  n = 14
  ref = C_element
FEATURE [App::DocumentObjectGroupPython] H_element096  label="H_element : 053"  # scripted group (container) (typed FeaturePython)
  n = 12
  ref = H_element
FEATURE [App::DocumentObjectGroupPython] G4_STILBENE  # scripted group (container) (typed FeaturePython)
  Dunit = g/cm3
  Dvalue = 0.9707
  Group = -> [C_element105,H_element096]
  conduct = 2
  density = 1
  expand = 3
  formula = G4_STILBENE
  name = G4_STILBENE
  specific = 4
FEATURE [App::DocumentObjectGroupPython] C_element106  label="C_element : 12"  # scripted group (container) (typed FeaturePython)
  n = 12
  ref = C_element
FEATURE [App::DocumentObjectGroupPython] H_element097  label="H_element : 22"  # scripted group (container) (typed FeaturePython)
  n = 22
  ref = H_element
FEATURE [App::DocumentObjectGroupPython] O_element092  label="O_element : 11"  # scripted group (container) (typed FeaturePython)
  n = 11
  ref = O_element
FEATURE [App::DocumentObjectGroupPython] G4_SUCROSE  # scripted group (container) (typed FeaturePython)
  Dunit = g/cm3
  Dvalue = 1.5805
  Group = -> [C_element106,H_element097,O_element092]
  conduct = 2
  density = 1
  expand = 3
  formula = G4_SUCROSE
  name = G4_SUCROSE
  specific = 4
FEATURE [App::DocumentObjectGroupPython] C_element107  label="C_element : 18"  # scripted group (container) (typed FeaturePython)
  n = 18
  ref = C_element
FEATURE [App::DocumentObjectGroupPython] H_element098  label="H_element : 054"  # scripted group (container) (typed FeaturePython)
  n = 14
  ref = H_element
FEATURE [App::DocumentObjectGroupPython] G4_TERPHENYL  # scripted group (container) (typed FeaturePython)
  Dunit = g/cm3
  Dvalue = 1.24
  Group = -> [C_element107,H_element098]
  conduct = 2
  density = 1
  expand = 3
  formula = G4_TERPHENYL
  name = G4_TERPHENYL
  specific = 4
FEATURE [App::DocumentObjectGroupPython] H_element099  label="H_element : 0.146"  # scripted group (container) (typed FeaturePython)
  n = 0.106
FEATURE [App::DocumentObjectGroupPython] C_element108  label="C_element : 0.883"  # scripted group (container) (typed FeaturePython)
  n = 0.099
FEATURE [App::DocumentObjectGroupPython] N_element041  label="N_element : 0.020"  # scripted group (container) (typed FeaturePython)
  n = 0.02
FEATURE [App::DocumentObjectGroupPython] O_element093  label="O_element : 0.766"  # scripted group (container) (typed FeaturePython)
  n = 0.766
FEATURE [App::DocumentObjectGroupPython] Na_element018  label="Na_element : 0.101"  # scripted group (container) (typed FeaturePython)
  n = 0.002
FEATURE [App::DocumentObjectGroupPython] P_element010  label="P_element : 0.108"  # scripted group (container) (typed FeaturePython)
  n = 0.001
FEATURE [App::DocumentObjectGroupPython] S_element021  label="S_element : 0.022"  # scripted group (container) (typed FeaturePython)
  n = 0.002
FEATURE [App::DocumentObjectGroupPython] Cl_element024  label="Cl_element : 0.002"  # scripted group (container) (typed FeaturePython)
  n = 0.002
FEATURE [App::DocumentObjectGroupPython] K_element011  label="K_element : 0.017"  # scripted group (container) (typed FeaturePython)
  n = 0.002
FEATURE [App::DocumentObjectGroupPython] G4_TESTIS_ICRP  # scripted group (container) (typed FeaturePython)
  Dunit = g/cm3
  Dvalue = 1.04
  Group = -> [H_element099,C_element108,N_element041,O_element093,Na_element018,P_element010,S_element021,Cl_element024,K_element011]
  conduct = 2
  density = 1
  expand = 3
  formula = G4_TESTIS_ICRP
  name = G4_TESTIS_ICRP
  specific = 4
FEATURE [App::DocumentObjectGroupPython] C_element109  label="C_element : 060"  # scripted group (container) (typed FeaturePython)
  n = 2
  ref = C_element
FEATURE [App::DocumentObjectGroupPython] Cl_element025  label="Cl_element : 012"  # scripted group (container) (typed FeaturePython)
  n = 4
  ref = Cl_element
FEATURE [App::DocumentObjectGroupPython] G4_TETRACHLOROETHYLENE  # scripted group (container) (typed FeaturePython)
  Dunit = g/cm3
  Dvalue = 1.625
  Group = -> [C_element109,Cl_element025]
  conduct = 2
  density = 1
  expand = 3
  formula = G4_TETRACHLOROETHYLENE
  name = G4_TETRACHLOROETHYLENE
  specific = 4
FEATURE [App::DocumentObjectGroupPython] Tl_element001  label="Tl_element : 1"  # scripted group (container) (typed FeaturePython)
  n = 1
  ref = Tl_element
FEATURE [App::DocumentObjectGroupPython] Cl_element026  label="Cl_element : 013"  # scripted group (container) (typed FeaturePython)
  n = 1
  ref = Cl_element
FEATURE [App::DocumentObjectGroupPython] G4_THALLIUM_CHLORIDE  # scripted group (container) (typed FeaturePython)
  Dunit = g/cm3
  Dvalue = 7.004
  Group = -> [Tl_element001,Cl_element026]
  conduct = 2
  density = 1
  expand = 3
  formula = G4_THALLIUM_CHLORIDE
  name = G4_THALLIUM_CHLORIDE
  specific = 4
FEATURE [App::DocumentObjectGroupPython] H_element100  label="H_element : 0.147"  # scripted group (container) (typed FeaturePython)
  n = 0.105
FEATURE [App::DocumentObjectGroupPython] C_element110  label="C_element : 0.256"  # scripted group (container) (typed FeaturePython)
  n = 0.256
FEATURE [App::DocumentObjectGroupPython] N_element042  label="N_element : 0.760"  # scripted group (container) (typed FeaturePython)
  n = 0.027
FEATURE [App::DocumentObjectGroupPython] O_element094  label="O_element : 0.602"  # scripted group (container) (typed FeaturePython)
  n = 0.602
FEATURE [App::DocumentObjectGroupPython] Na_element019  label="Na_element : 0.102"  # scripted group (container) (typed FeaturePython)
  n = 0.001
FEATURE [App::DocumentObjectGroupPython] P_element011  label="P_element : 0.109"  # scripted group (container) (typed FeaturePython)
  n = 0.002
FEATURE [App::DocumentObjectGroupPython] S_element022  label="S_element : 0.023"  # scripted group (container) (typed FeaturePython)
  n = 0.003
FEATURE [App::DocumentObjectGroupPython] Cl_element027  label="Cl_element : 0.591"  # scripted group (container) (typed FeaturePython)
  n = 0.002
FEATURE [App::DocumentObjectGroupPython] K_element012  label="K_element : 0.018"  # scripted group (container) (typed FeaturePython)
  n = 0.002
FEATURE [App::DocumentObjectGroupPython] G4_TISSUE_SOFT_ICRP  # scripted group (container) (typed FeaturePython)
  Dunit = g/cm3
  Dvalue = 1.03
  Group = -> [H_element100,C_element110,N_element042,O_element094,Na_element019,P_element011,S_element022,Cl_element027,K_element012]
  conduct = 2
  density = 1
  expand = 3
  formula = G4_TISSUE_SOFT_ICRP
  name = G4_TISSUE_SOFT_ICRP
  specific = 4
FEATURE [App::DocumentObjectGroupPython] H_element101  label="H_element : 0.148"  # scripted group (container) (typed FeaturePython)
  n = 0.101
FEATURE [App::DocumentObjectGroupPython] C_element111  label="C_element : 0.111"  # scripted group (container) (typed FeaturePython)
  n = 0.111
FEATURE [App::DocumentObjectGroupPython] N_element043  label="N_element : 0.026"  # scripted group (container) (typed FeaturePython)
  n = 0.026
FEATURE [App::DocumentObjectGroupPython] O_element095  label="O_element : 0.762"  # scripted group (container) (typed FeaturePython)
  n = 0.762
FEATURE [App::DocumentObjectGroupPython] G4_TISSUE_SOFT_ICRU_4  label="G4_TISSUE_SOFT_ICRU-4"  # scripted group (container) (typed FeaturePython)
  Dunit = g/cm3
  Dvalue = 1
  Group = -> [H_element101,C_element111,N_element043,O_element095]
  conduct = 2
  density = 1
  expand = 3
  formula = G4_TISSUE_SOFT_ICRU-4
  name = G4_TISSUE_SOFT_ICRU-4
  specific = 4
FEATURE [App::DocumentObjectGroupPython] H_element102  label="H_element : 0.149"  # scripted group (container) (typed FeaturePython)
  n = 0.101869
FEATURE [App::DocumentObjectGroupPython] C_element112  label="C_element : 0.456"  # scripted group (container) (typed FeaturePython)
  n = 0.456179
FEATURE [App::DocumentObjectGroupPython] N_element044  label="N_element : 0.761"  # scripted group (container) (typed FeaturePython)
  n = 0.035172
FEATURE [App::DocumentObjectGroupPython] O_element096  label="O_element : 0.407"  # scripted group (container) (typed FeaturePython)
  n = 0.40678
FEATURE [App::DocumentObjectGroupPython] G4_TISSUE_METHANE  label="G4_TISSUE-METHANE"  # scripted group (container) (typed FeaturePython)
  Dunit = g/cm3
  Dvalue = 0.00106409
  Group = -> [H_element102,C_element112,N_element044,O_element096]
  conduct = 2
  density = 1
  expand = 3
  formula = G4_TISSUE-METHANE
  name = G4_TISSUE-METHANE
  specific = 4
FEATURE [App::DocumentObjectGroupPython] H_element103  label="H_element : 0.103"  # scripted group (container) (typed FeaturePython)
  n = 0.102672
FEATURE [App::DocumentObjectGroupPython] C_element113  label="C_element : 0.569"  # scripted group (container) (typed FeaturePython)
  n = 0.56894
FEATURE [App::DocumentObjectGroupPython] N_element045  label="N_element : 0.762"  # scripted group (container) (typed FeaturePython)
  n = 0.035022
FEATURE [App::DocumentObjectGroupPython] O_element097  label="O_element : 0.293"  # scripted group (container) (typed FeaturePython)
  n = 0.293366
FEATURE [App::DocumentObjectGroupPython] G4_TISSUE_PROPANE  label="G4_TISSUE-PROPANE"  # scripted group (container) (typed FeaturePython)
  Dunit = g/cm3
  Dvalue = 0.00182628
  Group = -> [H_element103,C_element113,N_element045,O_element097]
  conduct = 2
  density = 1
  expand = 3
  formula = G4_TISSUE-PROPANE
  name = G4_TISSUE-PROPANE
  specific = 4
FEATURE [App::DocumentObjectGroupPython] Ti_element003  label="Ti_element : 1"  # scripted group (container) (typed FeaturePython)
  n = 1
  ref = Ti_element
FEATURE [App::DocumentObjectGroupPython] O_element098  label="O_element : 052"  # scripted group (container) (typed FeaturePython)
  n = 2
  ref = O_element
FEATURE [App::DocumentObjectGroupPython] G4_TITANIUM_DIOXIDE  # scripted group (container) (typed FeaturePython)
  Dunit = g/cm3
  Dvalue = 4.26
  Group = -> [Ti_element003,O_element098]
  conduct = 2
  density = 1
  expand = 3
  formula = G4_TITANIUM_DIOXIDE
  name = G4_TITANIUM_DIOXIDE
  specific = 4
FEATURE [App::DocumentObjectGroupPython] C_element114  label="C_element : 061"  # scripted group (container) (typed FeaturePython)
  n = 7
  ref = C_element
FEATURE [App::DocumentObjectGroupPython] H_element104  label="H_element : 055"  # scripted group (container) (typed FeaturePython)
  n = 8
  ref = H_element
FEATURE [App::DocumentObjectGroupPython] G4_TOLUENE  # scripted group (container) (typed FeaturePython)
  Dunit = g/cm3
  Dvalue = 0.8669
  Group = -> [C_element114,H_element104]
  conduct = 2
  density = 1
  expand = 3
  formula = G4_TOLUENE
  name = G4_TOLUENE
  specific = 4
FEATURE [App::DocumentObjectGroupPython] C_element115  label="C_element : 062"  # scripted group (container) (typed FeaturePython)
  n = 2
  ref = C_element
FEATURE [App::DocumentObjectGroupPython] H_element105  label="H_element : 056"  # scripted group (container) (typed FeaturePython)
  n = 1
  ref = H_element
FEATURE [App::DocumentObjectGroupPython] Cl_element028  label="Cl_element : 014"  # scripted group (container) (typed FeaturePython)
  n = 3
  ref = Cl_element
FEATURE [App::DocumentObjectGroupPython] G4_TRICHLOROETHYLENE  # scripted group (container) (typed FeaturePython)
  Dunit = g/cm3
  Dvalue = 1.46
  Group = -> [C_element115,H_element105,Cl_element028]
  conduct = 2
  density = 1
  expand = 3
  formula = G4_TRICHLOROETHYLENE
  name = G4_TRICHLOROETHYLENE
  specific = 4
FEATURE [App::DocumentObjectGroupPython] C_element116  label="C_element : 063"  # scripted group (container) (typed FeaturePython)
  n = 6
  ref = C_element
FEATURE [App::DocumentObjectGroupPython] H_element106  label="H_element : 15"  # scripted group (container) (typed FeaturePython)
  n = 15
  ref = H_element
FEATURE [App::DocumentObjectGroupPython] O_element099  label="O_element : 053"  # scripted group (container) (typed FeaturePython)
  n = 4
  ref = O_element
FEATURE [App::DocumentObjectGroupPython] P_element012  label="P_element : 1"  # scripted group (container) (typed FeaturePython)
  n = 1
  ref = P_element
FEATURE [App::DocumentObjectGroupPython] G4_TRIETHYL_PHOSPHATE  # scripted group (container) (typed FeaturePython)
  Dunit = g/cm3
  Dvalue = 1.07
  Group = -> [C_element116,H_element106,O_element099,P_element012]
  conduct = 2
  density = 1
  expand = 3
  formula = G4_TRIETHYL_PHOSPHATE
  name = G4_TRIETHYL_PHOSPHATE
  specific = 4
FEATURE [App::DocumentObjectGroupPython] W_element003  label="W_element : 003"  # scripted group (container) (typed FeaturePython)
  n = 1
  ref = W_element
FEATURE [App::DocumentObjectGroupPython] F_element017  label="F_element : 6"  # scripted group (container) (typed FeaturePython)
  n = 6
  ref = F_element
FEATURE [App::DocumentObjectGroupPython] G4_TUNGSTEN_HEXAFLUORIDE  # scripted group (container) (typed FeaturePython)
  Dunit = g/cm3
  Dvalue = 2.4
  Group = -> [W_element003,F_element017]
  conduct = 2
  density = 1
  expand = 3
  formula = G4_TUNGSTEN_HEXAFLUORIDE
  name = G4_TUNGSTEN_HEXAFLUORIDE
  specific = 4
FEATURE [App::DocumentObjectGroupPython] U_element001  label="U_element : 1"  # scripted group (container) (typed FeaturePython)
  n = 1
  ref = U_element
FEATURE [App::DocumentObjectGroupPython] C_element117  label="C_element : 064"  # scripted group (container) (typed FeaturePython)
  n = 2
  ref = C_element
FEATURE [App::DocumentObjectGroupPython] G4_URANIUM_DICARBIDE  # scripted group (container) (typed FeaturePython)
  Dunit = g/cm3
  Dvalue = 11.28
  Group = -> [U_element001,C_element117]
  conduct = 2
  density = 1
  expand = 3
  formula = G4_URANIUM_DICARBIDE
  name = G4_URANIUM_DICARBIDE
  specific = 4
FEATURE [App::DocumentObjectGroupPython] U_element002  label="U_element : 002"  # scripted group (container) (typed FeaturePython)
  n = 1
  ref = U_element
FEATURE [App::DocumentObjectGroupPython] C_element118  label="C_element : 065"  # scripted group (container) (typed FeaturePython)
  n = 1
  ref = C_element
FEATURE [App::DocumentObjectGroupPython] G4_URANIUM_MONOCARBIDE  # scripted group (container) (typed FeaturePython)
  Dunit = g/cm3
  Dvalue = 13.63
  Group = -> [U_element002,C_element118]
  conduct = 2
  density = 1
  expand = 3
  formula = G4_URANIUM_MONOCARBIDE
  name = G4_URANIUM_MONOCARBIDE
  specific = 4
FEATURE [App::DocumentObjectGroupPython] U_element003  label="U_element : 003"  # scripted group (container) (typed FeaturePython)
  n = 1
  ref = U_element
FEATURE [App::DocumentObjectGroupPython] O_element100  label="O_element : 054"  # scripted group (container) (typed FeaturePython)
  n = 2
  ref = O_element
FEATURE [App::DocumentObjectGroupPython] G4_URANIUM_OXIDE  # scripted group (container) (typed FeaturePython)
  Dunit = g/cm3
  Dvalue = 10.96
  Group = -> [U_element003,O_element100]
  conduct = 2
  density = 1
  expand = 3
  formula = G4_URANIUM_OXIDE
  name = G4_URANIUM_OXIDE
  specific = 4
FEATURE [App::DocumentObjectGroupPython] C_element119  label="C_element : 066"  # scripted group (container) (typed FeaturePython)
  n = 1
  ref = C_element
FEATURE [App::DocumentObjectGroupPython] H_element107  label="H_element : 057"  # scripted group (container) (typed FeaturePython)
  n = 4
  ref = H_element
FEATURE [App::DocumentObjectGroupPython] N_element046  label="N_element : 019"  # scripted group (container) (typed FeaturePython)
  n = 2
  ref = N_element
FEATURE [App::DocumentObjectGroupPython] O_element101  label="O_element : 055"  # scripted group (container) (typed FeaturePython)
  n = 1
  ref = O_element
FEATURE [App::DocumentObjectGroupPython] G4_UREA  # scripted group (container) (typed FeaturePython)
  Dunit = g/cm3
  Dvalue = 1.323
  Group = -> [C_element119,H_element107,N_element046,O_element101]
  conduct = 2
  density = 1
  expand = 3
  formula = G4_UREA
  name = G4_UREA
  specific = 4
FEATURE [App::DocumentObjectGroupPython] C_element120  label="C_element : 067"  # scripted group (container) (typed FeaturePython)
  n = 5
  ref = C_element
FEATURE [App::DocumentObjectGroupPython] H_element108  label="H_element : 058"  # scripted group (container) (typed FeaturePython)
  n = 11
  ref = H_element
FEATURE [App::DocumentObjectGroupPython] N_element047  label="N_element : 020"  # scripted group (container) (typed FeaturePython)
  n = 1
  ref = N_element
FEATURE [App::DocumentObjectGroupPython] O_element102  label="O_element : 056"  # scripted group (container) (typed FeaturePython)
  n = 2
  ref = O_element
FEATURE [App::DocumentObjectGroupPython] G4_VALINE  # scripted group (container) (typed FeaturePython)
  Dunit = g/cm3
  Dvalue = 1.23
  Group = -> [C_element120,H_element108,N_element047,O_element102]
  conduct = 2
  density = 1
  expand = 3
  formula = G4_VALINE
  name = G4_VALINE
  specific = 4
FEATURE [App::DocumentObjectGroupPython] H_element109  label="H_element : 0.009"  # scripted group (container) (typed FeaturePython)
  n = 0.009417
FEATURE [App::DocumentObjectGroupPython] C_element121  label="C_element : 0.281"  # scripted group (container) (typed FeaturePython)
  n = 0.280555
FEATURE [App::DocumentObjectGroupPython] F_element018  label="F_element : 0.710"  # scripted group (container) (typed FeaturePython)
  n = 0.710028
FEATURE [App::DocumentObjectGroupPython] G4_VITON  # scripted group (container) (typed FeaturePython)
  Dunit = g/cm3
  Dvalue = 1.8
  Group = -> [H_element109,C_element121,F_element018]
  conduct = 2
  density = 1
  expand = 3
  formula = G4_VITON
  name = G4_VITON
  specific = 4
FEATURE [App::DocumentObjectGroupPython] H_element110  label="H_element : 059"  # scripted group (container) (typed FeaturePython)
  n = 2
  ref = H_element
FEATURE [App::DocumentObjectGroupPython] O_element103  label="O_element : 057"  # scripted group (container) (typed FeaturePython)
  n = 1
  ref = O_element
FEATURE [App::DocumentObjectGroupPython] G4_WATER  # scripted group (container) (typed FeaturePython)
  Dunit = g/cm3
  Dvalue = 1
  Group = -> [H_element110,O_element103]
  conduct = 2
  density = 1
  expand = 3
  formula = G4_WATER
  name = G4_WATER
  specific = 4
FEATURE [App::DocumentObjectGroupPython] H_element111  label="H_element : 060"  # scripted group (container) (typed FeaturePython)
  n = 2
  ref = H_element
FEATURE [App::DocumentObjectGroupPython] O_element104  label="O_element : 058"  # scripted group (container) (typed FeaturePython)
  n = 1
  ref = O_element
FEATURE [App::DocumentObjectGroupPython] G4_WATER_VAPOR  # scripted group (container) (typed FeaturePython)
  Dunit = g/cm3
  Dvalue = 0.000756182
  Group = -> [H_element111,O_element104]
  conduct = 2
  density = 1
  expand = 3
  formula = G4_WATER_VAPOR
  name = G4_WATER_VAPOR
  specific = 4
FEATURE [App::DocumentObjectGroupPython] C_element122  label="C_element : 068"  # scripted group (container) (typed FeaturePython)
  n = 8
  ref = C_element
FEATURE [App::DocumentObjectGroupPython] H_element112  label="H_element : 061"  # scripted group (container) (typed FeaturePython)
  n = 10
  ref = H_element
FEATURE [App::DocumentObjectGroupPython] G4_XYLENE  # scripted group (container) (typed FeaturePython)
  Dunit = g/cm3
  Dvalue = 0.87
  Group = -> [C_element122,H_element112]
  conduct = 2
  density = 1
  expand = 3
  formula = G4_XYLENE
  name = G4_XYLENE
  specific = 4
FEATURE [App::DocumentObjectGroupPython] C_element123  label="C_element : 069"  # scripted group (container) (typed FeaturePython)
  n = 1
  ref = C_element
FEATURE [App::DocumentObjectGroupPython] G4_GRAPHITE  # scripted group (container) (typed FeaturePython)
  Dunit = g/cm3
  Dvalue = 2.21
  Group = -> [C_element123]
  conduct = 2
  density = 1
  expand = 3
  formula = G4_GRAPHITE
  name = G4_GRAPHITE
  specific = 4
FEATURE [App::DocumentObjectGroupPython] NIST  # scripted group (container) (typed FeaturePython)
  Group = -> [G4_A_150_TISSUE,G4_ACETONE,G4_ACETYLENE,G4_ADENINE,G4_ADIPOSE_TISSUE_ICRP,G4_AIR,G4_ALANINE,G4_ALUMINUM_OXIDE,G4_AMBER,G4_AMMONIA,G4_ANILINE,G4_ANTHRACENE,G4_B_100_BONE,G4_BAKELITE,G4_BARIUM_FLUORIDE,G4_BARIUM_SULFATE,G4_BENZENE,G4_BERYLLIUM_OXIDE,G4_BGO,G4_BLOOD_ICRP,G4_BONE_COMPACT_ICRU,G4_BONE_CORTICAL_ICRP,G4_BORON_CARBIDE,G4_BORON_OXIDE,G4_BRAIN_ICRP,G4_BUTANE,G4_N_BUTYL_ALCOHOL,G4_C_552,+152 more]
FEATURE [App::DocumentObjectGroupPython] H_element113  label="H_element : 062"  # scripted group (container) (typed FeaturePython)
  n = 1
  ref = H_element
FEATURE [App::DocumentObjectGroupPython] G4_H  # scripted group (container) (typed FeaturePython)
  Dunit = g/cm3
  Dvalue = 8.3748e-05
  Group = -> [H_element113]
  conduct = 2
  density = 1
  expand = 3
  formula = H
  name = G4_H
  specific = 4
FEATURE [App::DocumentObjectGroupPython] He_element001  label="He_element : 1"  # scripted group (container) (typed FeaturePython)
  n = 1
  ref = He_element
FEATURE [App::DocumentObjectGroupPython] G4_He  # scripted group (container) (typed FeaturePython)
  Dunit = g/cm3
  Dvalue = 0.000166322
  Group = -> [He_element001]
  conduct = 2
  density = 1
  expand = 3
  formula = He
  name = G4_He
  specific = 4
FEATURE [App::DocumentObjectGroupPython] Li_element008  label="Li_element : 008"  # scripted group (container) (typed FeaturePython)
  n = 1
  ref = Li_element
FEATURE [App::DocumentObjectGroupPython] G4_Li  # scripted group (container) (typed FeaturePython)
  Dunit = g/cm3
  Dvalue = 0.534
  Group = -> [Li_element008]
  conduct = 2
  density = 1
  expand = 3
  formula = Li
  name = G4_Li
  specific = 4
FEATURE [App::DocumentObjectGroupPython] Be_element002  label="Be_element : 002"  # scripted group (container) (typed FeaturePython)
  n = 1
  ref = Be_element
FEATURE [App::DocumentObjectGroupPython] G4_Be  # scripted group (container) (typed FeaturePython)
  Dunit = g/cm3
  Dvalue = 1.848
  Group = -> [Be_element002]
  conduct = 2
  density = 1
  expand = 3
  formula = Be
  name = G4_Be
  specific = 4
FEATURE [App::DocumentObjectGroupPython] B_element007  label="B_element : 007"  # scripted group (container) (typed FeaturePython)
  n = 1
  ref = B_element
FEATURE [App::DocumentObjectGroupPython] G4_B  # scripted group (container) (typed FeaturePython)
  Dunit = g/cm3
  Dvalue = 2.37
  Group = -> [B_element007]
  conduct = 2
  density = 1
  expand = 3
  formula = B
  name = G4_B
  specific = 4
FEATURE [App::DocumentObjectGroupPython] C_element124  label="C_element : 070"  # scripted group (container) (typed FeaturePython)
  n = 1
  ref = C_element
FEATURE [App::DocumentObjectGroupPython] G4_C  # scripted group (container) (typed FeaturePython)
  Dunit = g/cm3
  Dvalue = 2
  Group = -> [C_element124]
  conduct = 2
  density = 1
  expand = 3
  formula = C
  name = G4_C
  specific = 4
FEATURE [App::DocumentObjectGroupPython] N_element048  label="N_element : 021"  # scripted group (container) (typed FeaturePython)
  n = 1
  ref = N_element
FEATURE [App::DocumentObjectGroupPython] G4_N  # scripted group (container) (typed FeaturePython)
  Dunit = g/cm3
  Dvalue = 0.0011652
  Group = -> [N_element048]
  conduct = 2
  density = 1
  expand = 3
  formula = N
  name = G4_N
  specific = 4
FEATURE [App::DocumentObjectGroupPython] O_element105  label="O_element : 059"  # scripted group (container) (typed FeaturePython)
  n = 1
  ref = O_element
FEATURE [App::DocumentObjectGroupPython] G4_O  # scripted group (container) (typed FeaturePython)
  Dunit = g/cm3
  Dvalue = 0.00133151
  Group = -> [O_element105]
  conduct = 2
  density = 1
  expand = 3
  formula = O
  name = G4_O
  specific = 4
FEATURE [App::DocumentObjectGroupPython] F_element019  label="F_element : 008"  # scripted group (container) (typed FeaturePython)
  n = 1
  ref = F_element
FEATURE [App::DocumentObjectGroupPython] G4_F  # scripted group (container) (typed FeaturePython)
  Dunit = g/cm3
  Dvalue = 0.00158029
  Group = -> [F_element019]
  conduct = 2
  density = 1
  expand = 3
  formula = F
  name = G4_F
  specific = 4
FEATURE [App::DocumentObjectGroupPython] Ne_element001  label="Ne_element : 1"  # scripted group (container) (typed FeaturePython)
  n = 1
  ref = Ne_element
FEATURE [App::DocumentObjectGroupPython] G4_Ne  # scripted group (container) (typed FeaturePython)
  Dunit = g/cm3
  Dvalue = 0.000838505
  Group = -> [Ne_element001]
  conduct = 2
  density = 1
  expand = 3
  formula = Ne
  name = G4_Ne
  specific = 4
FEATURE [App::DocumentObjectGroupPython] Na_element020  label="Na_element : 005"  # scripted group (container) (typed FeaturePython)
  n = 1
  ref = Na_element
FEATURE [App::DocumentObjectGroupPython] G4_Na  # scripted group (container) (typed FeaturePython)
  Dunit = g/cm3
  Dvalue = 0.971
  Group = -> [Na_element020]
  conduct = 2
  density = 1
  expand = 3
  formula = Na
  name = G4_Na
  specific = 4
FEATURE [App::DocumentObjectGroupPython] Mg_element011  label="Mg_element : 005"  # scripted group (container) (typed FeaturePython)
  n = 1
  ref = Mg_element
FEATURE [App::DocumentObjectGroupPython] G4_Mg  # scripted group (container) (typed FeaturePython)
  Dunit = g/cm3
  Dvalue = 1.74
  Group = -> [Mg_element011]
  conduct = 2
  density = 1
  expand = 3
  formula = Mg
  name = G4_Mg
  specific = 4
FEATURE [App::DocumentObjectGroupPython] Al_element004  label="Al_element : 1"  # scripted group (container) (typed FeaturePython)
  n = 1
  ref = Al_element
FEATURE [App::DocumentObjectGroupPython] G4_Al  # scripted group (container) (typed FeaturePython)
  Dunit = g/cm3
  Dvalue = 2.699
  Group = -> [Al_element004]
  conduct = 2
  density = 1
  expand = 3
  formula = Al
  name = G4_Al
  specific = 4
FEATURE [App::DocumentObjectGroupPython] Si_element007  label="Si_element : 002"  # scripted group (container) (typed FeaturePython)
  n = 1
  ref = Si_element
FEATURE [App::DocumentObjectGroupPython] G4_Si  # scripted group (container) (typed FeaturePython)
  Dunit = g/cm3
  Dvalue = 2.33
  Group = -> [Si_element007]
  conduct = 2
  density = 1
  expand = 3
  formula = Si
  name = G4_Si
  specific = 4
FEATURE [App::DocumentObjectGroupPython] P_element013  label="P_element : 002"  # scripted group (container) (typed FeaturePython)
  n = 1
  ref = P_element
FEATURE [App::DocumentObjectGroupPython] G4_P  # scripted group (container) (typed FeaturePython)
  Dunit = g/cm3
  Dvalue = 2.2
  Group = -> [P_element013]
  conduct = 2
  density = 1
  expand = 3
  formula = P
  name = G4_P
  specific = 4
FEATURE [App::DocumentObjectGroupPython] S_element023  label="S_element : 007"  # scripted group (container) (typed FeaturePython)
  n = 1
  ref = S_element
FEATURE [App::DocumentObjectGroupPython] G4_S  # scripted group (container) (typed FeaturePython)
  Dunit = g/cm3
  Dvalue = 2
  Group = -> [S_element023]
  conduct = 2
  density = 1
  expand = 3
  formula = S
  name = G4_S
  specific = 4
FEATURE [App::DocumentObjectGroupPython] Cl_element029  label="Cl_element : 015"  # scripted group (container) (typed FeaturePython)
  n = 1
  ref = Cl_element
FEATURE [App::DocumentObjectGroupPython] G4_Cl  # scripted group (container) (typed FeaturePython)
  Dunit = g/cm3
  Dvalue = 0.00299473
  Group = -> [Cl_element029]
  conduct = 2
  density = 1
  expand = 3
  formula = Cl
  name = G4_Cl
  specific = 4
FEATURE [App::DocumentObjectGroupPython] Ar_element002  label="Ar_element : 1"  # scripted group (container) (typed FeaturePython)
  n = 1
  ref = Ar_element
FEATURE [App::DocumentObjectGroupPython] G4_Ar  # scripted group (container) (typed FeaturePython)
  Dunit = g/cm3
  Dvalue = 0.00166201
  Group = -> [Ar_element002]
  conduct = 2
  density = 1
  expand = 3
  formula = Ar
  name = G4_Ar
  specific = 4
FEATURE [App::DocumentObjectGroupPython] K_element013  label="K_element : 003"  # scripted group (container) (typed FeaturePython)
  n = 1
  ref = K_element
FEATURE [App::DocumentObjectGroupPython] G4_K  # scripted group (container) (typed FeaturePython)
  Dunit = g/cm3
  Dvalue = 0.862
  Group = -> [K_element013]
  conduct = 2
  density = 1
  expand = 3
  formula = K
  name = G4_K
  specific = 4
FEATURE [App::DocumentObjectGroupPython] Ca_element014  label="Ca_element : 007"  # scripted group (container) (typed FeaturePython)
  n = 1
  ref = Ca_element
FEATURE [App::DocumentObjectGroupPython] G4_Ca  # scripted group (container) (typed FeaturePython)
  Dunit = g/cm3
  Dvalue = 1.55
  Group = -> [Ca_element014]
  conduct = 2
  density = 1
  expand = 3
  formula = Ca
  name = G4_Ca
  specific = 4
FEATURE [App::DocumentObjectGroupPython] Sc_element001  label="Sc_element : 1"  # scripted group (container) (typed FeaturePython)
  n = 1
  ref = Sc_element
FEATURE [App::DocumentObjectGroupPython] G4_Sc  # scripted group (container) (typed FeaturePython)
  Dunit = g/cm3
  Dvalue = 2.989
  Group = -> [Sc_element001]
  conduct = 2
  density = 1
  expand = 3
  formula = Sc
  name = G4_Sc
  specific = 4
FEATURE [App::DocumentObjectGroupPython] Ti_element004  label="Ti_element : 002"  # scripted group (container) (typed FeaturePython)
  n = 1
  ref = Ti_element
FEATURE [App::DocumentObjectGroupPython] G4_Ti  # scripted group (container) (typed FeaturePython)
  Dunit = g/cm3
  Dvalue = 4.54
  Group = -> [Ti_element004]
  conduct = 2
  density = 1
  expand = 3
  formula = Ti
  name = G4_Ti
  specific = 4
FEATURE [App::DocumentObjectGroupPython] V_element001  label="V_element : 1"  # scripted group (container) (typed FeaturePython)
  n = 1
  ref = V_element
FEATURE [App::DocumentObjectGroupPython] G4_V  # scripted group (container) (typed FeaturePython)
  Dunit = g/cm3
  Dvalue = 6.11
  Group = -> [V_element001]
  conduct = 2
  density = 1
  expand = 3
  formula = V
  name = G4_V
  specific = 4
FEATURE [App::DocumentObjectGroupPython] Cr_element001  label="Cr_element : 1"  # scripted group (container) (typed FeaturePython)
  n = 1
  ref = Cr_element
FEATURE [App::DocumentObjectGroupPython] G4_Cr  # scripted group (container) (typed FeaturePython)
  Dunit = g/cm3
  Dvalue = 7.18
  Group = -> [Cr_element001]
  conduct = 2
  density = 1
  expand = 3
  formula = Cr
  name = G4_Cr
  specific = 4
FEATURE [App::DocumentObjectGroupPython] Mn_element001  label="Mn_element : 1"  # scripted group (container) (typed FeaturePython)
  n = 1
  ref = Mn_element
FEATURE [App::DocumentObjectGroupPython] G4_Mn  # scripted group (container) (typed FeaturePython)
  Dunit = g/cm3
  Dvalue = 7.44
  Group = -> [Mn_element001]
  conduct = 2
  density = 1
  expand = 3
  formula = Mn
  name = G4_Mn
  specific = 4
FEATURE [App::DocumentObjectGroupPython] Fe_element007  label="Fe_element : 004"  # scripted group (container) (typed FeaturePython)
  n = 1
  ref = Fe_element
FEATURE [App::DocumentObjectGroupPython] G4_Fe  # scripted group (container) (typed FeaturePython)
  Dunit = g/cm3
  Dvalue = 7.874
  Group = -> [Fe_element007]
  conduct = 2
  density = 1
  expand = 3
  formula = Fe
  name = G4_Fe
  specific = 4
FEATURE [App::DocumentObjectGroupPython] Co_element001  label="Co_element : 1"  # scripted group (container) (typed FeaturePython)
  n = 1
  ref = Co_element
FEATURE [App::DocumentObjectGroupPython] G4_Co  # scripted group (container) (typed FeaturePython)
  Dunit = g/cm3
  Dvalue = 8.9
  Group = -> [Co_element001]
  conduct = 2
  density = 1
  expand = 3
  formula = Co
  name = G4_Co
  specific = 4
FEATURE [App::DocumentObjectGroupPython] Ni_element001  label="Ni_element : 1"  # scripted group (container) (typed FeaturePython)
  n = 1
  ref = Ni_element
FEATURE [App::DocumentObjectGroupPython] G4_Ni  # scripted group (container) (typed FeaturePython)
  Dunit = g/cm3
  Dvalue = 8.902
  Group = -> [Ni_element001]
  conduct = 2
  density = 1
  expand = 3
  formula = Ni
  name = G4_Ni
  specific = 4
FEATURE [App::DocumentObjectGroupPython] Cu_element001  label="Cu_element : 1"  # scripted group (container) (typed FeaturePython)
  n = 1
  ref = Cu_element
FEATURE [App::DocumentObjectGroupPython] G4_Cu  # scripted group (container) (typed FeaturePython)
  Dunit = g/cm3
  Dvalue = 8.96
  Group = -> [Cu_element001]
  conduct = 2
  density = 1
  expand = 3
  formula = Cu
  name = G4_Cu
  specific = 4
FEATURE [App::DocumentObjectGroupPython] Zn_element001  label="Zn_element : 1"  # scripted group (container) (typed FeaturePython)
  n = 1
  ref = Zn_element
FEATURE [App::DocumentObjectGroupPython] G4_Zn  # scripted group (container) (typed FeaturePython)
  Dunit = g/cm3
  Dvalue = 7.133
  Group = -> [Zn_element001]
  conduct = 2
  density = 1
  expand = 3
  formula = Zn
  name = G4_Zn
  specific = 4
FEATURE [App::DocumentObjectGroupPython] Ga_element002  label="Ga_element : 002"  # scripted group (container) (typed FeaturePython)
  n = 1
  ref = Ga_element
FEATURE [App::DocumentObjectGroupPython] G4_Ga  # scripted group (container) (typed FeaturePython)
  Dunit = g/cm3
  Dvalue = 5.904
  Group = -> [Ga_element002]
  conduct = 2
  density = 1
  expand = 3
  formula = Ga
  name = G4_Ga
  specific = 4
FEATURE [App::DocumentObjectGroupPython] Ge_element002  label="Ge_element : 1"  # scripted group (container) (typed FeaturePython)
  n = 1
  ref = Ge_element
FEATURE [App::DocumentObjectGroupPython] G4_Ge  # scripted group (container) (typed FeaturePython)
  Dunit = g/cm3
  Dvalue = 5.323
  Group = -> [Ge_element002]
  conduct = 2
  density = 1
  expand = 3
  formula = Ge
  name = G4_Ge
  specific = 4
FEATURE [App::DocumentObjectGroupPython] As_element003  label="As_element : 002"  # scripted group (container) (typed FeaturePython)
  n = 1
  ref = As_element
FEATURE [App::DocumentObjectGroupPython] G4_As  # scripted group (container) (typed FeaturePython)
  Dunit = g/cm3
  Dvalue = 5.73
  Group = -> [As_element003]
  conduct = 2
  density = 1
  expand = 3
  formula = As
  name = G4_As
  specific = 4
FEATURE [App::DocumentObjectGroupPython] Se_element001  label="Se_element : 1"  # scripted group (container) (typed FeaturePython)
  n = 1
  ref = Se_element
FEATURE [App::DocumentObjectGroupPython] G4_Se  # scripted group (container) (typed FeaturePython)
  Dunit = g/cm3
  Dvalue = 4.5
  Group = -> [Se_element001]
  conduct = 2
  density = 1
  expand = 3
  formula = Se
  name = G4_Se
  specific = 4
FEATURE [App::DocumentObjectGroupPython] Br_element007  label="Br_element : 004"  # scripted group (container) (typed FeaturePython)
  n = 1
  ref = Br_element
FEATURE [App::DocumentObjectGroupPython] G4_Br  # scripted group (container) (typed FeaturePython)
  Dunit = g/cm3
  Dvalue = 0.0070721
  Group = -> [Br_element007]
  conduct = 2
  density = 1
  expand = 3
  formula = Br
  name = G4_Br
  specific = 4
FEATURE [App::DocumentObjectGroupPython] Kr_element001  label="Kr_element : 1"  # scripted group (container) (typed FeaturePython)
  n = 1
  ref = Kr_element
FEATURE [App::DocumentObjectGroupPython] G4_Kr  # scripted group (container) (typed FeaturePython)
  Dunit = g/cm3
  Dvalue = 0.00347832
  Group = -> [Kr_element001]
  conduct = 2
  density = 1
  expand = 3
  formula = Kr
  name = G4_Kr
  specific = 4
FEATURE [App::DocumentObjectGroupPython] Rb_element001  label="Rb_element : 1"  # scripted group (container) (typed FeaturePython)
  n = 1
  ref = Rb_element
FEATURE [App::DocumentObjectGroupPython] G4_Rb  # scripted group (container) (typed FeaturePython)
  Dunit = g/cm3
  Dvalue = 1.532
  Group = -> [Rb_element001]
  conduct = 2
  density = 1
  expand = 3
  formula = Rb
  name = G4_Rb
  specific = 4
FEATURE [App::DocumentObjectGroupPython] Sr_element001  label="Sr_element : 1"  # scripted group (container) (typed FeaturePython)
  n = 1
  ref = Sr_element
FEATURE [App::DocumentObjectGroupPython] G4_Sr  # scripted group (container) (typed FeaturePython)
  Dunit = g/cm3
  Dvalue = 2.54
  Group = -> [Sr_element001]
  conduct = 2
  density = 1
  expand = 3
  formula = Sr
  name = G4_Sr
  specific = 4
FEATURE [App::DocumentObjectGroupPython] Y_element001  label="Y_element : 1"  # scripted group (container) (typed FeaturePython)
  n = 1
  ref = Y_element
FEATURE [App::DocumentObjectGroupPython] G4_Y  # scripted group (container) (typed FeaturePython)
  Dunit = g/cm3
  Dvalue = 4.469
  Group = -> [Y_element001]
  conduct = 2
  density = 1
  expand = 3
  formula = Y
  name = G4_Y
  specific = 4
FEATURE [App::DocumentObjectGroupPython] Zr_element001  label="Zr_element : 1"  # scripted group (container) (typed FeaturePython)
  n = 1
  ref = Zr_element
FEATURE [App::DocumentObjectGroupPython] G4_Zr  # scripted group (container) (typed FeaturePython)
  Dunit = g/cm3
  Dvalue = 6.506
  Group = -> [Zr_element001]
  conduct = 2
  density = 1
  expand = 3
  formula = Zr
  name = G4_Zr
  specific = 4
FEATURE [App::DocumentObjectGroupPython] Nb_element001  label="Nb_element : 1"  # scripted group (container) (typed FeaturePython)
  n = 1
  ref = Nb_element
FEATURE [App::DocumentObjectGroupPython] G4_Nb  # scripted group (container) (typed FeaturePython)
  Dunit = g/cm3
  Dvalue = 8.57
  Group = -> [Nb_element001]
  conduct = 2
  density = 1
  expand = 3
  formula = Nb
  name = G4_Nb
  specific = 4
FEATURE [App::DocumentObjectGroupPython] Mo_element001  label="Mo_element : 1"  # scripted group (container) (typed FeaturePython)
  n = 1
  ref = Mo_element
FEATURE [App::DocumentObjectGroupPython] G4_Mo  # scripted group (container) (typed FeaturePython)
  Dunit = g/cm3
  Dvalue = 10.22
  Group = -> [Mo_element001]
  conduct = 2
  density = 1
  expand = 3
  formula = Mo
  name = G4_Mo
  specific = 4
FEATURE [App::DocumentObjectGroupPython] Tc_element001  label="Tc_element : 1"  # scripted group (container) (typed FeaturePython)
  n = 1
  ref = Tc_element
FEATURE [App::DocumentObjectGroupPython] G4_Tc  # scripted group (container) (typed FeaturePython)
  Dunit = g/cm3
  Dvalue = 11.5
  Group = -> [Tc_element001]
  conduct = 2
  density = 1
  expand = 3
  formula = Tc
  name = G4_Tc
  specific = 4
FEATURE [App::DocumentObjectGroupPython] Ru_element001  label="Ru_element : 1"  # scripted group (container) (typed FeaturePython)
  n = 1
  ref = Ru_element
FEATURE [App::DocumentObjectGroupPython] G4_Ru  # scripted group (container) (typed FeaturePython)
  Dunit = g/cm3
  Dvalue = 12.41
  Group = -> [Ru_element001]
  conduct = 2
  density = 1
  expand = 3
  formula = Ru
  name = G4_Ru
  specific = 4
FEATURE [App::DocumentObjectGroupPython] Rh_element001  label="Rh_element : 1"  # scripted group (container) (typed FeaturePython)
  n = 1
  ref = Rh_element
FEATURE [App::DocumentObjectGroupPython] G4_Rh  # scripted group (container) (typed FeaturePython)
  Dunit = g/cm3
  Dvalue = 12.41
  Group = -> [Rh_element001]
  conduct = 2
  density = 1
  expand = 3
  formula = Rh
  name = G4_Rh
  specific = 4
FEATURE [App::DocumentObjectGroupPython] Pd_element001  label="Pd_element : 1"  # scripted group (container) (typed FeaturePython)
  n = 1
  ref = Pd_element
FEATURE [App::DocumentObjectGroupPython] G4_Pd  # scripted group (container) (typed FeaturePython)
  Dunit = g/cm3
  Dvalue = 12.02
  Group = -> [Pd_element001]
  conduct = 2
  density = 1
  expand = 3
  formula = Pd
  name = G4_Pd
  specific = 4
FEATURE [App::DocumentObjectGroupPython] Ag_element006  label="Ag_element : 004"  # scripted group (container) (typed FeaturePython)
  n = 1
  ref = Ag_element
FEATURE [App::DocumentObjectGroupPython] G4_Ag  # scripted group (container) (typed FeaturePython)
  Dunit = g/cm3
  Dvalue = 10.5
  Group = -> [Ag_element006]
  conduct = 2
  density = 1
  expand = 3
  formula = Ag
  name = G4_Ag
  specific = 4
FEATURE [App::DocumentObjectGroupPython] Cd_element003  label="Cd_element : 003"  # scripted group (container) (typed FeaturePython)
  n = 1
  ref = Cd_element
FEATURE [App::DocumentObjectGroupPython] G4_Cd  # scripted group (container) (typed FeaturePython)
  Dunit = g/cm3
  Dvalue = 8.65
  Group = -> [Cd_element003]
  conduct = 2
  density = 1
  expand = 3
  formula = Cd
  name = G4_Cd
  specific = 4
FEATURE [App::DocumentObjectGroupPython] In_element001  label="In_element : 1"  # scripted group (container) (typed FeaturePython)
  n = 1
  ref = In_element
FEATURE [App::DocumentObjectGroupPython] G4_In  # scripted group (container) (typed FeaturePython)
  Dunit = g/cm3
  Dvalue = 7.31
  Group = -> [In_element001]
  conduct = 2
  density = 1
  expand = 3
  formula = In
  name = G4_In
  specific = 4
FEATURE [App::DocumentObjectGroupPython] Sn_element001  label="Sn_element : 1"  # scripted group (container) (typed FeaturePython)
  n = 1
  ref = Sn_element
FEATURE [App::DocumentObjectGroupPython] G4_Sn  # scripted group (container) (typed FeaturePython)
  Dunit = g/cm3
  Dvalue = 7.31
  Group = -> [Sn_element001]
  conduct = 2
  density = 1
  expand = 3
  formula = Sn
  name = G4_Sn
  specific = 4
FEATURE [App::DocumentObjectGroupPython] Sb_element001  label="Sb_element : 1"  # scripted group (container) (typed FeaturePython)
  n = 1
  ref = Sb_element
FEATURE [App::DocumentObjectGroupPython] G4_Sb  # scripted group (container) (typed FeaturePython)
  Dunit = g/cm3
  Dvalue = 6.691
  Group = -> [Sb_element001]
  conduct = 2
  density = 1
  expand = 3
  formula = Sb
  name = G4_Sb
  specific = 4
FEATURE [App::DocumentObjectGroupPython] Te_element002  label="Te_element : 002"  # scripted group (container) (typed FeaturePython)
  n = 1
  ref = Te_element
FEATURE [App::DocumentObjectGroupPython] G4_Te  # scripted group (container) (typed FeaturePython)
  Dunit = g/cm3
  Dvalue = 6.24
  Group = -> [Te_element002]
  conduct = 2
  density = 1
  expand = 3
  formula = Te
  name = G4_Te
  specific = 4
FEATURE [App::DocumentObjectGroupPython] I_element010  label="I_element : 006"  # scripted group (container) (typed FeaturePython)
  n = 1
  ref = I_element
FEATURE [App::DocumentObjectGroupPython] G4_I  # scripted group (container) (typed FeaturePython)
  Dunit = g/cm3
  Dvalue = 4.93
  Group = -> [I_element010]
  conduct = 2
  density = 1
  expand = 3
  formula = I
  name = G4_I
  specific = 4
FEATURE [App::DocumentObjectGroupPython] Xe_element001  label="Xe_element : 1"  # scripted group (container) (typed FeaturePython)
  n = 1
  ref = Xe_element
FEATURE [App::DocumentObjectGroupPython] G4_Xe  # scripted group (container) (typed FeaturePython)
  Dunit = g/cm3
  Dvalue = 0.00548536
  Group = -> [Xe_element001]
  conduct = 2
  density = 1
  expand = 3
  formula = Xe
  name = G4_Xe
  specific = 4
FEATURE [App::DocumentObjectGroupPython] Cs_element003  label="Cs_element : 003"  # scripted group (container) (typed FeaturePython)
  n = 1
  ref = Cs_element
FEATURE [App::DocumentObjectGroupPython] G4_Cs  # scripted group (container) (typed FeaturePython)
  Dunit = g/cm3
  Dvalue = 1.873
  Group = -> [Cs_element003]
  conduct = 2
  density = 1
  expand = 3
  formula = Cs
  name = G4_Cs
  specific = 4
FEATURE [App::DocumentObjectGroupPython] Ba_element003  label="Ba_element : 003"  # scripted group (container) (typed FeaturePython)
  n = 1
  ref = Ba_element
FEATURE [App::DocumentObjectGroupPython] G4_Ba  # scripted group (container) (typed FeaturePython)
  Dunit = g/cm3
  Dvalue = 3.5
  Group = -> [Ba_element003]
  conduct = 2
  density = 1
  expand = 3
  formula = Ba
  name = G4_Ba
  specific = 4
FEATURE [App::DocumentObjectGroupPython] La_element003  label="La_element : 003"  # scripted group (container) (typed FeaturePython)
  n = 1
  ref = La_element
FEATURE [App::DocumentObjectGroupPython] G4_La  # scripted group (container) (typed FeaturePython)
  Dunit = g/cm3
  Dvalue = 6.154
  Group = -> [La_element003]
  conduct = 2
  density = 1
  expand = 3
  formula = La
  name = G4_La
  specific = 4
FEATURE [App::DocumentObjectGroupPython] Ce_element002  label="Ce_element : 1"  # scripted group (container) (typed FeaturePython)
  n = 1
  ref = Ce_element
FEATURE [App::DocumentObjectGroupPython] G4_Ce  # scripted group (container) (typed FeaturePython)
  Dunit = g/cm3
  Dvalue = 6.657
  Group = -> [Ce_element002]
  conduct = 2
  density = 1
  expand = 3
  formula = Ce
  name = G4_Ce
  specific = 4
FEATURE [App::DocumentObjectGroupPython] Pr_element001  label="Pr_element : 1"  # scripted group (container) (typed FeaturePython)
  n = 1
  ref = Pr_element
FEATURE [App::DocumentObjectGroupPython] G4_Pr  # scripted group (container) (typed FeaturePython)
  Dunit = g/cm3
  Dvalue = 6.71
  Group = -> [Pr_element001]
  conduct = 2
  density = 1
  expand = 3
  formula = Pr
  name = G4_Pr
  specific = 4
FEATURE [App::DocumentObjectGroupPython] Nd_element001  label="Nd_element : 1"  # scripted group (container) (typed FeaturePython)
  n = 1
  ref = Nd_element
FEATURE [App::DocumentObjectGroupPython] G4_Nd  # scripted group (container) (typed FeaturePython)
  Dunit = g/cm3
  Dvalue = 6.9
  Group = -> [Nd_element001]
  conduct = 2
  density = 1
  expand = 3
  formula = Nd
  name = G4_Nd
  specific = 4
FEATURE [App::DocumentObjectGroupPython] Pm_element001  label="Pm_element : 1"  # scripted group (container) (typed FeaturePython)
  n = 1
  ref = Pm_element
FEATURE [App::DocumentObjectGroupPython] G4_Pm  # scripted group (container) (typed FeaturePython)
  Dunit = g/cm3
  Dvalue = 7.22
  Group = -> [Pm_element001]
  conduct = 2
  density = 1
  expand = 3
  formula = Pm
  name = G4_Pm
  specific = 4
FEATURE [App::DocumentObjectGroupPython] Sm_element001  label="Sm_element : 1"  # scripted group (container) (typed FeaturePython)
  n = 1
  ref = Sm_element
FEATURE [App::DocumentObjectGroupPython] G4_Sm  # scripted group (container) (typed FeaturePython)
  Dunit = g/cm3
  Dvalue = 7.46
  Group = -> [Sm_element001]
  conduct = 2
  density = 1
  expand = 3
  formula = Sm
  name = G4_Sm
  specific = 4
FEATURE [App::DocumentObjectGroupPython] Eu_element001  label="Eu_element : 1"  # scripted group (container) (typed FeaturePython)
  n = 1
  ref = Eu_element
FEATURE [App::DocumentObjectGroupPython] G4_Eu  # scripted group (container) (typed FeaturePython)
  Dunit = g/cm3
  Dvalue = 5.243
  Group = -> [Eu_element001]
  conduct = 2
  density = 1
  expand = 3
  formula = Eu
  name = G4_Eu
  specific = 4
FEATURE [App::DocumentObjectGroupPython] Gd_element002  label="Gd_element : 1"  # scripted group (container) (typed FeaturePython)
  n = 1
  ref = Gd_element
FEATURE [App::DocumentObjectGroupPython] G4_Gd  # scripted group (container) (typed FeaturePython)
  Dunit = g/cm3
  Dvalue = 7.9004
  Group = -> [Gd_element002]
  conduct = 2
  density = 1
  expand = 3
  formula = Gd
  name = G4_Gd
  specific = 4
FEATURE [App::DocumentObjectGroupPython] Tb_element001  label="Tb_element : 1"  # scripted group (container) (typed FeaturePython)
  n = 1
  ref = Tb_element
FEATURE [App::DocumentObjectGroupPython] G4_Tb  # scripted group (container) (typed FeaturePython)
  Dunit = g/cm3
  Dvalue = 8.229
  Group = -> [Tb_element001]
  conduct = 2
  density = 1
  expand = 3
  formula = Tb
  name = G4_Tb
  specific = 4
FEATURE [App::DocumentObjectGroupPython] Dy_element001  label="Dy_element : 1"  # scripted group (container) (typed FeaturePython)
  n = 1
  ref = Dy_element
FEATURE [App::DocumentObjectGroupPython] G4_Dy  # scripted group (container) (typed FeaturePython)
  Dunit = g/cm3
  Dvalue = 8.55
  Group = -> [Dy_element001]
  conduct = 2
  density = 1
  expand = 3
  formula = Dy
  name = G4_Dy
  specific = 4
FEATURE [App::DocumentObjectGroupPython] Ho_element001  label="Ho_element : 1"  # scripted group (container) (typed FeaturePython)
  n = 1
  ref = Ho_element
FEATURE [App::DocumentObjectGroupPython] G4_Ho  # scripted group (container) (typed FeaturePython)
  Dunit = g/cm3
  Dvalue = 8.795
  Group = -> [Ho_element001]
  conduct = 2
  density = 1
  expand = 3
  formula = Ho
  name = G4_Ho
  specific = 4
FEATURE [App::DocumentObjectGroupPython] Er_element001  label="Er_element : 1"  # scripted group (container) (typed FeaturePython)
  n = 1
  ref = Er_element
FEATURE [App::DocumentObjectGroupPython] G4_Er  # scripted group (container) (typed FeaturePython)
  Dunit = g/cm3
  Dvalue = 9.066
  Group = -> [Er_element001]
  conduct = 2
  density = 1
  expand = 3
  formula = Er
  name = G4_Er
  specific = 4
FEATURE [App::DocumentObjectGroupPython] Tm_element001  label="Tm_element : 1"  # scripted group (container) (typed FeaturePython)
  n = 1
  ref = Tm_element
FEATURE [App::DocumentObjectGroupPython] G4_Tm  # scripted group (container) (typed FeaturePython)
  Dunit = g/cm3
  Dvalue = 9.321
  Group = -> [Tm_element001]
  conduct = 2
  density = 1
  expand = 3
  formula = Tm
  name = G4_Tm
  specific = 4
FEATURE [App::DocumentObjectGroupPython] Yb_element001  label="Yb_element : 1"  # scripted group (container) (typed FeaturePython)
  n = 1
  ref = Yb_element
FEATURE [App::DocumentObjectGroupPython] G4_Yb  # scripted group (container) (typed FeaturePython)
  Dunit = g/cm3
  Dvalue = 6.73
  Group = -> [Yb_element001]
  conduct = 2
  density = 1
  expand = 3
  formula = Yb
  name = G4_Yb
  specific = 4
FEATURE [App::DocumentObjectGroupPython] Lu_element001  label="Lu_element : 1"  # scripted group (container) (typed FeaturePython)
  n = 1
  ref = Lu_element
FEATURE [App::DocumentObjectGroupPython] G4_Lu  # scripted group (container) (typed FeaturePython)
  Dunit = g/cm3
  Dvalue = 9.84
  Group = -> [Lu_element001]
  conduct = 2
  density = 1
  expand = 3
  formula = Lu
  name = G4_Lu
  specific = 4
FEATURE [App::DocumentObjectGroupPython] Hf_element001  label="Hf_element : 1"  # scripted group (container) (typed FeaturePython)
  n = 1
  ref = Hf_element
FEATURE [App::DocumentObjectGroupPython] G4_Hf  # scripted group (container) (typed FeaturePython)
  Dunit = g/cm3
  Dvalue = 13.31
  Group = -> [Hf_element001]
  conduct = 2
  density = 1
  expand = 3
  formula = Hf
  name = G4_Hf
  specific = 4
FEATURE [App::DocumentObjectGroupPython] Ta_element001  label="Ta_element : 1"  # scripted group (container) (typed FeaturePython)
  n = 1
  ref = Ta_element
FEATURE [App::DocumentObjectGroupPython] G4_Ta  # scripted group (container) (typed FeaturePython)
  Dunit = g/cm3
  Dvalue = 16.654
  Group = -> [Ta_element001]
  conduct = 2
  density = 1
  expand = 3
  formula = Ta
  name = G4_Ta
  specific = 4
FEATURE [App::DocumentObjectGroupPython] W_element004  label="W_element : 004"  # scripted group (container) (typed FeaturePython)
  n = 1
  ref = W_element
FEATURE [App::DocumentObjectGroupPython] G4_W  # scripted group (container) (typed FeaturePython)
  Dunit = g/cm3
  Dvalue = 19.3
  Group = -> [W_element004]
  conduct = 2
  density = 1
  expand = 3
  formula = W
  name = G4_W
  specific = 4
FEATURE [App::DocumentObjectGroupPython] Re_element001  label="Re_element : 1"  # scripted group (container) (typed FeaturePython)
  n = 1
  ref = Re_element
FEATURE [App::DocumentObjectGroupPython] G4_Re  # scripted group (container) (typed FeaturePython)
  Dunit = g/cm3
  Dvalue = 21.02
  Group = -> [Re_element001]
  conduct = 2
  density = 1
  expand = 3
  formula = Re
  name = G4_Re
  specific = 4
FEATURE [App::DocumentObjectGroupPython] Os_element001  label="Os_element : 1"  # scripted group (container) (typed FeaturePython)
  n = 1
  ref = Os_element
FEATURE [App::DocumentObjectGroupPython] G4_Os  # scripted group (container) (typed FeaturePython)
  Dunit = g/cm3
  Dvalue = 22.57
  Group = -> [Os_element001]
  conduct = 2
  density = 1
  expand = 3
  formula = Os
  name = G4_Os
  specific = 4
FEATURE [App::DocumentObjectGroupPython] Ir_element001  label="Ir_element : 1"  # scripted group (container) (typed FeaturePython)
  n = 1
  ref = Ir_element
FEATURE [App::DocumentObjectGroupPython] G4_Ir  # scripted group (container) (typed FeaturePython)
  Dunit = g/cm3
  Dvalue = 22.42
  Group = -> [Ir_element001]
  conduct = 2
  density = 1
  expand = 3
  formula = Ir
  name = G4_Ir
  specific = 4
FEATURE [App::DocumentObjectGroupPython] Pt_element001  label="Pt_element : 1"  # scripted group (container) (typed FeaturePython)
  n = 1
  ref = Pt_element
FEATURE [App::DocumentObjectGroupPython] G4_Pt  # scripted group (container) (typed FeaturePython)
  Dunit = g/cm3
  Dvalue = 21.45
  Group = -> [Pt_element001]
  conduct = 2
  density = 1
  expand = 3
  formula = Pt
  name = G4_Pt
  specific = 4
FEATURE [App::DocumentObjectGroupPython] Au_element001  label="Au_element : 1"  # scripted group (container) (typed FeaturePython)
  n = 1
  ref = Au_element
FEATURE [App::DocumentObjectGroupPython] G4_Au  # scripted group (container) (typed FeaturePython)
  Dunit = g/cm3
  Dvalue = 19.32
  Group = -> [Au_element001]
  conduct = 2
  density = 1
  expand = 3
  formula = Au
  name = G4_Au
  specific = 4
FEATURE [App::DocumentObjectGroupPython] Hg_element002  label="Hg_element : 002"  # scripted group (container) (typed FeaturePython)
  n = 1
  ref = Hg_element
FEATURE [App::DocumentObjectGroupPython] G4_Hg  # scripted group (container) (typed FeaturePython)
  Dunit = g/cm3
  Dvalue = 13.546
  Group = -> [Hg_element002]
  conduct = 2
  density = 1
  expand = 3
  formula = Hg
  name = G4_Hg
  specific = 4
FEATURE [App::DocumentObjectGroupPython] Tl_element002  label="Tl_element : 002"  # scripted group (container) (typed FeaturePython)
  n = 1
  ref = Tl_element
FEATURE [App::DocumentObjectGroupPython] G4_Tl  # scripted group (container) (typed FeaturePython)
  Dunit = g/cm3
  Dvalue = 11.72
  Group = -> [Tl_element002]
  conduct = 2
  density = 1
  expand = 3
  formula = Tl
  name = G4_Tl
  specific = 4
FEATURE [App::DocumentObjectGroupPython] Pb_element003  label="Pb_element : 1"  # scripted group (container) (typed FeaturePython)
  n = 1
  ref = Pb_element
FEATURE [App::DocumentObjectGroupPython] G4_Pb  # scripted group (container) (typed FeaturePython)
  Dunit = g/cm3
  Dvalue = 11.35
  Group = -> [Pb_element003]
  conduct = 2
  density = 1
  expand = 3
  formula = Pb
  name = G4_Pb
  specific = 4
FEATURE [App::DocumentObjectGroupPython] Bi_element002  label="Bi_element : 1"  # scripted group (container) (typed FeaturePython)
  n = 1
  ref = Bi_element
FEATURE [App::DocumentObjectGroupPython] G4_Bi  # scripted group (container) (typed FeaturePython)
  Dunit = g/cm3
  Dvalue = 9.747
  Group = -> [Bi_element002]
  conduct = 2
  density = 1
  expand = 3
  formula = Bi
  name = G4_Bi
  specific = 4
FEATURE [App::DocumentObjectGroupPython] Po_element001  label="Po_element : 1"  # scripted group (container) (typed FeaturePython)
  n = 1
  ref = Po_element
FEATURE [App::DocumentObjectGroupPython] G4_Po  # scripted group (container) (typed FeaturePython)
  Dunit = g/cm3
  Dvalue = 9.32
  Group = -> [Po_element001]
  conduct = 2
  density = 1
  expand = 3
  formula = Po
  name = G4_Po
  specific = 4
FEATURE [App::DocumentObjectGroupPython] At_element001  label="At_element : 1"  # scripted group (container) (typed FeaturePython)
  n = 1
  ref = At_element
FEATURE [App::DocumentObjectGroupPython] G4_At  # scripted group (container) (typed FeaturePython)
  Dunit = g/cm3
  Dvalue = 9.32
  Group = -> [At_element001]
  conduct = 2
  density = 1
  expand = 3
  formula = At
  name = G4_At
  specific = 4
FEATURE [App::DocumentObjectGroupPython] Rn_element001  label="Rn_element : 1"  # scripted group (container) (typed FeaturePython)
  n = 1
  ref = Rn_element
FEATURE [App::DocumentObjectGroupPython] G4_Rn  # scripted group (container) (typed FeaturePython)
  Dunit = g/cm3
  Dvalue = 0.00900662
  Group = -> [Rn_element001]
  conduct = 2
  density = 1
  expand = 3
  formula = Rn
  name = G4_Rn
  specific = 4
FEATURE [App::DocumentObjectGroupPython] Fr_element001  label="Fr_element : 1"  # scripted group (container) (typed FeaturePython)
  n = 1
  ref = Fr_element
FEATURE [App::DocumentObjectGroupPython] G4_Fr  # scripted group (container) (typed FeaturePython)
  Dunit = g/cm3
  Dvalue = 1
  Group = -> [Fr_element001]
  conduct = 2
  density = 1
  expand = 3
  formula = Fr
  name = G4_Fr
  specific = 4
FEATURE [App::DocumentObjectGroupPython] Ra_element001  label="Ra_element : 1"  # scripted group (container) (typed FeaturePython)
  n = 1
  ref = Ra_element
FEATURE [App::DocumentObjectGroupPython] G4_Ra  # scripted group (container) (typed FeaturePython)
  Dunit = g/cm3
  Dvalue = 5
  Group = -> [Ra_element001]
  conduct = 2
  density = 1
  expand = 3
  formula = Ra
  name = G4_Ra
  specific = 4
FEATURE [App::DocumentObjectGroupPython] Ac_element001  label="Ac_element : 1"  # scripted group (container) (typed FeaturePython)
  n = 1
  ref = Ac_element
FEATURE [App::DocumentObjectGroupPython] G4_Ac  # scripted group (container) (typed FeaturePython)
  Dunit = g/cm3
  Dvalue = 10.07
  Group = -> [Ac_element001]
  conduct = 2
  density = 1
  expand = 3
  formula = Ac
  name = G4_Ac
  specific = 4
FEATURE [App::DocumentObjectGroupPython] Th_element001  label="Th_element : 1"  # scripted group (container) (typed FeaturePython)
  n = 1
  ref = Th_element
FEATURE [App::DocumentObjectGroupPython] G4_Th  # scripted group (container) (typed FeaturePython)
  Dunit = g/cm3
  Dvalue = 11.72
  Group = -> [Th_element001]
  conduct = 2
  density = 1
  expand = 3
  formula = Th
  name = G4_Th
  specific = 4
FEATURE [App::DocumentObjectGroupPython] Pa_element001  label="Pa_element : 1"  # scripted group (container) (typed FeaturePython)
  n = 1
  ref = Pa_element
FEATURE [App::DocumentObjectGroupPython] G4_Pa  # scripted group (container) (typed FeaturePython)
  Dunit = g/cm3
  Dvalue = 15.37
  Group = -> [Pa_element001]
  conduct = 2
  density = 1
  expand = 3
  formula = Pa
  name = G4_Pa
  specific = 4
FEATURE [App::DocumentObjectGroupPython] U_element004  label="U_element : 004"  # scripted group (container) (typed FeaturePython)
  n = 1
  ref = U_element
FEATURE [App::DocumentObjectGroupPython] G4_U  # scripted group (container) (typed FeaturePython)
  Dunit = g/cm3
  Dvalue = 18.95
  Group = -> [U_element004]
  conduct = 2
  density = 1
  expand = 3
  formula = U
  name = G4_U
  specific = 4
FEATURE [App::DocumentObjectGroupPython] Np_element001  label="Np_element : 1"  # scripted group (container) (typed FeaturePython)
  n = 1
  ref = Np_element
FEATURE [App::DocumentObjectGroupPython] G4_Np  # scripted group (container) (typed FeaturePython)
  Dunit = g/cm3
  Dvalue = 20.25
  Group = -> [Np_element001]
  conduct = 2
  density = 1
  expand = 3
  formula = Np
  name = G4_Np
  specific = 4
FEATURE [App::DocumentObjectGroupPython] Pu_element002  label="Pu_element : 002"  # scripted group (container) (typed FeaturePython)
  n = 1
  ref = Pu_element
FEATURE [App::DocumentObjectGroupPython] G4_Pu  # scripted group (container) (typed FeaturePython)
  Dunit = g/cm3
  Dvalue = 19.84
  Group = -> [Pu_element002]
  conduct = 2
  density = 1
  expand = 3
  formula = Pu
  name = G4_Pu
  specific = 4
FEATURE [App::DocumentObjectGroupPython] Am_element001  label="Am_element : 1"  # scripted group (container) (typed FeaturePython)
  n = 1
  ref = Am_element
FEATURE [App::DocumentObjectGroupPython] G4_Am  # scripted group (container) (typed FeaturePython)
  Dunit = g/cm3
  Dvalue = 13.67
  Group = -> [Am_element001]
  conduct = 2
  density = 1
  expand = 3
  formula = Am
  name = G4_Am
  specific = 4
FEATURE [App::DocumentObjectGroupPython] Cm_element001  label="Cm_element : 1"  # scripted group (container) (typed FeaturePython)
  n = 1
  ref = Cm_element
FEATURE [App::DocumentObjectGroupPython] G4_Cm  # scripted group (container) (typed FeaturePython)
  Dunit = g/cm3
  Dvalue = 13.51
  Group = -> [Cm_element001]
  conduct = 2
  density = 1
  expand = 3
  formula = Cm
  name = G4_Cm
  specific = 4
FEATURE [App::DocumentObjectGroupPython] Bk_element001  label="Bk_element : 1"  # scripted group (container) (typed FeaturePython)
  n = 1
  ref = Bk_element
FEATURE [App::DocumentObjectGroupPython] G4_Bk  # scripted group (container) (typed FeaturePython)
  Dunit = g/cm3
  Dvalue = 14
  Group = -> [Bk_element001]
  conduct = 2
  density = 1
  expand = 3
  formula = Bk
  name = G4_Bk
  specific = 4
FEATURE [App::DocumentObjectGroupPython] Cf_element001  label="Cf_element : 1"  # scripted group (container) (typed FeaturePython)
  n = 1
  ref = Cf_element
FEATURE [App::DocumentObjectGroupPython] G4_Cf  # scripted group (container) (typed FeaturePython)
  Dunit = g/cm3
  Dvalue = 10
  Group = -> [Cf_element001]
  conduct = 2
  density = 1
  expand = 3
  formula = Cf
  name = G4_Cf
  specific = 4
FEATURE [App::DocumentObjectGroupPython] Element  # scripted group (container) (typed FeaturePython)
  Group = -> [G4_H,G4_He,G4_Li,G4_Be,G4_B,G4_C,G4_N,G4_O,G4_F,G4_Ne,G4_Na,G4_Mg,G4_Al,G4_Si,G4_P,G4_S,G4_Cl,G4_Ar,G4_K,G4_Ca,G4_Sc,G4_Ti,G4_V,G4_Cr,G4_Mn,G4_Fe,G4_Co,G4_Ni,G4_Cu,G4_Zn,G4_Ga,G4_Ge,G4_As,G4_Se,G4_Br,G4_Kr,G4_Rb,G4_Sr,G4_Y,G4_Zr,G4_Nb,G4_Mo,G4_Tc,G4_Ru,G4_Rh,G4_Pd,G4_Ag,G4_Cd,G4_In,G4_Sn,G4_Sb,G4_Te,G4_I,G4_Xe,G4_Cs,G4_Ba,G4_La,G4_Ce,G4_Pr,G4_Nd,G4_Pm,G4_Sm,G4_Eu,G4_Gd,G4_Tb,G4_Dy,G4_Ho,G4_Er,+30 more]
FEATURE [App::DocumentObjectGroupPython] H_element114  label="H_element : 063"  # scripted group (container) (typed FeaturePython)
  n = 2
  ref = H_element
FEATURE [App::DocumentObjectGroupPython] G4_lH2  # scripted group (container) (typed FeaturePython)
  Dunit = g/cm3
  Dvalue = 0.0708
  Group = -> [H_element114]
  conduct = 2
  density = 1
  expand = 3
  formula = G4_lH2
  name = G4_lH2
  specific = 4
FEATURE [App::DocumentObjectGroupPython] N_element049  label="N_element : 022"  # scripted group (container) (typed FeaturePython)
  n = 2
  ref = N_element
FEATURE [App::DocumentObjectGroupPython] G4_lN2  # scripted group (container) (typed FeaturePython)
  Dunit = g/cm3
  Dvalue = 0.807
  Group = -> [N_element049]
  conduct = 2
  density = 1
  expand = 3
  formula = G4_lN2
  name = G4_lN2
  specific = 4
FEATURE [App::DocumentObjectGroupPython] O_element106  label="O_element : 060"  # scripted group (container) (typed FeaturePython)
  n = 2
  ref = O_element
FEATURE [App::DocumentObjectGroupPython] G4_lO2  # scripted group (container) (typed FeaturePython)
  Dunit = g/cm3
  Dvalue = 1.141
  Group = -> [O_element106]
  conduct = 2
  density = 1
  expand = 3
  formula = G4_lO2
  name = G4_lO2
  specific = 4
FEATURE [App::DocumentObjectGroupPython] Ar  label="Ar : 1"  # scripted group (container) (typed FeaturePython)
  n = 1
  ref = Ar
FEATURE [App::DocumentObjectGroupPython] G4_lAr  # scripted group (container) (typed FeaturePython)
  Dunit = g/cm3
  Dvalue = 1.396
  Group = -> [Ar]
  conduct = 2
  density = 1
  expand = 3
  formula = G4_lAr
  name = G4_lAr
  specific = 4
FEATURE [App::DocumentObjectGroupPython] Br  label="Br : 1"  # scripted group (container) (typed FeaturePython)
  n = 1
  ref = Br
FEATURE [App::DocumentObjectGroupPython] G4_lBr  # scripted group (container) (typed FeaturePython)
  Dunit = g/cm3
  Dvalue = 3.1028
  Group = -> [Br]
  conduct = 2
  density = 1
  expand = 3
  formula = G4_lBr
  name = G4_lBr
  specific = 4
FEATURE [App::DocumentObjectGroupPython] Kr  label="Kr : 1"  # scripted group (container) (typed FeaturePython)
  n = 1
  ref = Kr
FEATURE [App::DocumentObjectGroupPython] G4_lKr  # scripted group (container) (typed FeaturePython)
  Dunit = g/cm3
  Dvalue = 2.418
  Group = -> [Kr]
  conduct = 2
  density = 1
  expand = 3
  formula = G4_lKr
  name = G4_lKr
  specific = 4
FEATURE [App::DocumentObjectGroupPython] Xe  label="Xe : 1"  # scripted group (container) (typed FeaturePython)
  n = 1
  ref = Xe
FEATURE [App::DocumentObjectGroupPython] G4_lXe  # scripted group (container) (typed FeaturePython)
  Dunit = g/cm3
  Dvalue = 2.953
  Group = -> [Xe]
  conduct = 2
  density = 1
  expand = 3
  formula = G4_lXe
  name = G4_lXe
  specific = 4
FEATURE [App::DocumentObjectGroupPython] O_element107  label="O_element : 061"  # scripted group (container) (typed FeaturePython)
  n = 4
  ref = O_element
FEATURE [App::DocumentObjectGroupPython] Pb_element004  label="Pb_element : 002"  # scripted group (container) (typed FeaturePython)
  n = 1
  ref = Pb_element
FEATURE [App::DocumentObjectGroupPython] W_element005  label="W_element : 005"  # scripted group (container) (typed FeaturePython)
  n = 1
  ref = W_element
FEATURE [App::DocumentObjectGroupPython] G4_PbWO4  # scripted group (container) (typed FeaturePython)
  Dunit = g/cm3
  Dvalue = 8.28
  Group = -> [O_element107,Pb_element004,W_element005]
  conduct = 2
  density = 1
  expand = 3
  formula = G4_PbWO4
  name = G4_PbWO4
  specific = 4
FEATURE [App::DocumentObjectGroupPython] alactic  label="alactic : 1"  # scripted group (container) (typed FeaturePython)
  n = 1
  ref = alactic
FEATURE [App::DocumentObjectGroupPython] G4_Galactic  # scripted group (container) (typed FeaturePython)
  Dunit = g/cm3
  Dvalue = 0
  Group = -> [alactic]
  conduct = 2
  density = 1
  expand = 3
  formula = G4_Galactic
  name = G4_Galactic
  specific = 4
FEATURE [App::DocumentObjectGroupPython] RAPHITE_POROUS  label="RAPHITE_POROUS : 1"  # scripted group (container) (typed FeaturePython)
  n = 1
  ref = RAPHITE_POROUS
FEATURE [App::DocumentObjectGroupPython] G4_GRAPHITE_POROUS  # scripted group (container) (typed FeaturePython)
  Dunit = g/cm3
  Dvalue = 1.7
  Group = -> [RAPHITE_POROUS]
  conduct = 2
  density = 1
  expand = 3
  formula = G4_GRAPHITE_POROUS
  name = G4_GRAPHITE_POROUS
  specific = 4
FEATURE [App::DocumentObjectGroupPython] H_element115  label="H_element : 0.150"  # scripted group (container) (typed FeaturePython)
  n = 0.080538
FEATURE [App::DocumentObjectGroupPython] C_element125  label="C_element : 0.600"  # scripted group (container) (typed FeaturePython)
  n = 0.599848
FEATURE [App::DocumentObjectGroupPython] O_element108  label="O_element : 0.320"  # scripted group (container) (typed FeaturePython)
  n = 0.319614
FEATURE [App::DocumentObjectGroupPython] G4_LUCITE  # scripted group (container) (typed FeaturePython)
  Dunit = g/cm3
  Dvalue = 1.19
  Group = -> [H_element115,C_element125,O_element108]
  conduct = 2
  density = 1
  expand = 3
  formula = G4_LUCITE
  name = G4_LUCITE
  specific = 4
FEATURE [App::DocumentObjectGroupPython] Cu_element002  label="Cu_element : 62"  # scripted group (container) (typed FeaturePython)
  n = 62
  ref = Cu_element
FEATURE [App::DocumentObjectGroupPython] Zn_element002  label="Zn_element : 35"  # scripted group (container) (typed FeaturePython)
  n = 35
  ref = Zn_element
FEATURE [App::DocumentObjectGroupPython] Pb_element005  label="Pb_element : 3"  # scripted group (container) (typed FeaturePython)
  n = 3
  ref = Pb_element
FEATURE [App::DocumentObjectGroupPython] G4_BRASS  # scripted group (container) (typed FeaturePython)
  Dunit = g/cm3
  Dvalue = 8.52
  Group = -> [Cu_element002,Zn_element002,Pb_element005]
  conduct = 2
  density = 1
  expand = 3
  formula = G4_BRASS
  name = G4_BRASS
  specific = 4
FEATURE [App::DocumentObjectGroupPython] Cu_element003  label="Cu_element : 89"  # scripted group (container) (typed FeaturePython)
  n = 89
  ref = Cu_element
FEATURE [App::DocumentObjectGroupPython] Zn_element003  label="Zn_element : 9"  # scripted group (container) (typed FeaturePython)
  n = 9
  ref = Zn_element
FEATURE [App::DocumentObjectGroupPython] Pb_element006  label="Pb_element : 2"  # scripted group (container) (typed FeaturePython)
  n = 2
  ref = Pb_element
FEATURE [App::DocumentObjectGroupPython] G4_BRONZE  # scripted group (container) (typed FeaturePython)
  Dunit = g/cm3
  Dvalue = 8.82
  Group = -> [Cu_element003,Zn_element003,Pb_element006]
  conduct = 2
  density = 1
  expand = 3
  formula = G4_BRONZE
  name = G4_BRONZE
  specific = 4
FEATURE [App::DocumentObjectGroupPython] Fe_element008  label="Fe_element : 74"  # scripted group (container) (typed FeaturePython)
  n = 74
  ref = Fe_element
FEATURE [App::DocumentObjectGroupPython] Cr_element002  label="Cr_element : 18"  # scripted group (container) (typed FeaturePython)
  n = 18
  ref = Cr_element
FEATURE [App::DocumentObjectGroupPython] Ni_element002  label="Ni_element : 8"  # scripted group (container) (typed FeaturePython)
  n = 8
  ref = Ni_element
FEATURE [App::DocumentObjectGroupPython] G4_STAINLESS_STEEL  label="G4_STAINLESS-STEEL"  # scripted group (container) (typed FeaturePython)
  Dunit = g/cm3
  Dvalue = 8
  Group = -> [Fe_element008,Cr_element002,Ni_element002]
  conduct = 2
  density = 1
  expand = 3
  formula = G4_STAINLESS-STEEL
  name = G4_STAINLESS-STEEL
  specific = 4
FEATURE [App::DocumentObjectGroupPython] H_element116  label="H_element : 064"  # scripted group (container) (typed FeaturePython)
  n = 18
  ref = H_element
FEATURE [App::DocumentObjectGroupPython] C_element126  label="C_element : 071"  # scripted group (container) (typed FeaturePython)
  n = 12
  ref = C_element
FEATURE [App::DocumentObjectGroupPython] O_element109  label="O_element : 062"  # scripted group (container) (typed FeaturePython)
  n = 7
  ref = O_element
FEATURE [App::DocumentObjectGroupPython] G4_CR39  # scripted group (container) (typed FeaturePython)
  Dunit = g/cm3
  Dvalue = 1.32
  Group = -> [H_element116,C_element126,O_element109]
  conduct = 2
  density = 1
  expand = 3
  formula = G4_CR39
  name = G4_CR39
  specific = 4
FEATURE [App::DocumentObjectGroupPython] H_element117  label="H_element : 38"  # scripted group (container) (typed FeaturePython)
  n = 38
  ref = H_element
FEATURE [App::DocumentObjectGroupPython] C_element127  label="C_element : 072"  # scripted group (container) (typed FeaturePython)
  n = 18
  ref = C_element
FEATURE [App::DocumentObjectGroupPython] O_element110  label="O_element : 063"  # scripted group (container) (typed FeaturePython)
  n = 1
  ref = O_element
FEATURE [App::DocumentObjectGroupPython] G4_OCTADECANOL  # scripted group (container) (typed FeaturePython)
  Dunit = g/cm3
  Dvalue = 0.812
  Group = -> [H_element117,C_element127,O_element110]
  conduct = 2
  density = 1
  expand = 3
  formula = G4_OCTADECANOL
  name = G4_OCTADECANOL
  specific = 4
FEATURE [App::DocumentObjectGroupPython] HEP  # scripted group (container) (typed FeaturePython)
  Group = -> [G4_lH2,G4_lN2,G4_lO2,G4_lAr,G4_lBr,G4_lKr,G4_lXe,G4_PbWO4,G4_Galactic,G4_GRAPHITE_POROUS,G4_LUCITE,G4_BRASS,G4_BRONZE,G4_STAINLESS_STEEL,G4_CR39,G4_OCTADECANOL]
FEATURE [App::DocumentObjectGroupPython] C_element128  label="C_element : 073"  # scripted group (container) (typed FeaturePython)
  n = 14
  ref = C_element
FEATURE [App::DocumentObjectGroupPython] H_element118  label="H_element : 065"  # scripted group (container) (typed FeaturePython)
  n = 10
  ref = H_element
FEATURE [App::DocumentObjectGroupPython] O_element111  label="O_element : 064"  # scripted group (container) (typed FeaturePython)
  n = 2
  ref = O_element
FEATURE [App::DocumentObjectGroupPython] N_element050  label="N_element : 023"  # scripted group (container) (typed FeaturePython)
  n = 2
  ref = N_element
FEATURE [App::DocumentObjectGroupPython] G4_KEVLAR  # scripted group (container) (typed FeaturePython)
  Dunit = g/cm3
  Dvalue = 1.44
  Group = -> [C_element128,H_element118,O_element111,N_element050]
  conduct = 2
  density = 1
  expand = 3
  formula = G4_KEVLAR
  name = G4_KEVLAR
  specific = 4
FEATURE [App::DocumentObjectGroupPython] C_element129  label="C_element : 074"  # scripted group (container) (typed FeaturePython)
  n = 10
  ref = C_element
FEATURE [App::DocumentObjectGroupPython] H_element119  label="H_element : 066"  # scripted group (container) (typed FeaturePython)
  n = 8
  ref = H_element
FEATURE [App::DocumentObjectGroupPython] O_element112  label="O_element : 065"  # scripted group (container) (typed FeaturePython)
  n = 4
  ref = O_element
FEATURE [App::DocumentObjectGroupPython] G4_DACRON  # scripted group (container) (typed FeaturePython)
  Dunit = g/cm3
  Dvalue = 1.4
  Group = -> [C_element129,H_element119,O_element112]
  conduct = 2
  density = 1
  expand = 3
  formula = G4_DACRON
  name = G4_DACRON
  specific = 4
FEATURE [App::DocumentObjectGroupPython] C_element130  label="C_element : 075"  # scripted group (container) (typed FeaturePython)
  n = 4
  ref = C_element
FEATURE [App::DocumentObjectGroupPython] H_element120  label="H_element : 067"  # scripted group (container) (typed FeaturePython)
  n = 5
  ref = H_element
FEATURE [App::DocumentObjectGroupPython] Cl_element030  label="Cl_element : 016"  # scripted group (container) (typed FeaturePython)
  n = 1
  ref = Cl_element
FEATURE [App::DocumentObjectGroupPython] G4_NEOPRENE  # scripted group (container) (typed FeaturePython)
  Dunit = g/cm3
  Dvalue = 1.23
  Group = -> [C_element130,H_element120,Cl_element030]
  conduct = 2
  density = 1
  expand = 3
  formula = G4_NEOPRENE
  name = G4_NEOPRENE
  specific = 4
FEATURE [App::DocumentObjectGroupPython] Space  # scripted group (container) (typed FeaturePython)
  Group = -> [G4_KEVLAR,G4_DACRON,G4_NEOPRENE]
FEATURE [App::DocumentObjectGroupPython] H_element121  label="H_element : 068"  # scripted group (container) (typed FeaturePython)
  n = 5
  ref = H_element
FEATURE [App::DocumentObjectGroupPython] C_element131  label="C_element : 076"  # scripted group (container) (typed FeaturePython)
  n = 4
  ref = C_element
FEATURE [App::DocumentObjectGroupPython] N_element051  label="N_element : 3"  # scripted group (container) (typed FeaturePython)
  n = 3
  ref = N_element
FEATURE [App::DocumentObjectGroupPython] O_element113  label="O_element : 066"  # scripted group (container) (typed FeaturePython)
  n = 1
  ref = O_element
FEATURE [App::DocumentObjectGroupPython] G4_CYTOSINE  # scripted group (container) (typed FeaturePython)
  Dunit = g/cm3
  Dvalue = 1.55
  Group = -> [H_element121,C_element131,N_element051,O_element113]
  conduct = 2
  density = 1
  expand = 3
  formula = G4_CYTOSINE
  name = G4_CYTOSINE
  specific = 4
FEATURE [App::DocumentObjectGroupPython] H_element122  label="H_element : 069"  # scripted group (container) (typed FeaturePython)
  n = 6
  ref = H_element
FEATURE [App::DocumentObjectGroupPython] C_element132  label="C_element : 077"  # scripted group (container) (typed FeaturePython)
  n = 5
  ref = C_element
FEATURE [App::DocumentObjectGroupPython] N_element052  label="N_element : 024"  # scripted group (container) (typed FeaturePython)
  n = 2
  ref = N_element
FEATURE [App::DocumentObjectGroupPython] O_element114  label="O_element : 067"  # scripted group (container) (typed FeaturePython)
  n = 2
  ref = O_element
FEATURE [App::DocumentObjectGroupPython] G4_THYMINE  # scripted group (container) (typed FeaturePython)
  Dunit = g/cm3
  Dvalue = 1.23
  Group = -> [H_element122,C_element132,N_element052,O_element114]
  conduct = 2
  density = 1
  expand = 3
  formula = G4_THYMINE
  name = G4_THYMINE
  specific = 4
FEATURE [App::DocumentObjectGroupPython] H_element123  label="H_element : 070"  # scripted group (container) (typed FeaturePython)
  n = 4
  ref = H_element
FEATURE [App::DocumentObjectGroupPython] C_element133  label="C_element : 078"  # scripted group (container) (typed FeaturePython)
  n = 4
  ref = C_element
FEATURE [App::DocumentObjectGroupPython] N_element053  label="N_element : 025"  # scripted group (container) (typed FeaturePython)
  n = 2
  ref = N_element
FEATURE [App::DocumentObjectGroupPython] O_element115  label="O_element : 068"  # scripted group (container) (typed FeaturePython)
  n = 2
  ref = O_element
FEATURE [App::DocumentObjectGroupPython] G4_URACIL  # scripted group (container) (typed FeaturePython)
  Dunit = g/cm3
  Dvalue = 1.32
  Group = -> [H_element123,C_element133,N_element053,O_element115]
  conduct = 2
  density = 1
  expand = 3
  formula = G4_URACIL
  name = G4_URACIL
  specific = 4
FEATURE [App::DocumentObjectGroupPython] H_element124  label="H_element : 071"  # scripted group (container) (typed FeaturePython)
  n = 4
  ref = H_element
FEATURE [App::DocumentObjectGroupPython] C_element134  label="C_element : 079"  # scripted group (container) (typed FeaturePython)
  n = 5
  ref = C_element
FEATURE [App::DocumentObjectGroupPython] N_element054  label="N_element : 026"  # scripted group (container) (typed FeaturePython)
  n = 5
  ref = N_element
FEATURE [App::DocumentObjectGroupPython] G4_DNA_ADENINE  # scripted group (container) (typed FeaturePython)
  Dunit = g/cm3
  Dvalue = 1
  Group = -> [H_element124,C_element134,N_element054]
  conduct = 2
  density = 1
  expand = 3
  formula = G4_DNA_ADENINE
  name = G4_DNA_ADENINE
  specific = 4
FEATURE [App::DocumentObjectGroupPython] H_element125  label="H_element : 072"  # scripted group (container) (typed FeaturePython)
  n = 4
  ref = H_element
FEATURE [App::DocumentObjectGroupPython] C_element135  label="C_element : 080"  # scripted group (container) (typed FeaturePython)
  n = 5
  ref = C_element
FEATURE [App::DocumentObjectGroupPython] N_element055  label="N_element : 027"  # scripted group (container) (typed FeaturePython)
  n = 5
  ref = N_element
FEATURE [App::DocumentObjectGroupPython] O_element116  label="O_element : 069"  # scripted group (container) (typed FeaturePython)
  n = 1
  ref = O_element
FEATURE [App::DocumentObjectGroupPython] G4_DNA_GUANINE  # scripted group (container) (typed FeaturePython)
  Dunit = g/cm3
  Dvalue = 1
  Group = -> [H_element125,C_element135,N_element055,O_element116]
  conduct = 2
  density = 1
  expand = 3
  formula = G4_DNA_GUANINE
  name = G4_DNA_GUANINE
  specific = 4
FEATURE [App::DocumentObjectGroupPython] H_element126  label="H_element : 073"  # scripted group (container) (typed FeaturePython)
  n = 4
  ref = H_element
FEATURE [App::DocumentObjectGroupPython] C_element136  label="C_element : 081"  # scripted group (container) (typed FeaturePython)
  n = 4
  ref = C_element
FEATURE [App::DocumentObjectGroupPython] N_element056  label="N_element : 028"  # scripted group (container) (typed FeaturePython)
  n = 3
  ref = N_element
FEATURE [App::DocumentObjectGroupPython] O_element117  label="O_element : 070"  # scripted group (container) (typed FeaturePython)
  n = 1
  ref = O_element
FEATURE [App::DocumentObjectGroupPython] G4_DNA_CYTOSINE  # scripted group (container) (typed FeaturePython)
  Dunit = g/cm3
  Dvalue = 1
  Group = -> [H_element126,C_element136,N_element056,O_element117]
  conduct = 2
  density = 1
  expand = 3
  formula = G4_DNA_CYTOSINE
  name = G4_DNA_CYTOSINE
  specific = 4
FEATURE [App::DocumentObjectGroupPython] H_element127  label="H_element : 074"  # scripted group (container) (typed FeaturePython)
  n = 5
  ref = H_element
FEATURE [App::DocumentObjectGroupPython] C_element137  label="C_element : 082"  # scripted group (container) (typed FeaturePython)
  n = 5
  ref = C_element
FEATURE [App::DocumentObjectGroupPython] N_element057  label="N_element : 029"  # scripted group (container) (typed FeaturePython)
  n = 2
  ref = N_element
FEATURE [App::DocumentObjectGroupPython] O_element118  label="O_element : 071"  # scripted group (container) (typed FeaturePython)
  n = 2
  ref = O_element
FEATURE [App::DocumentObjectGroupPython] G4_DNA_THYMINE  # scripted group (container) (typed FeaturePython)
  Dunit = g/cm3
  Dvalue = 1
  Group = -> [H_element127,C_element137,N_element057,O_element118]
  conduct = 2
  density = 1
  expand = 3
  formula = G4_DNA_THYMINE
  name = G4_DNA_THYMINE
  specific = 4
FEATURE [App::DocumentObjectGroupPython] H_element128  label="H_element : 075"  # scripted group (container) (typed FeaturePython)
  n = 3
  ref = H_element
FEATURE [App::DocumentObjectGroupPython] C_element138  label="C_element : 083"  # scripted group (container) (typed FeaturePython)
  n = 4
  ref = C_element
FEATURE [App::DocumentObjectGroupPython] N_element058  label="N_element : 030"  # scripted group (container) (typed FeaturePython)
  n = 2
  ref = N_element
FEATURE [App::DocumentObjectGroupPython] O_element119  label="O_element : 072"  # scripted group (container) (typed FeaturePython)
  n = 2
  ref = O_element
FEATURE [App::DocumentObjectGroupPython] G4_DNA_URACIL  # scripted group (container) (typed FeaturePython)
  Dunit = g/cm3
  Dvalue = 1
  Group = -> [H_element128,C_element138,N_element058,O_element119]
  conduct = 2
  density = 1
  expand = 3
  formula = G4_DNA_URACIL
  name = G4_DNA_URACIL
  specific = 4
FEATURE [App::DocumentObjectGroupPython] H_element129  label="H_element : 076"  # scripted group (container) (typed FeaturePython)
  n = 10
  ref = H_element
FEATURE [App::DocumentObjectGroupPython] C_element139  label="C_element : 084"  # scripted group (container) (typed FeaturePython)
  n = 10
  ref = C_element
FEATURE [App::DocumentObjectGroupPython] N_element059  label="N_element : 031"  # scripted group (container) (typed FeaturePython)
  n = 5
  ref = N_element
FEATURE [App::DocumentObjectGroupPython] O_element120  label="O_element : 073"  # scripted group (container) (typed FeaturePython)
  n = 4
  ref = O_element
FEATURE [App::DocumentObjectGroupPython] G4_DNA_ADENOSINE  # scripted group (container) (typed FeaturePython)
  Dunit = g/cm3
  Dvalue = 1
  Group = -> [H_element129,C_element139,N_element059,O_element120]
  conduct = 2
  density = 1
  expand = 3
  formula = G4_DNA_ADENOSINE
  name = G4_DNA_ADENOSINE
  specific = 4
FEATURE [App::DocumentObjectGroupPython] H_element130  label="H_element : 077"  # scripted group (container) (typed FeaturePython)
  n = 10
  ref = H_element
FEATURE [App::DocumentObjectGroupPython] C_element140  label="C_element : 085"  # scripted group (container) (typed FeaturePython)
  n = 10
  ref = C_element
FEATURE [App::DocumentObjectGroupPython] N_element060  label="N_element : 032"  # scripted group (container) (typed FeaturePython)
  n = 5
  ref = N_element
FEATURE [App::DocumentObjectGroupPython] O_element121  label="O_element : 074"  # scripted group (container) (typed FeaturePython)
  n = 5
  ref = O_element
FEATURE [App::DocumentObjectGroupPython] G4_DNA_GUANOSINE  # scripted group (container) (typed FeaturePython)
  Dunit = g/cm3
  Dvalue = 1
  Group = -> [H_element130,C_element140,N_element060,O_element121]
  conduct = 2
  density = 1
  expand = 3
  formula = G4_DNA_GUANOSINE
  name = G4_DNA_GUANOSINE
  specific = 4
FEATURE [App::DocumentObjectGroupPython] H_element131  label="H_element : 078"  # scripted group (container) (typed FeaturePython)
  n = 10
  ref = H_element
FEATURE [App::DocumentObjectGroupPython] C_element141  label="C_element : 086"  # scripted group (container) (typed FeaturePython)
  n = 9
  ref = C_element
FEATURE [App::DocumentObjectGroupPython] N_element061  label="N_element : 033"  # scripted group (container) (typed FeaturePython)
  n = 3
  ref = N_element
FEATURE [App::DocumentObjectGroupPython] O_element122  label="O_element : 075"  # scripted group (container) (typed FeaturePython)
  n = 5
  ref = O_element
FEATURE [App::DocumentObjectGroupPython] G4_DNA_CYTIDINE  # scripted group (container) (typed FeaturePython)
  Dunit = g/cm3
  Dvalue = 1
  Group = -> [H_element131,C_element141,N_element061,O_element122]
  conduct = 2
  density = 1
  expand = 3
  formula = G4_DNA_CYTIDINE
  name = G4_DNA_CYTIDINE
  specific = 4
FEATURE [App::DocumentObjectGroupPython] H_element132  label="H_element : 079"  # scripted group (container) (typed FeaturePython)
  n = 9
  ref = H_element
FEATURE [App::DocumentObjectGroupPython] C_element142  label="C_element : 087"  # scripted group (container) (typed FeaturePython)
  n = 9
  ref = C_element
FEATURE [App::DocumentObjectGroupPython] N_element062  label="N_element : 034"  # scripted group (container) (typed FeaturePython)
  n = 2
  ref = N_element
FEATURE [App::DocumentObjectGroupPython] O_element123  label="O_element : 076"  # scripted group (container) (typed FeaturePython)
  n = 6
  ref = O_element
FEATURE [App::DocumentObjectGroupPython] G4_DNA_URIDINE  # scripted group (container) (typed FeaturePython)
  Dunit = g/cm3
  Dvalue = 1
  Group = -> [H_element132,C_element142,N_element062,O_element123]
  conduct = 2
  density = 1
  expand = 3
  formula = G4_DNA_URIDINE
  name = G4_DNA_URIDINE
  specific = 4
FEATURE [App::DocumentObjectGroupPython] H_element133  label="H_element : 080"  # scripted group (container) (typed FeaturePython)
  n = 11
  ref = H_element
FEATURE [App::DocumentObjectGroupPython] C_element143  label="C_element : 088"  # scripted group (container) (typed FeaturePython)
  n = 10
  ref = C_element
FEATURE [App::DocumentObjectGroupPython] N_element063  label="N_element : 035"  # scripted group (container) (typed FeaturePython)
  n = 2
  ref = N_element
FEATURE [App::DocumentObjectGroupPython] O_element124  label="O_element : 077"  # scripted group (container) (typed FeaturePython)
  n = 6
  ref = O_element
FEATURE [App::DocumentObjectGroupPython] G4_DNA_METHYLURIDINE  # scripted group (container) (typed FeaturePython)
  Dunit = g/cm3
  Dvalue = 1
  Group = -> [H_element133,C_element143,N_element063,O_element124]
  conduct = 2
  density = 1
  expand = 3
  formula = G4_DNA_METHYLURIDINE
  name = G4_DNA_METHYLURIDINE
  specific = 4
FEATURE [App::DocumentObjectGroupPython] P_element014  label="P_element : 003"  # scripted group (container) (typed FeaturePython)
  n = 1
  ref = P_element
FEATURE [App::DocumentObjectGroupPython] O_element125  label="O_element : 078"  # scripted group (container) (typed FeaturePython)
  n = 3
  ref = O_element
FEATURE [App::DocumentObjectGroupPython] G4_DNA_MONOPHOSPHATE  # scripted group (container) (typed FeaturePython)
  Dunit = g/cm3
  Dvalue = 1
  Group = -> [P_element014,O_element125]
  conduct = 2
  density = 1
  expand = 3
  formula = G4_DNA_MONOPHOSPHATE
  name = G4_DNA_MONOPHOSPHATE
  specific = 4
FEATURE [App::DocumentObjectGroupPython] H_element134  label="H_element : 081"  # scripted group (container) (typed FeaturePython)
  n = 10
  ref = H_element
FEATURE [App::DocumentObjectGroupPython] C_element144  label="C_element : 089"  # scripted group (container) (typed FeaturePython)
  n = 10
  ref = C_element
FEATURE [App::DocumentObjectGroupPython] N_element064  label="N_element : 036"  # scripted group (container) (typed FeaturePython)
  n = 5
  ref = N_element
FEATURE [App::DocumentObjectGroupPython] O_element126  label="O_element : 079"  # scripted group (container) (typed FeaturePython)
  n = 7
  ref = O_element
FEATURE [App::DocumentObjectGroupPython] P_element015  label="P_element : 004"  # scripted group (container) (typed FeaturePython)
  n = 1
  ref = P_element
FEATURE [App::DocumentObjectGroupPython] G4_DNA_A  # scripted group (container) (typed FeaturePython)
  Dunit = g/cm3
  Dvalue = 1
  Group = -> [H_element134,C_element144,N_element064,O_element126,P_element015]
  conduct = 2
  density = 1
  expand = 3
  formula = G4_DNA_A
  name = G4_DNA_A
  specific = 4
FEATURE [App::DocumentObjectGroupPython] H_element135  label="H_element : 082"  # scripted group (container) (typed FeaturePython)
  n = 10
  ref = H_element
FEATURE [App::DocumentObjectGroupPython] C_element145  label="C_element : 090"  # scripted group (container) (typed FeaturePython)
  n = 10
  ref = C_element
FEATURE [App::DocumentObjectGroupPython] N_element065  label="N_element : 037"  # scripted group (container) (typed FeaturePython)
  n = 5
  ref = N_element
FEATURE [App::DocumentObjectGroupPython] O_element127  label="O_element : 8"  # scripted group (container) (typed FeaturePython)
  n = 8
  ref = O_element
FEATURE [App::DocumentObjectGroupPython] P_element016  label="P_element : 005"  # scripted group (container) (typed FeaturePython)
  n = 1
  ref = P_element
FEATURE [App::DocumentObjectGroupPython] G4_DNA_G  # scripted group (container) (typed FeaturePython)
  Dunit = g/cm3
  Dvalue = 1
  Group = -> [H_element135,C_element145,N_element065,O_element127,P_element016]
  conduct = 2
  density = 1
  expand = 3
  formula = G4_DNA_G
  name = G4_DNA_G
  specific = 4
FEATURE [App::DocumentObjectGroupPython] H_element136  label="H_element : 083"  # scripted group (container) (typed FeaturePython)
  n = 10
  ref = H_element
FEATURE [App::DocumentObjectGroupPython] C_element146  label="C_element : 091"  # scripted group (container) (typed FeaturePython)
  n = 9
  ref = C_element
FEATURE [App::DocumentObjectGroupPython] N_element066  label="N_element : 038"  # scripted group (container) (typed FeaturePython)
  n = 3
  ref = N_element
FEATURE [App::DocumentObjectGroupPython] O_element128  label="O_element : 080"  # scripted group (container) (typed FeaturePython)
  n = 8
  ref = O_element
FEATURE [App::DocumentObjectGroupPython] P_element017  label="P_element : 006"  # scripted group (container) (typed FeaturePython)
  n = 1
  ref = P_element
FEATURE [App::DocumentObjectGroupPython] G4_DNA_C  # scripted group (container) (typed FeaturePython)
  Dunit = g/cm3
  Dvalue = 1
  Group = -> [H_element136,C_element146,N_element066,O_element128,P_element017]
  conduct = 2
  density = 1
  expand = 3
  formula = G4_DNA_C
  name = G4_DNA_C
  specific = 4
FEATURE [App::DocumentObjectGroupPython] H_element137  label="H_element : 084"  # scripted group (container) (typed FeaturePython)
  n = 9
  ref = H_element
FEATURE [App::DocumentObjectGroupPython] C_element147  label="C_element : 092"  # scripted group (container) (typed FeaturePython)
  n = 9
  ref = C_element
FEATURE [App::DocumentObjectGroupPython] N_element067  label="N_element : 039"  # scripted group (container) (typed FeaturePython)
  n = 2
  ref = N_element
FEATURE [App::DocumentObjectGroupPython] O_element129  label="O_element : 9"  # scripted group (container) (typed FeaturePython)
  n = 9
  ref = O_element
FEATURE [App::DocumentObjectGroupPython] P_element018  label="P_element : 007"  # scripted group (container) (typed FeaturePython)
  n = 1
  ref = P_element
FEATURE [App::DocumentObjectGroupPython] G4_DNA_U  # scripted group (container) (typed FeaturePython)
  Dunit = g/cm3
  Dvalue = 1
  Group = -> [H_element137,C_element147,N_element067,O_element129,P_element018]
  conduct = 2
  density = 1
  expand = 3
  formula = G4_DNA_U
  name = G4_DNA_U
  specific = 4
FEATURE [App::DocumentObjectGroupPython] H_element138  label="H_element : 085"  # scripted group (container) (typed FeaturePython)
  n = 11
  ref = H_element
FEATURE [App::DocumentObjectGroupPython] C_element148  label="C_element : 093"  # scripted group (container) (typed FeaturePython)
  n = 10
  ref = C_element
FEATURE [App::DocumentObjectGroupPython] N_element068  label="N_element : 040"  # scripted group (container) (typed FeaturePython)
  n = 2
  ref = N_element
FEATURE [App::DocumentObjectGroupPython] O_element130  label="O_element : 081"  # scripted group (container) (typed FeaturePython)
  n = 9
  ref = O_element
FEATURE [App::DocumentObjectGroupPython] P_element019  label="P_element : 008"  # scripted group (container) (typed FeaturePython)
  n = 1
  ref = P_element
FEATURE [App::DocumentObjectGroupPython] G4_DNA_MU  # scripted group (container) (typed FeaturePython)
  Dunit = g/cm3
  Dvalue = 1
  Group = -> [H_element138,C_element148,N_element068,O_element130,P_element019]
  conduct = 2
  density = 1
  expand = 3
  formula = G4_DNA_MU
  name = G4_DNA_MU
  specific = 4
FEATURE [App::DocumentObjectGroupPython] BioChemical  # scripted group (container) (typed FeaturePython)
  Group = -> [G4_CYTOSINE,G4_THYMINE,G4_URACIL,G4_DNA_ADENINE,G4_DNA_GUANINE,G4_DNA_CYTOSINE,G4_DNA_THYMINE,G4_DNA_URACIL,G4_DNA_ADENOSINE,G4_DNA_GUANOSINE,G4_DNA_CYTIDINE,G4_DNA_URIDINE,G4_DNA_METHYLURIDINE,G4_DNA_MONOPHOSPHATE,G4_DNA_A,G4_DNA_G,G4_DNA_C,G4_DNA_U,G4_DNA_MU]
FEATURE [App::DocumentObjectGroupPython] G4Materials  # scripted group (container) (typed FeaturePython)
  Group = -> [NIST,Element,HEP,Space,BioChemical]
  version = 1
FEATURE [App::DocumentObjectGroupPython] Geant4  # scripted group (container) (typed FeaturePython)
  Group = -> [G4Isotopes,G4Elements,G4Materials]
FEATURE [App::DocumentObjectGroupPython] Materials  # scripted group (container) (typed FeaturePython)
  Group = -> [Geant4]
FEATURE [Part::FeaturePython] GDMLBox_WorldBox  # WARN: FeaturePython — macro-defined, semantics opaque (R4)
  lunit = 2
  material = 5
  x = 200
  y = 200
  z = 200
FEATURE [Sketcher::SketchObject] Sketch
  FullyConstrained = false
  sketch-geometry (5):
    g0: ArcOfParabola CenterX=25.5233 CenterY=-14.8036 CenterZ=0 NormalX=0 NormalY=0 NormalZ=1 Focal=15.7547 AngleXU=-2.61216 StartAngle=-26.5589 EndAngle=30.7535
    g1: GeomPoint X=11.9255 Y=-22.7604 Z=0
    g2: LineSegment StartX=25.5233 StartY=-14.8036 StartZ=0 EndX=11.9255 EndY=-22.7604 EndZ=0
    g3: LineSegment StartX=2.44918 StartY=2.46618 StartZ=0 EndX=19.9697 EndY=-18.0533 EndZ=0
    g4: LineSegment StartX=19.9697 StartY=-18.0533 StartZ=0 EndX=28.1021 EndY=-48.9263 EndZ=0
  constraints (6):
    c: InternalAlignment(g1,g0)
    c: InternalAlignment(g2,g0)
    c: Coincident(g3,g0)
    c: PointOnObject(g3,g2)
    c: Coincident(g3,g4)
    c: Coincident(g4,g0)
FEATURE [Part::Extrusion] Extrude
  Base = -> Sketch
  Dir = (0,0,1)
  DirMode = 2
  FaceMakerClass = Part::FaceMakerBullseye
  LengthFwd = 10
  LengthRev = 0
  Solid = true
  Symmetric = false
FEATURE [App::Part] Part
  Group = -> [Sketch,Extrude]
  Origin = -> Origin001
  material = 5
FEATURE [App::Part] worldVOL
  Group = -> [GDMLBox_WorldBox,Part]
  Origin = -> Origin
